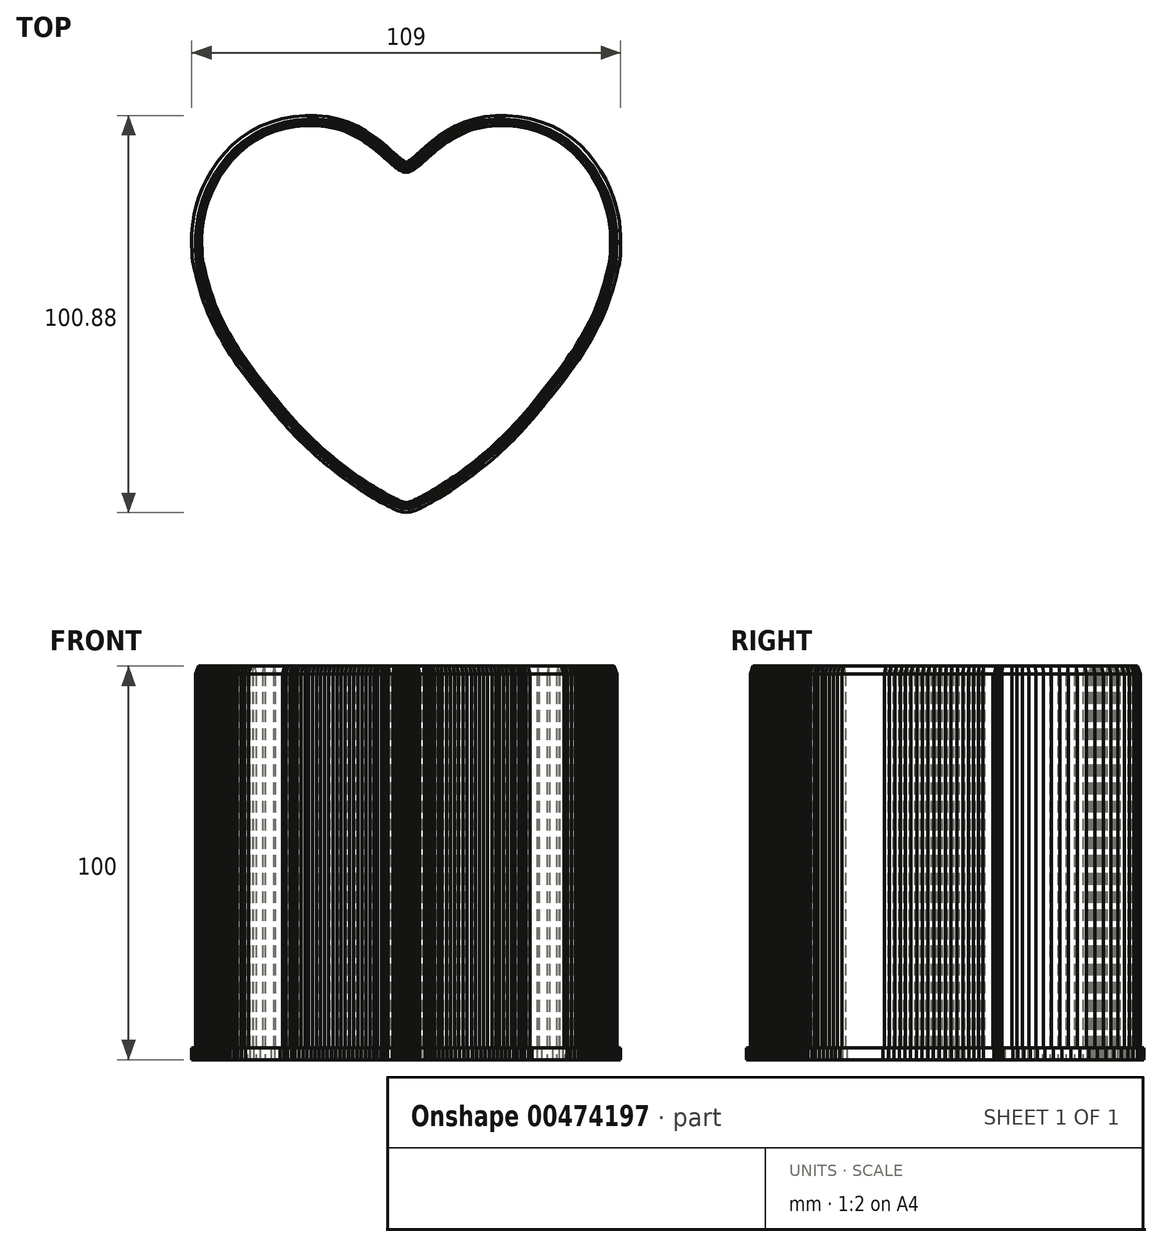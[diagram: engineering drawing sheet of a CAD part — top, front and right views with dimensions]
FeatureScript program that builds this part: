
annotation { "Feature Type Name" : "Feature", "Feature Type Description" : "" }
export const myFeature = defineFeature(function(context is Context, id is Id, definition is map)
    precondition{}
    {
        {
            var Q0;
            Q0=qCreatedBy(makeId("Top.planeOp"),FACE);
            var sketch = newSketch(context, id + "F0", { "sketchPlane" : qUnion([Q0])});
            skLineSegment(sketch, "E0", {"start": v(-2.52, 39.71) * mm, "end": v(-3.6, 40.68) * mm});
            skLineSegment(sketch, "E1", {"start": v(-3.6, 40.68) * mm, "end": v(-4.9, 41.83) * mm});
            skLineSegment(sketch, "E2", {"start": v(-4.9, 41.83) * mm, "end": v(-6.41, 43.08) * mm});
            skLineSegment(sketch, "E3", {"start": v(-6.41, 43.08) * mm, "end": v(-8.12, 44.37) * mm});
            skLineSegment(sketch, "E4", {"start": v(-8.12, 44.37) * mm, "end": v(-10.02, 45.64) * mm});
            skLineSegment(sketch, "E5", {"start": v(-10.02, 45.64) * mm, "end": v(-12.12, 46.83) * mm});
            skLineSegment(sketch, "E6", {"start": v(-12.12, 46.83) * mm, "end": v(-14.4, 47.86) * mm});
            skLineSegment(sketch, "E7", {"start": v(-14.4, 47.86) * mm, "end": v(-16.88, 48.68) * mm});
            skLineSegment(sketch, "E8", {"start": v(-16.88, 48.68) * mm, "end": v(-19.52, 49.24) * mm});
            skLineSegment(sketch, "E9", {"start": v(-19.52, 49.24) * mm, "end": v(-22.3, 49.52) * mm});
            skLineSegment(sketch, "E10", {"start": v(-22.3, 49.52) * mm, "end": v(-25.16, 49.52) * mm});
            skLineSegment(sketch, "E11", {"start": v(-25.16, 49.52) * mm, "end": v(-28.05, 49.25) * mm});
            skLineSegment(sketch, "E12", {"start": v(-28.05, 49.25) * mm, "end": v(-30.93, 48.72) * mm});
            skLineSegment(sketch, "E13", {"start": v(-30.93, 48.72) * mm, "end": v(-33.74, 47.91) * mm});
            skLineSegment(sketch, "E14", {"start": v(-33.74, 47.91) * mm, "end": v(-36.43, 46.84) * mm});
            skLineSegment(sketch, "E15", {"start": v(-36.43, 46.84) * mm, "end": v(-38.97, 45.5) * mm});
            skLineSegment(sketch, "E16", {"start": v(-38.97, 45.5) * mm, "end": v(-41.3, 43.92) * mm});
            skLineSegment(sketch, "E17", {"start": v(-41.3, 43.92) * mm, "end": v(-43.42, 42.11) * mm});
            skLineSegment(sketch, "E18", {"start": v(-43.42, 42.11) * mm, "end": v(-45.33, 40.13) * mm});
            skLineSegment(sketch, "E19", {"start": v(-45.33, 40.13) * mm, "end": v(-47.03, 38.01) * mm});
            skLineSegment(sketch, "E20", {"start": v(-47.03, 38.01) * mm, "end": v(-48.51, 35.8) * mm});
            skLineSegment(sketch, "E21", {"start": v(-48.51, 35.8) * mm, "end": v(-49.8, 33.56) * mm});
            skLineSegment(sketch, "E22", {"start": v(-49.8, 33.56) * mm, "end": v(-50.86, 31.3) * mm});
            skLineSegment(sketch, "E23", {"start": v(-50.86, 31.3) * mm, "end": v(-51.72, 29.1) * mm});
            skLineSegment(sketch, "E24", {"start": v(-51.72, 29.1) * mm, "end": v(-52.38, 26.96) * mm});
            skLineSegment(sketch, "E25", {"start": v(-52.38, 26.96) * mm, "end": v(-52.86, 24.92) * mm});
            skLineSegment(sketch, "E26", {"start": v(-52.86, 24.92) * mm, "end": v(-53.18, 23) * mm});
            skLineSegment(sketch, "E27", {"start": v(-53.18, 23) * mm, "end": v(-53.38, 21.24) * mm});
            skLineSegment(sketch, "E28", {"start": v(-53.38, 21.24) * mm, "end": v(-53.48, 19.62) * mm});
            skLineSegment(sketch, "E29", {"start": v(-53.48, 19.62) * mm, "end": v(-53.5, 18.18) * mm});
            skLineSegment(sketch, "E30", {"start": v(-53.5, 18.18) * mm, "end": v(-53.49, 16.93) * mm});
            skLineSegment(sketch, "E31", {"start": v(-53.49, 16.93) * mm, "end": v(-53.45, 15.9) * mm});
            skLineSegment(sketch, "E32", {"start": v(-53.45, 15.9) * mm, "end": v(-53.42, 15.07) * mm});
            skLineSegment(sketch, "E33", {"start": v(-53.42, 15.07) * mm, "end": v(-53.38, 14.44) * mm});
            skLineSegment(sketch, "E34", {"start": v(-53.38, 14.44) * mm, "end": v(-53.35, 13.92) * mm});
            skLineSegment(sketch, "E35", {"start": v(-53.35, 13.92) * mm, "end": v(-53.3, 13.49) * mm});
            skLineSegment(sketch, "E36", {"start": v(-53.3, 13.49) * mm, "end": v(-53.24, 13.07) * mm});
            skLineSegment(sketch, "E37", {"start": v(-53.24, 13.07) * mm, "end": v(-53.16, 12.62) * mm});
            skLineSegment(sketch, "E38", {"start": v(-53.16, 12.62) * mm, "end": v(-53.04, 12.1) * mm});
            skLineSegment(sketch, "E39", {"start": v(-53.04, 12.1) * mm, "end": v(-52.88, 11.43) * mm});
            skLineSegment(sketch, "E40", {"start": v(-52.88, 11.43) * mm, "end": v(-52.69, 10.6) * mm});
            skLineSegment(sketch, "E41", {"start": v(-52.69, 10.6) * mm, "end": v(-52.44, 9.6) * mm});
            skLineSegment(sketch, "E42", {"start": v(-52.44, 9.6) * mm, "end": v(-52.15, 8.45) * mm});
            skLineSegment(sketch, "E43", {"start": v(-52.15, 8.45) * mm, "end": v(-51.82, 7.2) * mm});
            skLineSegment(sketch, "E44", {"start": v(-51.82, 7.2) * mm, "end": v(-51.43, 5.85) * mm});
            skLineSegment(sketch, "E45", {"start": v(-51.43, 5.85) * mm, "end": v(-51, 4.44) * mm});
            skLineSegment(sketch, "E46", {"start": v(-51, 4.44) * mm, "end": v(-50.5, 2.98) * mm});
            skLineSegment(sketch, "E47", {"start": v(-50.5, 2.98) * mm, "end": v(-49.96, 1.5) * mm});
            skLineSegment(sketch, "E48", {"start": v(-49.96, 1.5) * mm, "end": v(-49.36, 0.03) * mm});
            skLineSegment(sketch, "E49", {"start": v(-49.36, 0.03) * mm, "end": v(-48.7, -1.44) * mm});
            skLineSegment(sketch, "E50", {"start": v(-48.7, -1.44) * mm, "end": v(-48, -2.9) * mm});
            skLineSegment(sketch, "E51", {"start": v(-48, -2.9) * mm, "end": v(-47.26, -4.36) * mm});
            skLineSegment(sketch, "E52", {"start": v(-47.26, -4.36) * mm, "end": v(-46.47, -5.8) * mm});
            skLineSegment(sketch, "E53", {"start": v(-46.47, -5.8) * mm, "end": v(-45.64, -7.23) * mm});
            skLineSegment(sketch, "E54", {"start": v(-45.64, -7.23) * mm, "end": v(-44.78, -8.65) * mm});
            skLineSegment(sketch, "E55", {"start": v(-44.78, -8.65) * mm, "end": v(-43.88, -10.05) * mm});
            skLineSegment(sketch, "E56", {"start": v(-43.88, -10.05) * mm, "end": v(-42.95, -11.44) * mm});
            skLineSegment(sketch, "E57", {"start": v(-42.95, -11.44) * mm, "end": v(-42, -12.8) * mm});
            skLineSegment(sketch, "E58", {"start": v(-42, -12.8) * mm, "end": v(-41.04, -14.16) * mm});
            skLineSegment(sketch, "E59", {"start": v(-41.04, -14.16) * mm, "end": v(-40.05, -15.49) * mm});
            skLineSegment(sketch, "E60", {"start": v(-40.05, -15.49) * mm, "end": v(-39.07, -16.8) * mm});
            skLineSegment(sketch, "E61", {"start": v(-39.07, -16.8) * mm, "end": v(-38.08, -18.08) * mm});
            skLineSegment(sketch, "E62", {"start": v(-38.08, -18.08) * mm, "end": v(-37.1, -19.33) * mm});
            skLineSegment(sketch, "E63", {"start": v(-37.1, -19.33) * mm, "end": v(-36.12, -20.56) * mm});
            skLineSegment(sketch, "E64", {"start": v(-36.12, -20.56) * mm, "end": v(-35.16, -21.76) * mm});
            skLineSegment(sketch, "E65", {"start": v(-35.16, -21.76) * mm, "end": v(-34.22, -22.93) * mm});
            skLineSegment(sketch, "E66", {"start": v(-34.22, -22.93) * mm, "end": v(-33.28, -24.07) * mm});
            skLineSegment(sketch, "E67", {"start": v(-33.28, -24.07) * mm, "end": v(-32.35, -25.18) * mm});
            skLineSegment(sketch, "E68", {"start": v(-32.35, -25.18) * mm, "end": v(-31.42, -26.28) * mm});
            skLineSegment(sketch, "E69", {"start": v(-31.42, -26.28) * mm, "end": v(-30.5, -27.34) * mm});
            skLineSegment(sketch, "E70", {"start": v(-30.5, -27.34) * mm, "end": v(-29.56, -28.38) * mm});
            skLineSegment(sketch, "E71", {"start": v(-29.56, -28.38) * mm, "end": v(-28.62, -29.4) * mm});
            skLineSegment(sketch, "E72", {"start": v(-28.62, -29.4) * mm, "end": v(-27.67, -30.4) * mm});
            skLineSegment(sketch, "E73", {"start": v(-27.67, -30.4) * mm, "end": v(-26.71, -31.38) * mm});
            skLineSegment(sketch, "E74", {"start": v(-26.71, -31.38) * mm, "end": v(-25.74, -32.34) * mm});
            skLineSegment(sketch, "E75", {"start": v(-25.74, -32.34) * mm, "end": v(-24.76, -33.28) * mm});
            skLineSegment(sketch, "E76", {"start": v(-24.76, -33.28) * mm, "end": v(-23.77, -34.2) * mm});
            skLineSegment(sketch, "E77", {"start": v(-23.77, -34.2) * mm, "end": v(-22.76, -35.1) * mm});
            skLineSegment(sketch, "E78", {"start": v(-22.76, -35.1) * mm, "end": v(-21.75, -36) * mm});
            skLineSegment(sketch, "E79", {"start": v(-21.75, -36) * mm, "end": v(-20.72, -36.87) * mm});
            skLineSegment(sketch, "E80", {"start": v(-20.72, -36.87) * mm, "end": v(-19.69, -37.74) * mm});
            skLineSegment(sketch, "E81", {"start": v(-19.69, -37.74) * mm, "end": v(-18.64, -38.58) * mm});
            skLineSegment(sketch, "E82", {"start": v(-18.64, -38.58) * mm, "end": v(-17.6, -39.42) * mm});
            skLineSegment(sketch, "E83", {"start": v(-17.6, -39.42) * mm, "end": v(-16.53, -40.23) * mm});
            skLineSegment(sketch, "E84", {"start": v(-16.53, -40.23) * mm, "end": v(-15.47, -41.02) * mm});
            skLineSegment(sketch, "E85", {"start": v(-15.47, -41.02) * mm, "end": v(-14.41, -41.8) * mm});
            skLineSegment(sketch, "E86", {"start": v(-14.41, -41.8) * mm, "end": v(-13.35, -42.55) * mm});
            skLineSegment(sketch, "E87", {"start": v(-13.35, -42.55) * mm, "end": v(-12.29, -43.27) * mm});
            skLineSegment(sketch, "E88", {"start": v(-12.29, -43.27) * mm, "end": v(-11.23, -43.97) * mm});
            skLineSegment(sketch, "E89", {"start": v(-11.23, -43.97) * mm, "end": v(-10.19, -44.65) * mm});
            skLineSegment(sketch, "E90", {"start": v(-10.19, -44.65) * mm, "end": v(-9.17, -45.28) * mm});
            skLineSegment(sketch, "E91", {"start": v(-9.17, -45.28) * mm, "end": v(-8.17, -45.88) * mm});
            skLineSegment(sketch, "E92", {"start": v(-8.17, -45.88) * mm, "end": v(-7.22, -46.44) * mm});
            skLineSegment(sketch, "E93", {"start": v(-7.22, -46.44) * mm, "end": v(-6.3, -46.95) * mm});
            skLineSegment(sketch, "E94", {"start": v(-6.3, -46.95) * mm, "end": v(-5.46, -47.42) * mm});
            skLineSegment(sketch, "E95", {"start": v(-5.46, -47.42) * mm, "end": v(-4.67, -47.83) * mm});
            skLineSegment(sketch, "E96", {"start": v(-4.67, -47.83) * mm, "end": v(-3.96, -48.18) * mm});
            skLineSegment(sketch, "E97", {"start": v(-3.96, -48.18) * mm, "end": v(-3.35, -48.48) * mm});
            skLineSegment(sketch, "E98", {"start": v(-3.35, -48.48) * mm, "end": v(-2.8, -48.74) * mm});
            skLineSegment(sketch, "E99", {"start": v(-2.8, -48.74) * mm, "end": v(-2.31, -48.95) * mm});
            skLineSegment(sketch, "E100", {"start": v(-2.31, -48.95) * mm, "end": v(-1.86, -49.12) * mm});
            skLineSegment(sketch, "E101", {"start": v(-1.86, -49.12) * mm, "end": v(-1.44, -49.26) * mm});
            skLineSegment(sketch, "E102", {"start": v(-1.44, -49.26) * mm, "end": v(-1.04, -49.36) * mm});
            skLineSegment(sketch, "E103", {"start": v(-1.04, -49.36) * mm, "end": v(-0.63, -49.42) * mm});
            skLineSegment(sketch, "E104", {"start": v(-0.63, -49.42) * mm, "end": v(0, -49.52) * mm});
            skLineSegment(sketch, "E105", {"start": v(0, -49.52) * mm, "end": v(0.63, -49.42) * mm});
            skLineSegment(sketch, "E106", {"start": v(0.63, -49.42) * mm, "end": v(1.04, -49.36) * mm});
            skLineSegment(sketch, "E107", {"start": v(1.04, -49.36) * mm, "end": v(1.44, -49.26) * mm});
            skLineSegment(sketch, "E108", {"start": v(1.44, -49.26) * mm, "end": v(1.86, -49.12) * mm});
            skLineSegment(sketch, "E109", {"start": v(1.86, -49.12) * mm, "end": v(2.31, -48.95) * mm});
            skLineSegment(sketch, "E110", {"start": v(2.31, -48.95) * mm, "end": v(2.8, -48.74) * mm});
            skLineSegment(sketch, "E111", {"start": v(2.8, -48.74) * mm, "end": v(3.35, -48.48) * mm});
            skLineSegment(sketch, "E112", {"start": v(3.35, -48.48) * mm, "end": v(3.96, -48.18) * mm});
            skLineSegment(sketch, "E113", {"start": v(3.96, -48.18) * mm, "end": v(4.67, -47.83) * mm});
            skLineSegment(sketch, "E114", {"start": v(4.67, -47.83) * mm, "end": v(5.46, -47.42) * mm});
            skLineSegment(sketch, "E115", {"start": v(5.46, -47.42) * mm, "end": v(6.3, -46.95) * mm});
            skLineSegment(sketch, "E116", {"start": v(6.3, -46.95) * mm, "end": v(7.22, -46.44) * mm});
            skLineSegment(sketch, "E117", {"start": v(7.22, -46.44) * mm, "end": v(8.17, -45.88) * mm});
            skLineSegment(sketch, "E118", {"start": v(8.17, -45.88) * mm, "end": v(9.17, -45.28) * mm});
            skLineSegment(sketch, "E119", {"start": v(9.17, -45.28) * mm, "end": v(10.19, -44.65) * mm});
            skLineSegment(sketch, "E120", {"start": v(10.19, -44.65) * mm, "end": v(11.23, -43.97) * mm});
            skLineSegment(sketch, "E121", {"start": v(11.23, -43.97) * mm, "end": v(12.29, -43.27) * mm});
            skLineSegment(sketch, "E122", {"start": v(12.29, -43.27) * mm, "end": v(13.35, -42.55) * mm});
            skLineSegment(sketch, "E123", {"start": v(13.35, -42.55) * mm, "end": v(14.41, -41.8) * mm});
            skLineSegment(sketch, "E124", {"start": v(14.41, -41.8) * mm, "end": v(15.47, -41.02) * mm});
            skLineSegment(sketch, "E125", {"start": v(15.47, -41.02) * mm, "end": v(16.53, -40.23) * mm});
            skLineSegment(sketch, "E126", {"start": v(16.53, -40.23) * mm, "end": v(17.6, -39.42) * mm});
            skLineSegment(sketch, "E127", {"start": v(17.6, -39.42) * mm, "end": v(18.64, -38.58) * mm});
            skLineSegment(sketch, "E128", {"start": v(18.64, -38.58) * mm, "end": v(19.69, -37.74) * mm});
            skLineSegment(sketch, "E129", {"start": v(19.69, -37.74) * mm, "end": v(20.72, -36.87) * mm});
            skLineSegment(sketch, "E130", {"start": v(20.72, -36.87) * mm, "end": v(21.75, -36) * mm});
            skLineSegment(sketch, "E131", {"start": v(21.75, -36) * mm, "end": v(22.76, -35.1) * mm});
            skLineSegment(sketch, "E132", {"start": v(22.76, -35.1) * mm, "end": v(23.77, -34.2) * mm});
            skLineSegment(sketch, "E133", {"start": v(23.77, -34.2) * mm, "end": v(24.76, -33.28) * mm});
            skLineSegment(sketch, "E134", {"start": v(24.76, -33.28) * mm, "end": v(25.74, -32.34) * mm});
            skLineSegment(sketch, "E135", {"start": v(25.74, -32.34) * mm, "end": v(26.71, -31.38) * mm});
            skLineSegment(sketch, "E136", {"start": v(26.71, -31.38) * mm, "end": v(27.67, -30.4) * mm});
            skLineSegment(sketch, "E137", {"start": v(27.67, -30.4) * mm, "end": v(28.62, -29.4) * mm});
            skLineSegment(sketch, "E138", {"start": v(28.62, -29.4) * mm, "end": v(29.56, -28.38) * mm});
            skLineSegment(sketch, "E139", {"start": v(29.56, -28.38) * mm, "end": v(30.5, -27.34) * mm});
            skLineSegment(sketch, "E140", {"start": v(30.5, -27.34) * mm, "end": v(31.42, -26.28) * mm});
            skLineSegment(sketch, "E141", {"start": v(31.42, -26.28) * mm, "end": v(32.35, -25.18) * mm});
            skLineSegment(sketch, "E142", {"start": v(32.35, -25.18) * mm, "end": v(33.28, -24.07) * mm});
            skLineSegment(sketch, "E143", {"start": v(33.28, -24.07) * mm, "end": v(34.22, -22.93) * mm});
            skLineSegment(sketch, "E144", {"start": v(34.22, -22.93) * mm, "end": v(35.16, -21.76) * mm});
            skLineSegment(sketch, "E145", {"start": v(35.16, -21.76) * mm, "end": v(36.12, -20.56) * mm});
            skLineSegment(sketch, "E146", {"start": v(36.12, -20.56) * mm, "end": v(37.1, -19.33) * mm});
            skLineSegment(sketch, "E147", {"start": v(37.1, -19.33) * mm, "end": v(38.08, -18.08) * mm});
            skLineSegment(sketch, "E148", {"start": v(38.08, -18.08) * mm, "end": v(39.07, -16.8) * mm});
            skLineSegment(sketch, "E149", {"start": v(39.07, -16.8) * mm, "end": v(40.05, -15.49) * mm});
            skLineSegment(sketch, "E150", {"start": v(40.05, -15.49) * mm, "end": v(41.04, -14.16) * mm});
            skLineSegment(sketch, "E151", {"start": v(41.04, -14.16) * mm, "end": v(42, -12.8) * mm});
            skLineSegment(sketch, "E152", {"start": v(42, -12.8) * mm, "end": v(42.95, -11.44) * mm});
            skLineSegment(sketch, "E153", {"start": v(42.95, -11.44) * mm, "end": v(43.88, -10.05) * mm});
            skLineSegment(sketch, "E154", {"start": v(43.88, -10.05) * mm, "end": v(44.78, -8.65) * mm});
            skLineSegment(sketch, "E155", {"start": v(44.78, -8.65) * mm, "end": v(45.64, -7.23) * mm});
            skLineSegment(sketch, "E156", {"start": v(45.64, -7.23) * mm, "end": v(46.47, -5.8) * mm});
            skLineSegment(sketch, "E157", {"start": v(46.47, -5.8) * mm, "end": v(47.26, -4.36) * mm});
            skLineSegment(sketch, "E158", {"start": v(47.26, -4.36) * mm, "end": v(48, -2.9) * mm});
            skLineSegment(sketch, "E159", {"start": v(48, -2.9) * mm, "end": v(48.7, -1.44) * mm});
            skLineSegment(sketch, "E160", {"start": v(48.7, -1.44) * mm, "end": v(49.36, 0.03) * mm});
            skLineSegment(sketch, "E161", {"start": v(49.36, 0.03) * mm, "end": v(49.96, 1.5) * mm});
            skLineSegment(sketch, "E162", {"start": v(49.96, 1.5) * mm, "end": v(50.5, 2.98) * mm});
            skLineSegment(sketch, "E163", {"start": v(50.5, 2.98) * mm, "end": v(51, 4.44) * mm});
            skLineSegment(sketch, "E164", {"start": v(51, 4.44) * mm, "end": v(51.43, 5.85) * mm});
            skLineSegment(sketch, "E165", {"start": v(51.43, 5.85) * mm, "end": v(51.82, 7.2) * mm});
            skLineSegment(sketch, "E166", {"start": v(51.82, 7.2) * mm, "end": v(52.15, 8.45) * mm});
            skLineSegment(sketch, "E167", {"start": v(52.15, 8.45) * mm, "end": v(52.44, 9.6) * mm});
            skLineSegment(sketch, "E168", {"start": v(52.44, 9.6) * mm, "end": v(52.69, 10.6) * mm});
            skLineSegment(sketch, "E169", {"start": v(52.69, 10.6) * mm, "end": v(52.88, 11.43) * mm});
            skLineSegment(sketch, "E170", {"start": v(52.88, 11.43) * mm, "end": v(53.04, 12.1) * mm});
            skLineSegment(sketch, "E171", {"start": v(53.04, 12.1) * mm, "end": v(53.16, 12.62) * mm});
            skLineSegment(sketch, "E172", {"start": v(53.16, 12.62) * mm, "end": v(53.24, 13.07) * mm});
            skLineSegment(sketch, "E173", {"start": v(53.24, 13.07) * mm, "end": v(53.3, 13.49) * mm});
            skLineSegment(sketch, "E174", {"start": v(53.3, 13.49) * mm, "end": v(53.35, 13.92) * mm});
            skLineSegment(sketch, "E175", {"start": v(53.35, 13.92) * mm, "end": v(53.38, 14.44) * mm});
            skLineSegment(sketch, "E176", {"start": v(53.38, 14.44) * mm, "end": v(53.42, 15.07) * mm});
            skLineSegment(sketch, "E177", {"start": v(53.42, 15.07) * mm, "end": v(53.45, 15.9) * mm});
            skLineSegment(sketch, "E178", {"start": v(53.45, 15.9) * mm, "end": v(53.49, 16.93) * mm});
            skLineSegment(sketch, "E179", {"start": v(53.49, 16.93) * mm, "end": v(53.5, 18.18) * mm});
            skLineSegment(sketch, "E180", {"start": v(53.5, 18.18) * mm, "end": v(53.48, 19.62) * mm});
            skLineSegment(sketch, "E181", {"start": v(53.48, 19.62) * mm, "end": v(53.38, 21.24) * mm});
            skLineSegment(sketch, "E182", {"start": v(53.38, 21.24) * mm, "end": v(53.18, 23) * mm});
            skLineSegment(sketch, "E183", {"start": v(53.18, 23) * mm, "end": v(52.86, 24.92) * mm});
            skLineSegment(sketch, "E184", {"start": v(52.86, 24.92) * mm, "end": v(52.38, 26.96) * mm});
            skLineSegment(sketch, "E185", {"start": v(52.38, 26.96) * mm, "end": v(51.72, 29.1) * mm});
            skLineSegment(sketch, "E186", {"start": v(51.72, 29.1) * mm, "end": v(50.86, 31.3) * mm});
            skLineSegment(sketch, "E187", {"start": v(50.86, 31.3) * mm, "end": v(49.8, 33.56) * mm});
            skLineSegment(sketch, "E188", {"start": v(49.8, 33.56) * mm, "end": v(48.51, 35.8) * mm});
            skLineSegment(sketch, "E189", {"start": v(48.51, 35.8) * mm, "end": v(47.03, 38.01) * mm});
            skLineSegment(sketch, "E190", {"start": v(47.03, 38.01) * mm, "end": v(45.33, 40.13) * mm});
            skLineSegment(sketch, "E191", {"start": v(45.33, 40.13) * mm, "end": v(43.42, 42.11) * mm});
            skLineSegment(sketch, "E192", {"start": v(43.42, 42.11) * mm, "end": v(41.3, 43.92) * mm});
            skLineSegment(sketch, "E193", {"start": v(41.3, 43.92) * mm, "end": v(38.97, 45.5) * mm});
            skLineSegment(sketch, "E194", {"start": v(38.97, 45.5) * mm, "end": v(36.43, 46.84) * mm});
            skLineSegment(sketch, "E195", {"start": v(36.43, 46.84) * mm, "end": v(33.74, 47.91) * mm});
            skLineSegment(sketch, "E196", {"start": v(33.74, 47.91) * mm, "end": v(30.93, 48.72) * mm});
            skLineSegment(sketch, "E197", {"start": v(30.93, 48.72) * mm, "end": v(28.05, 49.25) * mm});
            skLineSegment(sketch, "E198", {"start": v(28.05, 49.25) * mm, "end": v(25.16, 49.52) * mm});
            skLineSegment(sketch, "E199", {"start": v(25.16, 49.52) * mm, "end": v(22.3, 49.52) * mm});
            skLineSegment(sketch, "E200", {"start": v(22.3, 49.52) * mm, "end": v(19.52, 49.24) * mm});
            skLineSegment(sketch, "E201", {"start": v(19.52, 49.24) * mm, "end": v(16.88, 48.68) * mm});
            skLineSegment(sketch, "E202", {"start": v(16.88, 48.68) * mm, "end": v(14.4, 47.86) * mm});
            skLineSegment(sketch, "E203", {"start": v(14.4, 47.86) * mm, "end": v(12.12, 46.83) * mm});
            skLineSegment(sketch, "E204", {"start": v(12.12, 46.83) * mm, "end": v(10.02, 45.64) * mm});
            skLineSegment(sketch, "E205", {"start": v(10.02, 45.64) * mm, "end": v(8.12, 44.37) * mm});
            skLineSegment(sketch, "E206", {"start": v(8.12, 44.37) * mm, "end": v(6.41, 43.08) * mm});
            skLineSegment(sketch, "E207", {"start": v(6.41, 43.08) * mm, "end": v(4.9, 41.83) * mm});
            skLineSegment(sketch, "E208", {"start": v(4.9, 41.83) * mm, "end": v(3.6, 40.68) * mm});
            skLineSegment(sketch, "E209", {"start": v(3.6, 40.68) * mm, "end": v(2.52, 39.71) * mm});
            skLineSegment(sketch, "E210", {"start": v(2.52, 39.71) * mm, "end": v(2.06, 39.32) * mm});
            skLineSegment(sketch, "E211", {"start": v(2.06, 39.32) * mm, "end": v(1.65, 38.97) * mm});
            skLineSegment(sketch, "E212", {"start": v(1.65, 38.97) * mm, "end": v(1.29, 38.68) * mm});
            skLineSegment(sketch, "E213", {"start": v(1.29, 38.68) * mm, "end": v(0.96, 38.43) * mm});
            skLineSegment(sketch, "E214", {"start": v(0.96, 38.43) * mm, "end": v(0.68, 38.23) * mm});
            skLineSegment(sketch, "E215", {"start": v(0.68, 38.23) * mm, "end": v(0.42, 38.07) * mm});
            skLineSegment(sketch, "E216", {"start": v(0.42, 38.07) * mm, "end": v(0.2, 37.95) * mm});
            skLineSegment(sketch, "E217", {"start": v(0.2, 37.95) * mm, "end": v(0, 37.87) * mm});
            skLineSegment(sketch, "E218", {"start": v(0, 37.87) * mm, "end": v(-0.2, 37.95) * mm});
            skLineSegment(sketch, "E219", {"start": v(-0.2, 37.95) * mm, "end": v(-0.42, 38.07) * mm});
            skLineSegment(sketch, "E220", {"start": v(-0.42, 38.07) * mm, "end": v(-0.68, 38.23) * mm});
            skLineSegment(sketch, "E221", {"start": v(-0.68, 38.23) * mm, "end": v(-0.96, 38.43) * mm});
            skLineSegment(sketch, "E222", {"start": v(-0.96, 38.43) * mm, "end": v(-1.29, 38.68) * mm});
            skLineSegment(sketch, "E223", {"start": v(-1.29, 38.68) * mm, "end": v(-1.65, 38.97) * mm});
            skLineSegment(sketch, "E224", {"start": v(-1.65, 38.97) * mm, "end": v(-2.06, 39.32) * mm});
            skLineSegment(sketch, "E225", {"start": v(-2.06, 39.32) * mm, "end": v(-2.52, 39.71) * mm});
            skSolve(sketch);
        }
        {
            var Q0;
            Q0 = qSketchRegion(id + "F0", true);
            extrude(context, id + "F1", {"entities" : qUnion([Q0]), "depth" : 100 * mm, "offsetDistance" : 25 * mm});
        }
        {
            var Q0;
            Q0=makeQuery(id+"F1.opExtrude","CAP_FACE",FACE,{"disambiguationData":[OSD([sQuery(id+"F0.wireOp",EDGE,"E0"),sQuery(id+"F0.wireOp",EDGE,"E1"),sQuery(id+"F0.wireOp",EDGE,"E2"),sQuery(id+"F0.wireOp",EDGE,"E3"),sQuery(id+"F0.wireOp",EDGE,"E4"),sQuery(id+"F0.wireOp",EDGE,"E5"),sQuery(id+"F0.wireOp",EDGE,"E6"),sQuery(id+"F0.wireOp",EDGE,"E7"),sQuery(id+"F0.wireOp",EDGE,"E8"),sQuery(id+"F0.wireOp",EDGE,"E9"),sQuery(id+"F0.wireOp",EDGE,"E10"),sQuery(id+"F0.wireOp",EDGE,"E11"),sQuery(id+"F0.wireOp",EDGE,"E12"),sQuery(id+"F0.wireOp",EDGE,"E13"),sQuery(id+"F0.wireOp",EDGE,"E14"),sQuery(id+"F0.wireOp",EDGE,"E15"),sQuery(id+"F0.wireOp",EDGE,"E16"),sQuery(id+"F0.wireOp",EDGE,"E17"),sQuery(id+"F0.wireOp",EDGE,"E18"),sQuery(id+"F0.wireOp",EDGE,"E19"),sQuery(id+"F0.wireOp",EDGE,"E20"),sQuery(id+"F0.wireOp",EDGE,"E21"),sQuery(id+"F0.wireOp",EDGE,"E22"),sQuery(id+"F0.wireOp",EDGE,"E23"),sQuery(id+"F0.wireOp",EDGE,"E24"),sQuery(id+"F0.wireOp",EDGE,"E25"),sQuery(id+"F0.wireOp",EDGE,"E26"),sQuery(id+"F0.wireOp",EDGE,"E27"),sQuery(id+"F0.wireOp",EDGE,"E28"),sQuery(id+"F0.wireOp",EDGE,"E29"),sQuery(id+"F0.wireOp",EDGE,"E30"),sQuery(id+"F0.wireOp",EDGE,"E31"),sQuery(id+"F0.wireOp",EDGE,"E32"),sQuery(id+"F0.wireOp",EDGE,"E33"),sQuery(id+"F0.wireOp",EDGE,"E34"),sQuery(id+"F0.wireOp",EDGE,"E35"),sQuery(id+"F0.wireOp",EDGE,"E36"),sQuery(id+"F0.wireOp",EDGE,"E37"),sQuery(id+"F0.wireOp",EDGE,"E38"),sQuery(id+"F0.wireOp",EDGE,"E39"),sQuery(id+"F0.wireOp",EDGE,"E40"),sQuery(id+"F0.wireOp",EDGE,"E41"),sQuery(id+"F0.wireOp",EDGE,"E42"),sQuery(id+"F0.wireOp",EDGE,"E43"),sQuery(id+"F0.wireOp",EDGE,"E44"),sQuery(id+"F0.wireOp",EDGE,"E45"),sQuery(id+"F0.wireOp",EDGE,"E46"),sQuery(id+"F0.wireOp",EDGE,"E47"),sQuery(id+"F0.wireOp",EDGE,"E48"),sQuery(id+"F0.wireOp",EDGE,"E49"),sQuery(id+"F0.wireOp",EDGE,"E50"),sQuery(id+"F0.wireOp",EDGE,"E51"),sQuery(id+"F0.wireOp",EDGE,"E52"),sQuery(id+"F0.wireOp",EDGE,"E53"),sQuery(id+"F0.wireOp",EDGE,"E54"),sQuery(id+"F0.wireOp",EDGE,"E55"),sQuery(id+"F0.wireOp",EDGE,"E56"),sQuery(id+"F0.wireOp",EDGE,"E57"),sQuery(id+"F0.wireOp",EDGE,"E58"),sQuery(id+"F0.wireOp",EDGE,"E59"),sQuery(id+"F0.wireOp",EDGE,"E60"),sQuery(id+"F0.wireOp",EDGE,"E61"),sQuery(id+"F0.wireOp",EDGE,"E62"),sQuery(id+"F0.wireOp",EDGE,"E63"),sQuery(id+"F0.wireOp",EDGE,"E64"),sQuery(id+"F0.wireOp",EDGE,"E65"),sQuery(id+"F0.wireOp",EDGE,"E66"),sQuery(id+"F0.wireOp",EDGE,"E67"),sQuery(id+"F0.wireOp",EDGE,"E68"),sQuery(id+"F0.wireOp",EDGE,"E69"),sQuery(id+"F0.wireOp",EDGE,"E70"),sQuery(id+"F0.wireOp",EDGE,"E71"),sQuery(id+"F0.wireOp",EDGE,"E72"),sQuery(id+"F0.wireOp",EDGE,"E73"),sQuery(id+"F0.wireOp",EDGE,"E74"),sQuery(id+"F0.wireOp",EDGE,"E75"),sQuery(id+"F0.wireOp",EDGE,"E76"),sQuery(id+"F0.wireOp",EDGE,"E77"),sQuery(id+"F0.wireOp",EDGE,"E78"),sQuery(id+"F0.wireOp",EDGE,"E79"),sQuery(id+"F0.wireOp",EDGE,"E80"),sQuery(id+"F0.wireOp",EDGE,"E81"),sQuery(id+"F0.wireOp",EDGE,"E82"),sQuery(id+"F0.wireOp",EDGE,"E83"),sQuery(id+"F0.wireOp",EDGE,"E84"),sQuery(id+"F0.wireOp",EDGE,"E85"),sQuery(id+"F0.wireOp",EDGE,"E86"),sQuery(id+"F0.wireOp",EDGE,"E87"),sQuery(id+"F0.wireOp",EDGE,"E88"),sQuery(id+"F0.wireOp",EDGE,"E89"),sQuery(id+"F0.wireOp",EDGE,"E90"),sQuery(id+"F0.wireOp",EDGE,"E91"),sQuery(id+"F0.wireOp",EDGE,"E92"),sQuery(id+"F0.wireOp",EDGE,"E93"),sQuery(id+"F0.wireOp",EDGE,"E94"),sQuery(id+"F0.wireOp",EDGE,"E95"),sQuery(id+"F0.wireOp",EDGE,"E96"),sQuery(id+"F0.wireOp",EDGE,"E97"),sQuery(id+"F0.wireOp",EDGE,"E98"),sQuery(id+"F0.wireOp",EDGE,"E99"),sQuery(id+"F0.wireOp",EDGE,"E100"),sQuery(id+"F0.wireOp",EDGE,"E101"),sQuery(id+"F0.wireOp",EDGE,"E102"),sQuery(id+"F0.wireOp",EDGE,"E103"),sQuery(id+"F0.wireOp",EDGE,"E104"),sQuery(id+"F0.wireOp",EDGE,"E105"),sQuery(id+"F0.wireOp",EDGE,"E106"),sQuery(id+"F0.wireOp",EDGE,"E107"),sQuery(id+"F0.wireOp",EDGE,"E108"),sQuery(id+"F0.wireOp",EDGE,"E109"),sQuery(id+"F0.wireOp",EDGE,"E110"),sQuery(id+"F0.wireOp",EDGE,"E111"),sQuery(id+"F0.wireOp",EDGE,"E112"),sQuery(id+"F0.wireOp",EDGE,"E113"),sQuery(id+"F0.wireOp",EDGE,"E114"),sQuery(id+"F0.wireOp",EDGE,"E115"),sQuery(id+"F0.wireOp",EDGE,"E116"),sQuery(id+"F0.wireOp",EDGE,"E117"),sQuery(id+"F0.wireOp",EDGE,"E118"),sQuery(id+"F0.wireOp",EDGE,"E119"),sQuery(id+"F0.wireOp",EDGE,"E120"),sQuery(id+"F0.wireOp",EDGE,"E121"),sQuery(id+"F0.wireOp",EDGE,"E122"),sQuery(id+"F0.wireOp",EDGE,"E123"),sQuery(id+"F0.wireOp",EDGE,"E124"),sQuery(id+"F0.wireOp",EDGE,"E125"),sQuery(id+"F0.wireOp",EDGE,"E126"),sQuery(id+"F0.wireOp",EDGE,"E127"),sQuery(id+"F0.wireOp",EDGE,"E128"),sQuery(id+"F0.wireOp",EDGE,"E129"),sQuery(id+"F0.wireOp",EDGE,"E130"),sQuery(id+"F0.wireOp",EDGE,"E131"),sQuery(id+"F0.wireOp",EDGE,"E132"),sQuery(id+"F0.wireOp",EDGE,"E133"),sQuery(id+"F0.wireOp",EDGE,"E134"),sQuery(id+"F0.wireOp",EDGE,"E135"),sQuery(id+"F0.wireOp",EDGE,"E136"),sQuery(id+"F0.wireOp",EDGE,"E137"),sQuery(id+"F0.wireOp",EDGE,"E138"),sQuery(id+"F0.wireOp",EDGE,"E139"),sQuery(id+"F0.wireOp",EDGE,"E140"),sQuery(id+"F0.wireOp",EDGE,"E141"),sQuery(id+"F0.wireOp",EDGE,"E142"),sQuery(id+"F0.wireOp",EDGE,"E143"),sQuery(id+"F0.wireOp",EDGE,"E144"),sQuery(id+"F0.wireOp",EDGE,"E145"),sQuery(id+"F0.wireOp",EDGE,"E146"),sQuery(id+"F0.wireOp",EDGE,"E147"),sQuery(id+"F0.wireOp",EDGE,"E148"),sQuery(id+"F0.wireOp",EDGE,"E149"),sQuery(id+"F0.wireOp",EDGE,"E150"),sQuery(id+"F0.wireOp",EDGE,"E151"),sQuery(id+"F0.wireOp",EDGE,"E152"),sQuery(id+"F0.wireOp",EDGE,"E153"),sQuery(id+"F0.wireOp",EDGE,"E154"),sQuery(id+"F0.wireOp",EDGE,"E155"),sQuery(id+"F0.wireOp",EDGE,"E156"),sQuery(id+"F0.wireOp",EDGE,"E157"),sQuery(id+"F0.wireOp",EDGE,"E158"),sQuery(id+"F0.wireOp",EDGE,"E159"),sQuery(id+"F0.wireOp",EDGE,"E160"),sQuery(id+"F0.wireOp",EDGE,"E161"),sQuery(id+"F0.wireOp",EDGE,"E162"),sQuery(id+"F0.wireOp",EDGE,"E163"),sQuery(id+"F0.wireOp",EDGE,"E164"),sQuery(id+"F0.wireOp",EDGE,"E165"),sQuery(id+"F0.wireOp",EDGE,"E166"),sQuery(id+"F0.wireOp",EDGE,"E167"),sQuery(id+"F0.wireOp",EDGE,"E168"),sQuery(id+"F0.wireOp",EDGE,"E169"),sQuery(id+"F0.wireOp",EDGE,"E170"),sQuery(id+"F0.wireOp",EDGE,"E171"),sQuery(id+"F0.wireOp",EDGE,"E172"),sQuery(id+"F0.wireOp",EDGE,"E173"),sQuery(id+"F0.wireOp",EDGE,"E174"),sQuery(id+"F0.wireOp",EDGE,"E175"),sQuery(id+"F0.wireOp",EDGE,"E176"),sQuery(id+"F0.wireOp",EDGE,"E177"),sQuery(id+"F0.wireOp",EDGE,"E178"),sQuery(id+"F0.wireOp",EDGE,"E179"),sQuery(id+"F0.wireOp",EDGE,"E180"),sQuery(id+"F0.wireOp",EDGE,"E181"),sQuery(id+"F0.wireOp",EDGE,"E182"),sQuery(id+"F0.wireOp",EDGE,"E183"),sQuery(id+"F0.wireOp",EDGE,"E184"),sQuery(id+"F0.wireOp",EDGE,"E185"),sQuery(id+"F0.wireOp",EDGE,"E186"),sQuery(id+"F0.wireOp",EDGE,"E187"),sQuery(id+"F0.wireOp",EDGE,"E188"),sQuery(id+"F0.wireOp",EDGE,"E189"),sQuery(id+"F0.wireOp",EDGE,"E190"),sQuery(id+"F0.wireOp",EDGE,"E191"),sQuery(id+"F0.wireOp",EDGE,"E192"),sQuery(id+"F0.wireOp",EDGE,"E193"),sQuery(id+"F0.wireOp",EDGE,"E194"),sQuery(id+"F0.wireOp",EDGE,"E195"),sQuery(id+"F0.wireOp",EDGE,"E196"),sQuery(id+"F0.wireOp",EDGE,"E197"),sQuery(id+"F0.wireOp",EDGE,"E198"),sQuery(id+"F0.wireOp",EDGE,"E199"),sQuery(id+"F0.wireOp",EDGE,"E200"),sQuery(id+"F0.wireOp",EDGE,"E201"),sQuery(id+"F0.wireOp",EDGE,"E202"),sQuery(id+"F0.wireOp",EDGE,"E203"),sQuery(id+"F0.wireOp",EDGE,"E204"),sQuery(id+"F0.wireOp",EDGE,"E205"),sQuery(id+"F0.wireOp",EDGE,"E206"),sQuery(id+"F0.wireOp",EDGE,"E207"),sQuery(id+"F0.wireOp",EDGE,"E208"),sQuery(id+"F0.wireOp",EDGE,"E209"),sQuery(id+"F0.wireOp",EDGE,"E210"),sQuery(id+"F0.wireOp",EDGE,"E211"),sQuery(id+"F0.wireOp",EDGE,"E212"),sQuery(id+"F0.wireOp",EDGE,"E213"),sQuery(id+"F0.wireOp",EDGE,"E214"),sQuery(id+"F0.wireOp",EDGE,"E215"),sQuery(id+"F0.wireOp",EDGE,"E216"),sQuery(id+"F0.wireOp",EDGE,"E217"),sQuery(id+"F0.wireOp",EDGE,"E218"),sQuery(id+"F0.wireOp",EDGE,"E219"),sQuery(id+"F0.wireOp",EDGE,"E220"),sQuery(id+"F0.wireOp",EDGE,"E221"),sQuery(id+"F0.wireOp",EDGE,"E222"),sQuery(id+"F0.wireOp",EDGE,"E223"),sQuery(id+"F0.wireOp",EDGE,"E224"),sQuery(id+"F0.wireOp",EDGE,"E225")])],"isStart":false});
            shell(context, id + "F2", {"entities" : qUnion([Q0]), "thickness" : 1.5 * mm});
        }
        {
            var Q0;
            Q0=qCreatedBy(makeId("Top.planeOp"),FACE);
            var sketch = newSketch(context, id + "F3", { "sketchPlane" : qUnion([Q0])});
            skLineSegment(sketch, "E226", {"start": v(-2.57, 40.45) * mm, "end": v(-3.68, 41.44) * mm});
            skLineSegment(sketch, "E227", {"start": v(-3.68, 41.44) * mm, "end": v(-5, 42.6) * mm});
            skLineSegment(sketch, "E228", {"start": v(-5, 42.6) * mm, "end": v(-6.53, 43.88) * mm});
            skLineSegment(sketch, "E229", {"start": v(-6.53, 43.88) * mm, "end": v(-8.27, 45.2) * mm});
            skLineSegment(sketch, "E230", {"start": v(-8.27, 45.2) * mm, "end": v(-10.21, 46.49) * mm});
            skLineSegment(sketch, "E231", {"start": v(-10.21, 46.49) * mm, "end": v(-12.35, 47.7) * mm});
            skLineSegment(sketch, "E232", {"start": v(-12.35, 47.7) * mm, "end": v(-14.68, 48.75) * mm});
            skLineSegment(sketch, "E233", {"start": v(-14.68, 48.75) * mm, "end": v(-17.2, 49.59) * mm});
            skLineSegment(sketch, "E234", {"start": v(-17.2, 49.59) * mm, "end": v(-19.89, 50.15) * mm});
            skLineSegment(sketch, "E235", {"start": v(-19.89, 50.15) * mm, "end": v(-22.71, 50.44) * mm});
            skLineSegment(sketch, "E236", {"start": v(-22.71, 50.44) * mm, "end": v(-25.63, 50.44) * mm});
            skLineSegment(sketch, "E237", {"start": v(-25.63, 50.44) * mm, "end": v(-28.57, 50.17) * mm});
            skLineSegment(sketch, "E238", {"start": v(-28.57, 50.17) * mm, "end": v(-31.5, 49.62) * mm});
            skLineSegment(sketch, "E239", {"start": v(-31.5, 49.62) * mm, "end": v(-34.37, 48.8) * mm});
            skLineSegment(sketch, "E240", {"start": v(-34.37, 48.8) * mm, "end": v(-37.11, 47.71) * mm});
            skLineSegment(sketch, "E241", {"start": v(-37.11, 47.71) * mm, "end": v(-39.7, 46.35) * mm});
            skLineSegment(sketch, "E242", {"start": v(-39.7, 46.35) * mm, "end": v(-42.07, 44.74) * mm});
            skLineSegment(sketch, "E243", {"start": v(-42.07, 44.74) * mm, "end": v(-44.23, 42.9) * mm});
            skLineSegment(sketch, "E244", {"start": v(-44.23, 42.9) * mm, "end": v(-46.17, 40.88) * mm});
            skLineSegment(sketch, "E245", {"start": v(-46.17, 40.88) * mm, "end": v(-47.9, 38.72) * mm});
            skLineSegment(sketch, "E246", {"start": v(-47.9, 38.72) * mm, "end": v(-49.42, 36.48) * mm});
            skLineSegment(sketch, "E247", {"start": v(-49.42, 36.48) * mm, "end": v(-50.72, 34.18) * mm});
            skLineSegment(sketch, "E248", {"start": v(-50.72, 34.18) * mm, "end": v(-51.8, 31.89) * mm});
            skLineSegment(sketch, "E249", {"start": v(-51.8, 31.89) * mm, "end": v(-52.69, 29.63) * mm});
            skLineSegment(sketch, "E250", {"start": v(-52.69, 29.63) * mm, "end": v(-53.36, 27.46) * mm});
            skLineSegment(sketch, "E251", {"start": v(-53.36, 27.46) * mm, "end": v(-53.84, 25.39) * mm});
            skLineSegment(sketch, "E252", {"start": v(-53.84, 25.39) * mm, "end": v(-54.17, 23.44) * mm});
            skLineSegment(sketch, "E253", {"start": v(-54.17, 23.44) * mm, "end": v(-54.37, 21.63) * mm});
            skLineSegment(sketch, "E254", {"start": v(-54.37, 21.63) * mm, "end": v(-54.47, 19.98) * mm});
            skLineSegment(sketch, "E255", {"start": v(-54.47, 19.98) * mm, "end": v(-54.5, 18.51) * mm});
            skLineSegment(sketch, "E256", {"start": v(-54.5, 18.51) * mm, "end": v(-54.48, 17.24) * mm});
            skLineSegment(sketch, "E257", {"start": v(-54.48, 17.24) * mm, "end": v(-54.44, 16.19) * mm});
            skLineSegment(sketch, "E258", {"start": v(-54.44, 16.19) * mm, "end": v(-54.4, 15.35) * mm});
            skLineSegment(sketch, "E259", {"start": v(-54.4, 15.35) * mm, "end": v(-54.38, 14.7) * mm});
            skLineSegment(sketch, "E260", {"start": v(-54.38, 14.7) * mm, "end": v(-54.34, 14.18) * mm});
            skLineSegment(sketch, "E261", {"start": v(-54.34, 14.18) * mm, "end": v(-54.3, 13.74) * mm});
            skLineSegment(sketch, "E262", {"start": v(-54.3, 13.74) * mm, "end": v(-54.23, 13.31) * mm});
            skLineSegment(sketch, "E263", {"start": v(-54.23, 13.31) * mm, "end": v(-54.14, 12.86) * mm});
            skLineSegment(sketch, "E264", {"start": v(-54.14, 12.86) * mm, "end": v(-54.02, 12.32) * mm});
            skLineSegment(sketch, "E265", {"start": v(-54.02, 12.32) * mm, "end": v(-53.87, 11.65) * mm});
            skLineSegment(sketch, "E266", {"start": v(-53.87, 11.65) * mm, "end": v(-53.67, 10.8) * mm});
            skLineSegment(sketch, "E267", {"start": v(-53.67, 10.8) * mm, "end": v(-53.42, 9.77) * mm});
            skLineSegment(sketch, "E268", {"start": v(-53.42, 9.77) * mm, "end": v(-53.12, 8.61) * mm});
            skLineSegment(sketch, "E269", {"start": v(-53.12, 8.61) * mm, "end": v(-52.78, 7.33) * mm});
            skLineSegment(sketch, "E270", {"start": v(-52.78, 7.33) * mm, "end": v(-52.39, 5.96) * mm});
            skLineSegment(sketch, "E271", {"start": v(-52.39, 5.96) * mm, "end": v(-51.94, 4.52) * mm});
            skLineSegment(sketch, "E272", {"start": v(-51.94, 4.52) * mm, "end": v(-51.44, 3.04) * mm});
            skLineSegment(sketch, "E273", {"start": v(-51.44, 3.04) * mm, "end": v(-50.89, 1.53) * mm});
            skLineSegment(sketch, "E274", {"start": v(-50.89, 1.53) * mm, "end": v(-50.28, 0.03) * mm});
            skLineSegment(sketch, "E275", {"start": v(-50.28, 0.03) * mm, "end": v(-49.61, -1.47) * mm});
            skLineSegment(sketch, "E276", {"start": v(-49.61, -1.47) * mm, "end": v(-48.9, -2.96) * mm});
            skLineSegment(sketch, "E277", {"start": v(-48.9, -2.96) * mm, "end": v(-48.14, -4.44) * mm});
            skLineSegment(sketch, "E278", {"start": v(-48.14, -4.44) * mm, "end": v(-47.33, -5.9) * mm});
            skLineSegment(sketch, "E279", {"start": v(-47.33, -5.9) * mm, "end": v(-46.5, -7.37) * mm});
            skLineSegment(sketch, "E280", {"start": v(-46.5, -7.37) * mm, "end": v(-45.6, -8.81) * mm});
            skLineSegment(sketch, "E281", {"start": v(-45.6, -8.81) * mm, "end": v(-44.7, -10.24) * mm});
            skLineSegment(sketch, "E282", {"start": v(-44.7, -10.24) * mm, "end": v(-43.75, -11.65) * mm});
            skLineSegment(sketch, "E283", {"start": v(-43.75, -11.65) * mm, "end": v(-42.78, -13.05) * mm});
            skLineSegment(sketch, "E284", {"start": v(-42.78, -13.05) * mm, "end": v(-41.8, -14.42) * mm});
            skLineSegment(sketch, "E285", {"start": v(-41.8, -14.42) * mm, "end": v(-40.8, -15.78) * mm});
            skLineSegment(sketch, "E286", {"start": v(-40.8, -15.78) * mm, "end": v(-39.8, -17.1) * mm});
            skLineSegment(sketch, "E287", {"start": v(-39.8, -17.1) * mm, "end": v(-38.79, -18.41) * mm});
            skLineSegment(sketch, "E288", {"start": v(-38.79, -18.41) * mm, "end": v(-37.79, -19.7) * mm});
            skLineSegment(sketch, "E289", {"start": v(-37.79, -19.7) * mm, "end": v(-36.8, -20.94) * mm});
            skLineSegment(sketch, "E290", {"start": v(-36.8, -20.94) * mm, "end": v(-35.82, -22.16) * mm});
            skLineSegment(sketch, "E291", {"start": v(-35.82, -22.16) * mm, "end": v(-34.85, -23.35) * mm});
            skLineSegment(sketch, "E292", {"start": v(-34.85, -23.35) * mm, "end": v(-33.9, -24.52) * mm});
            skLineSegment(sketch, "E293", {"start": v(-33.9, -24.52) * mm, "end": v(-32.95, -25.65) * mm});
            skLineSegment(sketch, "E294", {"start": v(-32.95, -25.65) * mm, "end": v(-32, -26.76) * mm});
            skLineSegment(sketch, "E295", {"start": v(-32, -26.76) * mm, "end": v(-31.06, -27.85) * mm});
            skLineSegment(sketch, "E296", {"start": v(-31.06, -27.85) * mm, "end": v(-30.11, -28.91) * mm});
            skLineSegment(sketch, "E297", {"start": v(-30.11, -28.91) * mm, "end": v(-29.16, -29.95) * mm});
            skLineSegment(sketch, "E298", {"start": v(-29.16, -29.95) * mm, "end": v(-28.19, -30.97) * mm});
            skLineSegment(sketch, "E299", {"start": v(-28.19, -30.97) * mm, "end": v(-27.2, -31.96) * mm});
            skLineSegment(sketch, "E300", {"start": v(-27.2, -31.96) * mm, "end": v(-26.22, -32.94) * mm});
            skLineSegment(sketch, "E301", {"start": v(-26.22, -32.94) * mm, "end": v(-25.22, -33.9) * mm});
            skLineSegment(sketch, "E302", {"start": v(-25.22, -33.9) * mm, "end": v(-24.2, -34.84) * mm});
            skLineSegment(sketch, "E303", {"start": v(-24.2, -34.84) * mm, "end": v(-23.19, -35.76) * mm});
            skLineSegment(sketch, "E304", {"start": v(-23.19, -35.76) * mm, "end": v(-22.15, -36.67) * mm});
            skLineSegment(sketch, "E305", {"start": v(-22.15, -36.67) * mm, "end": v(-21.1, -37.56) * mm});
            skLineSegment(sketch, "E306", {"start": v(-21.1, -37.56) * mm, "end": v(-20.05, -38.44) * mm});
            skLineSegment(sketch, "E307", {"start": v(-20.05, -38.44) * mm, "end": v(-18.99, -39.3) * mm});
            skLineSegment(sketch, "E308", {"start": v(-18.99, -39.3) * mm, "end": v(-17.92, -40.15) * mm});
            skLineSegment(sketch, "E309", {"start": v(-17.92, -40.15) * mm, "end": v(-16.84, -40.98) * mm});
            skLineSegment(sketch, "E310", {"start": v(-16.84, -40.98) * mm, "end": v(-15.76, -41.79) * mm});
            skLineSegment(sketch, "E311", {"start": v(-15.76, -41.79) * mm, "end": v(-14.68, -42.57) * mm});
            skLineSegment(sketch, "E312", {"start": v(-14.68, -42.57) * mm, "end": v(-13.6, -43.34) * mm});
            skLineSegment(sketch, "E313", {"start": v(-13.6, -43.34) * mm, "end": v(-12.52, -44.08) * mm});
            skLineSegment(sketch, "E314", {"start": v(-12.52, -44.08) * mm, "end": v(-11.44, -44.8) * mm});
            skLineSegment(sketch, "E315", {"start": v(-11.44, -44.8) * mm, "end": v(-10.38, -45.48) * mm});
            skLineSegment(sketch, "E316", {"start": v(-10.38, -45.48) * mm, "end": v(-9.34, -46.13) * mm});
            skLineSegment(sketch, "E317", {"start": v(-9.34, -46.13) * mm, "end": v(-8.32, -46.74) * mm});
            skLineSegment(sketch, "E318", {"start": v(-8.32, -46.74) * mm, "end": v(-7.35, -47.3) * mm});
            skLineSegment(sketch, "E319", {"start": v(-7.35, -47.3) * mm, "end": v(-6.43, -47.83) * mm});
            skLineSegment(sketch, "E320", {"start": v(-6.43, -47.83) * mm, "end": v(-5.56, -48.3) * mm});
            skLineSegment(sketch, "E321", {"start": v(-5.56, -48.3) * mm, "end": v(-4.76, -48.72) * mm});
            skLineSegment(sketch, "E322", {"start": v(-4.76, -48.72) * mm, "end": v(-4.04, -49.08) * mm});
            skLineSegment(sketch, "E323", {"start": v(-4.04, -49.08) * mm, "end": v(-3.4, -49.39) * mm});
            skLineSegment(sketch, "E324", {"start": v(-3.4, -49.39) * mm, "end": v(-2.85, -49.65) * mm});
            skLineSegment(sketch, "E325", {"start": v(-2.85, -49.65) * mm, "end": v(-2.35, -49.86) * mm});
            skLineSegment(sketch, "E326", {"start": v(-2.35, -49.86) * mm, "end": v(-1.9, -50.04) * mm});
            skLineSegment(sketch, "E327", {"start": v(-1.9, -50.04) * mm, "end": v(-1.47, -50.17) * mm});
            skLineSegment(sketch, "E328", {"start": v(-1.47, -50.17) * mm, "end": v(-1.06, -50.27) * mm});
            skLineSegment(sketch, "E329", {"start": v(-1.06, -50.27) * mm, "end": v(-0.64, -50.34) * mm});
            skLineSegment(sketch, "E330", {"start": v(-0.64, -50.34) * mm, "end": v(0, -50.44) * mm});
            skLineSegment(sketch, "E331", {"start": v(0, -50.44) * mm, "end": v(0.64, -50.34) * mm});
            skLineSegment(sketch, "E332", {"start": v(0.64, -50.34) * mm, "end": v(1.06, -50.27) * mm});
            skLineSegment(sketch, "E333", {"start": v(1.06, -50.27) * mm, "end": v(1.47, -50.17) * mm});
            skLineSegment(sketch, "E334", {"start": v(1.47, -50.17) * mm, "end": v(1.9, -50.04) * mm});
            skLineSegment(sketch, "E335", {"start": v(1.9, -50.04) * mm, "end": v(2.35, -49.86) * mm});
            skLineSegment(sketch, "E336", {"start": v(2.35, -49.86) * mm, "end": v(2.85, -49.65) * mm});
            skLineSegment(sketch, "E337", {"start": v(2.85, -49.65) * mm, "end": v(3.4, -49.39) * mm});
            skLineSegment(sketch, "E338", {"start": v(3.4, -49.39) * mm, "end": v(4.04, -49.08) * mm});
            skLineSegment(sketch, "E339", {"start": v(4.04, -49.08) * mm, "end": v(4.76, -48.72) * mm});
            skLineSegment(sketch, "E340", {"start": v(4.76, -48.72) * mm, "end": v(5.56, -48.3) * mm});
            skLineSegment(sketch, "E341", {"start": v(5.56, -48.3) * mm, "end": v(6.43, -47.83) * mm});
            skLineSegment(sketch, "E342", {"start": v(6.43, -47.83) * mm, "end": v(7.35, -47.3) * mm});
            skLineSegment(sketch, "E343", {"start": v(7.35, -47.3) * mm, "end": v(8.32, -46.74) * mm});
            skLineSegment(sketch, "E344", {"start": v(8.32, -46.74) * mm, "end": v(9.34, -46.13) * mm});
            skLineSegment(sketch, "E345", {"start": v(9.34, -46.13) * mm, "end": v(10.38, -45.48) * mm});
            skLineSegment(sketch, "E346", {"start": v(10.38, -45.48) * mm, "end": v(11.44, -44.8) * mm});
            skLineSegment(sketch, "E347", {"start": v(11.44, -44.8) * mm, "end": v(12.52, -44.08) * mm});
            skLineSegment(sketch, "E348", {"start": v(12.52, -44.08) * mm, "end": v(13.6, -43.34) * mm});
            skLineSegment(sketch, "E349", {"start": v(13.6, -43.34) * mm, "end": v(14.68, -42.57) * mm});
            skLineSegment(sketch, "E350", {"start": v(14.68, -42.57) * mm, "end": v(15.76, -41.79) * mm});
            skLineSegment(sketch, "E351", {"start": v(15.76, -41.79) * mm, "end": v(16.84, -40.98) * mm});
            skLineSegment(sketch, "E352", {"start": v(16.84, -40.98) * mm, "end": v(17.92, -40.15) * mm});
            skLineSegment(sketch, "E353", {"start": v(17.92, -40.15) * mm, "end": v(18.99, -39.3) * mm});
            skLineSegment(sketch, "E354", {"start": v(18.99, -39.3) * mm, "end": v(20.05, -38.44) * mm});
            skLineSegment(sketch, "E355", {"start": v(20.05, -38.44) * mm, "end": v(21.1, -37.56) * mm});
            skLineSegment(sketch, "E356", {"start": v(21.1, -37.56) * mm, "end": v(22.15, -36.67) * mm});
            skLineSegment(sketch, "E357", {"start": v(22.15, -36.67) * mm, "end": v(23.19, -35.76) * mm});
            skLineSegment(sketch, "E358", {"start": v(23.19, -35.76) * mm, "end": v(24.2, -34.84) * mm});
            skLineSegment(sketch, "E359", {"start": v(24.2, -34.84) * mm, "end": v(25.22, -33.9) * mm});
            skLineSegment(sketch, "E360", {"start": v(25.22, -33.9) * mm, "end": v(26.22, -32.94) * mm});
            skLineSegment(sketch, "E361", {"start": v(26.22, -32.94) * mm, "end": v(27.2, -31.96) * mm});
            skLineSegment(sketch, "E362", {"start": v(27.2, -31.96) * mm, "end": v(28.19, -30.97) * mm});
            skLineSegment(sketch, "E363", {"start": v(28.19, -30.97) * mm, "end": v(29.15, -29.95) * mm});
            skLineSegment(sketch, "E364", {"start": v(29.15, -29.95) * mm, "end": v(30.11, -28.91) * mm});
            skLineSegment(sketch, "E365", {"start": v(30.11, -28.91) * mm, "end": v(31.06, -27.85) * mm});
            skLineSegment(sketch, "E366", {"start": v(31.06, -27.85) * mm, "end": v(32, -26.76) * mm});
            skLineSegment(sketch, "E367", {"start": v(32, -26.76) * mm, "end": v(32.95, -25.65) * mm});
            skLineSegment(sketch, "E368", {"start": v(32.95, -25.65) * mm, "end": v(33.9, -24.52) * mm});
            skLineSegment(sketch, "E369", {"start": v(33.9, -24.52) * mm, "end": v(34.85, -23.35) * mm});
            skLineSegment(sketch, "E370", {"start": v(34.85, -23.35) * mm, "end": v(35.82, -22.16) * mm});
            skLineSegment(sketch, "E371", {"start": v(35.82, -22.16) * mm, "end": v(36.8, -20.94) * mm});
            skLineSegment(sketch, "E372", {"start": v(36.8, -20.94) * mm, "end": v(37.79, -19.7) * mm});
            skLineSegment(sketch, "E373", {"start": v(37.79, -19.7) * mm, "end": v(38.79, -18.41) * mm});
            skLineSegment(sketch, "E374", {"start": v(38.79, -18.41) * mm, "end": v(39.8, -17.1) * mm});
            skLineSegment(sketch, "E375", {"start": v(39.8, -17.1) * mm, "end": v(40.8, -15.78) * mm});
            skLineSegment(sketch, "E376", {"start": v(40.8, -15.78) * mm, "end": v(41.8, -14.42) * mm});
            skLineSegment(sketch, "E377", {"start": v(41.8, -14.42) * mm, "end": v(42.78, -13.05) * mm});
            skLineSegment(sketch, "E378", {"start": v(42.78, -13.05) * mm, "end": v(43.75, -11.65) * mm});
            skLineSegment(sketch, "E379", {"start": v(43.75, -11.65) * mm, "end": v(44.7, -10.24) * mm});
            skLineSegment(sketch, "E380", {"start": v(44.7, -10.24) * mm, "end": v(45.6, -8.81) * mm});
            skLineSegment(sketch, "E381", {"start": v(45.6, -8.81) * mm, "end": v(46.5, -7.37) * mm});
            skLineSegment(sketch, "E382", {"start": v(46.5, -7.37) * mm, "end": v(47.33, -5.9) * mm});
            skLineSegment(sketch, "E383", {"start": v(47.33, -5.9) * mm, "end": v(48.14, -4.44) * mm});
            skLineSegment(sketch, "E384", {"start": v(48.14, -4.44) * mm, "end": v(48.9, -2.96) * mm});
            skLineSegment(sketch, "E385", {"start": v(48.9, -2.96) * mm, "end": v(49.61, -1.47) * mm});
            skLineSegment(sketch, "E386", {"start": v(49.61, -1.47) * mm, "end": v(50.28, 0.03) * mm});
            skLineSegment(sketch, "E387", {"start": v(50.28, 0.03) * mm, "end": v(50.89, 1.53) * mm});
            skLineSegment(sketch, "E388", {"start": v(50.89, 1.53) * mm, "end": v(51.44, 3.04) * mm});
            skLineSegment(sketch, "E389", {"start": v(51.44, 3.04) * mm, "end": v(51.94, 4.52) * mm});
            skLineSegment(sketch, "E390", {"start": v(51.94, 4.52) * mm, "end": v(52.39, 5.96) * mm});
            skLineSegment(sketch, "E391", {"start": v(52.39, 5.96) * mm, "end": v(52.78, 7.33) * mm});
            skLineSegment(sketch, "E392", {"start": v(52.78, 7.33) * mm, "end": v(53.12, 8.61) * mm});
            skLineSegment(sketch, "E393", {"start": v(53.12, 8.61) * mm, "end": v(53.42, 9.77) * mm});
            skLineSegment(sketch, "E394", {"start": v(53.42, 9.77) * mm, "end": v(53.67, 10.8) * mm});
            skLineSegment(sketch, "E395", {"start": v(53.67, 10.8) * mm, "end": v(53.87, 11.65) * mm});
            skLineSegment(sketch, "E396", {"start": v(53.87, 11.65) * mm, "end": v(54.02, 12.32) * mm});
            skLineSegment(sketch, "E397", {"start": v(54.02, 12.32) * mm, "end": v(54.14, 12.86) * mm});
            skLineSegment(sketch, "E398", {"start": v(54.14, 12.86) * mm, "end": v(54.23, 13.31) * mm});
            skLineSegment(sketch, "E399", {"start": v(54.23, 13.31) * mm, "end": v(54.3, 13.74) * mm});
            skLineSegment(sketch, "E400", {"start": v(54.3, 13.74) * mm, "end": v(54.34, 14.18) * mm});
            skLineSegment(sketch, "E401", {"start": v(54.34, 14.18) * mm, "end": v(54.38, 14.7) * mm});
            skLineSegment(sketch, "E402", {"start": v(54.38, 14.7) * mm, "end": v(54.4, 15.35) * mm});
            skLineSegment(sketch, "E403", {"start": v(54.4, 15.35) * mm, "end": v(54.44, 16.19) * mm});
            skLineSegment(sketch, "E404", {"start": v(54.44, 16.19) * mm, "end": v(54.48, 17.24) * mm});
            skLineSegment(sketch, "E405", {"start": v(54.48, 17.24) * mm, "end": v(54.5, 18.51) * mm});
            skLineSegment(sketch, "E406", {"start": v(54.5, 18.51) * mm, "end": v(54.47, 19.98) * mm});
            skLineSegment(sketch, "E407", {"start": v(54.47, 19.98) * mm, "end": v(54.37, 21.63) * mm});
            skLineSegment(sketch, "E408", {"start": v(54.37, 21.63) * mm, "end": v(54.17, 23.44) * mm});
            skLineSegment(sketch, "E409", {"start": v(54.17, 23.44) * mm, "end": v(53.84, 25.39) * mm});
            skLineSegment(sketch, "E410", {"start": v(53.84, 25.39) * mm, "end": v(53.36, 27.46) * mm});
            skLineSegment(sketch, "E411", {"start": v(53.36, 27.46) * mm, "end": v(52.69, 29.63) * mm});
            skLineSegment(sketch, "E412", {"start": v(52.69, 29.63) * mm, "end": v(51.8, 31.89) * mm});
            skLineSegment(sketch, "E413", {"start": v(51.8, 31.89) * mm, "end": v(50.72, 34.18) * mm});
            skLineSegment(sketch, "E414", {"start": v(50.72, 34.18) * mm, "end": v(49.42, 36.48) * mm});
            skLineSegment(sketch, "E415", {"start": v(49.42, 36.48) * mm, "end": v(47.9, 38.72) * mm});
            skLineSegment(sketch, "E416", {"start": v(47.9, 38.72) * mm, "end": v(46.17, 40.88) * mm});
            skLineSegment(sketch, "E417", {"start": v(46.17, 40.88) * mm, "end": v(44.23, 42.9) * mm});
            skLineSegment(sketch, "E418", {"start": v(44.23, 42.9) * mm, "end": v(42.07, 44.74) * mm});
            skLineSegment(sketch, "E419", {"start": v(42.07, 44.74) * mm, "end": v(39.7, 46.35) * mm});
            skLineSegment(sketch, "E420", {"start": v(39.7, 46.35) * mm, "end": v(37.11, 47.71) * mm});
            skLineSegment(sketch, "E421", {"start": v(37.11, 47.71) * mm, "end": v(34.37, 48.8) * mm});
            skLineSegment(sketch, "E422", {"start": v(34.37, 48.8) * mm, "end": v(31.5, 49.62) * mm});
            skLineSegment(sketch, "E423", {"start": v(31.5, 49.62) * mm, "end": v(28.57, 50.17) * mm});
            skLineSegment(sketch, "E424", {"start": v(28.57, 50.17) * mm, "end": v(25.63, 50.44) * mm});
            skLineSegment(sketch, "E425", {"start": v(25.63, 50.44) * mm, "end": v(22.71, 50.44) * mm});
            skLineSegment(sketch, "E426", {"start": v(22.71, 50.44) * mm, "end": v(19.89, 50.15) * mm});
            skLineSegment(sketch, "E427", {"start": v(19.89, 50.15) * mm, "end": v(17.2, 49.59) * mm});
            skLineSegment(sketch, "E428", {"start": v(17.2, 49.59) * mm, "end": v(14.68, 48.75) * mm});
            skLineSegment(sketch, "E429", {"start": v(14.68, 48.75) * mm, "end": v(12.35, 47.7) * mm});
            skLineSegment(sketch, "E430", {"start": v(12.35, 47.7) * mm, "end": v(10.21, 46.49) * mm});
            skLineSegment(sketch, "E431", {"start": v(10.21, 46.49) * mm, "end": v(8.27, 45.2) * mm});
            skLineSegment(sketch, "E432", {"start": v(8.27, 45.2) * mm, "end": v(6.53, 43.88) * mm});
            skLineSegment(sketch, "E433", {"start": v(6.53, 43.88) * mm, "end": v(5, 42.6) * mm});
            skLineSegment(sketch, "E434", {"start": v(5, 42.6) * mm, "end": v(3.68, 41.44) * mm});
            skLineSegment(sketch, "E435", {"start": v(3.68, 41.44) * mm, "end": v(2.57, 40.45) * mm});
            skLineSegment(sketch, "E436", {"start": v(2.57, 40.45) * mm, "end": v(2.1, 40.05) * mm});
            skLineSegment(sketch, "E437", {"start": v(2.1, 40.05) * mm, "end": v(1.68, 39.7) * mm});
            skLineSegment(sketch, "E438", {"start": v(1.68, 39.7) * mm, "end": v(1.31, 39.4) * mm});
            skLineSegment(sketch, "E439", {"start": v(1.31, 39.4) * mm, "end": v(0.98, 39.15) * mm});
            skLineSegment(sketch, "E440", {"start": v(0.98, 39.15) * mm, "end": v(0.69, 38.95) * mm});
            skLineSegment(sketch, "E441", {"start": v(0.69, 38.95) * mm, "end": v(0.43, 38.78) * mm});
            skLineSegment(sketch, "E442", {"start": v(0.43, 38.78) * mm, "end": v(0.2, 38.66) * mm});
            skLineSegment(sketch, "E443", {"start": v(0.2, 38.66) * mm, "end": v(0, 38.57) * mm});
            skLineSegment(sketch, "E444", {"start": v(0, 38.57) * mm, "end": v(-0.2, 38.66) * mm});
            skLineSegment(sketch, "E445", {"start": v(-0.2, 38.66) * mm, "end": v(-0.43, 38.78) * mm});
            skLineSegment(sketch, "E446", {"start": v(-0.43, 38.78) * mm, "end": v(-0.69, 38.95) * mm});
            skLineSegment(sketch, "E447", {"start": v(-0.69, 38.95) * mm, "end": v(-0.98, 39.15) * mm});
            skLineSegment(sketch, "E448", {"start": v(-0.98, 39.15) * mm, "end": v(-1.31, 39.4) * mm});
            skLineSegment(sketch, "E449", {"start": v(-1.31, 39.4) * mm, "end": v(-1.68, 39.7) * mm});
            skLineSegment(sketch, "E450", {"start": v(-1.68, 39.7) * mm, "end": v(-2.1, 40.05) * mm});
            skLineSegment(sketch, "E451", {"start": v(-2.1, 40.05) * mm, "end": v(-2.57, 40.45) * mm});
            skLineSegment(sketch, "E452", {"start": v(0, -47.87) * mm, "end": v(0.31, -47.82) * mm});
            skLineSegment(sketch, "E453", {"start": v(0.31, -47.82) * mm, "end": v(0.7, -47.75) * mm});
            skLineSegment(sketch, "E454", {"start": v(0.7, -47.75) * mm, "end": v(1.12, -47.62) * mm});
            skLineSegment(sketch, "E455", {"start": v(1.12, -47.62) * mm, "end": v(1.56, -47.45) * mm});
            skLineSegment(sketch, "E456", {"start": v(1.56, -47.45) * mm, "end": v(2, -47.25) * mm});
            skLineSegment(sketch, "E457", {"start": v(2, -47.25) * mm, "end": v(2.44, -47.04) * mm});
            skLineSegment(sketch, "E458", {"start": v(2.44, -47.04) * mm, "end": v(2.86, -46.83) * mm});
            skLineSegment(sketch, "E459", {"start": v(2.86, -46.83) * mm, "end": v(3.26, -46.63) * mm});
            skLineSegment(sketch, "E460", {"start": v(3.26, -46.63) * mm, "end": v(3.61, -46.45) * mm});
            skLineSegment(sketch, "E461", {"start": v(3.61, -46.45) * mm, "end": v(4.57, -45.95) * mm});
            skLineSegment(sketch, "E462", {"start": v(4.57, -45.95) * mm, "end": v(5.53, -45.43) * mm});
            skLineSegment(sketch, "E463", {"start": v(5.53, -45.43) * mm, "end": v(6.48, -44.89) * mm});
            skLineSegment(sketch, "E464", {"start": v(6.48, -44.89) * mm, "end": v(7.42, -44.33) * mm});
            skLineSegment(sketch, "E465", {"start": v(7.42, -44.33) * mm, "end": v(8.36, -43.75) * mm});
            skLineSegment(sketch, "E466", {"start": v(8.36, -43.75) * mm, "end": v(9.28, -43.17) * mm});
            skLineSegment(sketch, "E467", {"start": v(9.28, -43.17) * mm, "end": v(10.2, -42.57) * mm});
            skLineSegment(sketch, "E468", {"start": v(10.2, -42.57) * mm, "end": v(11.1, -41.97) * mm});
            skLineSegment(sketch, "E469", {"start": v(11.1, -41.97) * mm, "end": v(12.18, -41.23) * mm});
            skLineSegment(sketch, "E470", {"start": v(12.18, -41.23) * mm, "end": v(13.25, -40.47) * mm});
            skLineSegment(sketch, "E471", {"start": v(13.25, -40.47) * mm, "end": v(14.32, -39.7) * mm});
            skLineSegment(sketch, "E472", {"start": v(14.32, -39.7) * mm, "end": v(15.37, -38.9) * mm});
            skLineSegment(sketch, "E473", {"start": v(15.37, -38.9) * mm, "end": v(16.4, -38.1) * mm});
            skLineSegment(sketch, "E474", {"start": v(16.4, -38.1) * mm, "end": v(17.44, -37.29) * mm});
            skLineSegment(sketch, "E475", {"start": v(17.44, -37.29) * mm, "end": v(18.46, -36.46) * mm});
            skLineSegment(sketch, "E476", {"start": v(18.46, -36.46) * mm, "end": v(19.47, -35.62) * mm});
            skLineSegment(sketch, "E477", {"start": v(19.47, -35.62) * mm, "end": v(20.5, -34.74) * mm});
            skLineSegment(sketch, "E478", {"start": v(20.5, -34.74) * mm, "end": v(21.5, -33.85) * mm});
            skLineSegment(sketch, "E479", {"start": v(21.5, -33.85) * mm, "end": v(22.5, -32.95) * mm});
            skLineSegment(sketch, "E480", {"start": v(22.5, -32.95) * mm, "end": v(23.5, -32.03) * mm});
            skLineSegment(sketch, "E481", {"start": v(23.5, -32.03) * mm, "end": v(24.47, -31.1) * mm});
            skLineSegment(sketch, "E482", {"start": v(24.47, -31.1) * mm, "end": v(25.43, -30.15) * mm});
            skLineSegment(sketch, "E483", {"start": v(25.43, -30.15) * mm, "end": v(26.37, -29.2) * mm});
            skLineSegment(sketch, "E484", {"start": v(26.37, -29.2) * mm, "end": v(27.3, -28.21) * mm});
            skLineSegment(sketch, "E485", {"start": v(27.3, -28.21) * mm, "end": v(28.28, -27.15) * mm});
            skLineSegment(sketch, "E486", {"start": v(28.28, -27.15) * mm, "end": v(29.25, -26.06) * mm});
            skLineSegment(sketch, "E487", {"start": v(29.25, -26.06) * mm, "end": v(30.2, -24.97) * mm});
            skLineSegment(sketch, "E488", {"start": v(30.2, -24.97) * mm, "end": v(31.14, -23.86) * mm});
            skLineSegment(sketch, "E489", {"start": v(31.14, -23.86) * mm, "end": v(32.07, -22.74) * mm});
            skLineSegment(sketch, "E490", {"start": v(32.07, -22.74) * mm, "end": v(33, -21.62) * mm});
            skLineSegment(sketch, "E491", {"start": v(33, -21.62) * mm, "end": v(33.9, -20.5) * mm});
            skLineSegment(sketch, "E492", {"start": v(33.9, -20.5) * mm, "end": v(34.8, -19.36) * mm});
            skLineSegment(sketch, "E493", {"start": v(34.8, -19.36) * mm, "end": v(35.82, -18.08) * mm});
            skLineSegment(sketch, "E494", {"start": v(35.82, -18.08) * mm, "end": v(36.83, -16.8) * mm});
            skLineSegment(sketch, "E495", {"start": v(36.83, -16.8) * mm, "end": v(37.83, -15.5) * mm});
            skLineSegment(sketch, "E496", {"start": v(37.83, -15.5) * mm, "end": v(38.81, -14.2) * mm});
            skLineSegment(sketch, "E497", {"start": v(38.81, -14.2) * mm, "end": v(39.78, -12.88) * mm});
            skLineSegment(sketch, "E498", {"start": v(39.78, -12.88) * mm, "end": v(40.73, -11.55) * mm});
            skLineSegment(sketch, "E499", {"start": v(40.73, -11.55) * mm, "end": v(41.66, -10.2) * mm});
            skLineSegment(sketch, "E500", {"start": v(41.66, -10.2) * mm, "end": v(42.57, -8.85) * mm});
            skLineSegment(sketch, "E501", {"start": v(42.57, -8.85) * mm, "end": v(43.43, -7.5) * mm});
            skLineSegment(sketch, "E502", {"start": v(43.43, -7.5) * mm, "end": v(44.26, -6.14) * mm});
            skLineSegment(sketch, "E503", {"start": v(44.26, -6.14) * mm, "end": v(45.07, -4.76) * mm});
            skLineSegment(sketch, "E504", {"start": v(45.07, -4.76) * mm, "end": v(45.84, -3.35) * mm});
            skLineSegment(sketch, "E505", {"start": v(45.84, -3.35) * mm, "end": v(46.57, -1.93) * mm});
            skLineSegment(sketch, "E506", {"start": v(46.57, -1.93) * mm, "end": v(47.27, -0.49) * mm});
            skLineSegment(sketch, "E507", {"start": v(47.27, -0.49) * mm, "end": v(47.92, 0.97) * mm});
            skLineSegment(sketch, "E508", {"start": v(47.92, 0.97) * mm, "end": v(48.52, 2.45) * mm});
            skLineSegment(sketch, "E509", {"start": v(48.52, 2.45) * mm, "end": v(48.96, 3.65) * mm});
            skLineSegment(sketch, "E510", {"start": v(48.96, 3.65) * mm, "end": v(49.38, 4.85) * mm});
            skLineSegment(sketch, "E511", {"start": v(49.38, 4.85) * mm, "end": v(49.76, 6.07) * mm});
            skLineSegment(sketch, "E512", {"start": v(49.76, 6.07) * mm, "end": v(50.13, 7.29) * mm});
            skLineSegment(sketch, "E513", {"start": v(50.13, 7.29) * mm, "end": v(50.47, 8.51) * mm});
            skLineSegment(sketch, "E514", {"start": v(50.47, 8.51) * mm, "end": v(50.8, 9.74) * mm});
            skLineSegment(sketch, "E515", {"start": v(50.8, 9.74) * mm, "end": v(51.1, 10.98) * mm});
            skLineSegment(sketch, "E516", {"start": v(51.1, 10.98) * mm, "end": v(51.4, 12.22) * mm});
            skLineSegment(sketch, "E517", {"start": v(51.4, 12.22) * mm, "end": v(51.5, 12.65) * mm});
            skLineSegment(sketch, "E518", {"start": v(51.5, 12.65) * mm, "end": v(51.6, 13.08) * mm});
            skLineSegment(sketch, "E519", {"start": v(51.6, 13.08) * mm, "end": v(51.69, 13.52) * mm});
            skLineSegment(sketch, "E520", {"start": v(51.69, 13.52) * mm, "end": v(51.76, 13.95) * mm});
            skLineSegment(sketch, "E521", {"start": v(51.76, 13.95) * mm, "end": v(51.82, 14.52) * mm});
            skLineSegment(sketch, "E522", {"start": v(51.82, 14.52) * mm, "end": v(51.86, 15.11) * mm});
            skLineSegment(sketch, "E523", {"start": v(51.86, 15.11) * mm, "end": v(51.88, 15.7) * mm});
            skLineSegment(sketch, "E524", {"start": v(51.88, 15.7) * mm, "end": v(51.9, 16.29) * mm});
            skLineSegment(sketch, "E525", {"start": v(51.9, 16.29) * mm, "end": v(51.95, 17.92) * mm});
            skLineSegment(sketch, "E526", {"start": v(51.95, 17.92) * mm, "end": v(51.93, 19.51) * mm});
            skLineSegment(sketch, "E527", {"start": v(51.93, 19.51) * mm, "end": v(51.86, 21.07) * mm});
            skLineSegment(sketch, "E528", {"start": v(51.86, 21.07) * mm, "end": v(51.71, 22.61) * mm});
            skLineSegment(sketch, "E529", {"start": v(51.71, 22.61) * mm, "end": v(51.5, 24.15) * mm});
            skLineSegment(sketch, "E530", {"start": v(51.5, 24.15) * mm, "end": v(51.18, 25.68) * mm});
            skLineSegment(sketch, "E531", {"start": v(51.18, 25.68) * mm, "end": v(50.79, 27.23) * mm});
            skLineSegment(sketch, "E532", {"start": v(50.79, 27.23) * mm, "end": v(50.29, 28.8) * mm});
            skLineSegment(sketch, "E533", {"start": v(50.29, 28.8) * mm, "end": v(49.4, 31.07) * mm});
            skLineSegment(sketch, "E534", {"start": v(49.4, 31.07) * mm, "end": v(48.32, 33.3) * mm});
            skLineSegment(sketch, "E535", {"start": v(48.32, 33.3) * mm, "end": v(47.06, 35.46) * mm});
            skLineSegment(sketch, "E536", {"start": v(47.06, 35.46) * mm, "end": v(45.63, 37.51) * mm});
            skLineSegment(sketch, "E537", {"start": v(45.63, 37.51) * mm, "end": v(44.04, 39.44) * mm});
            skLineSegment(sketch, "E538", {"start": v(44.04, 39.44) * mm, "end": v(42.3, 41.22) * mm});
            skLineSegment(sketch, "E539", {"start": v(42.3, 41.22) * mm, "end": v(40.41, 42.8) * mm});
            skLineSegment(sketch, "E540", {"start": v(40.41, 42.8) * mm, "end": v(38.39, 44.18) * mm});
            skLineSegment(sketch, "E541", {"start": v(38.39, 44.18) * mm, "end": v(36.1, 45.38) * mm});
            skLineSegment(sketch, "E542", {"start": v(36.1, 45.38) * mm, "end": v(33.65, 46.36) * mm});
            skLineSegment(sketch, "E543", {"start": v(33.65, 46.36) * mm, "end": v(31.06, 47.12) * mm});
            skLineSegment(sketch, "E544", {"start": v(31.06, 47.12) * mm, "end": v(28.4, 47.63) * mm});
            skLineSegment(sketch, "E545", {"start": v(28.4, 47.63) * mm, "end": v(25.7, 47.9) * mm});
            skLineSegment(sketch, "E546", {"start": v(25.7, 47.9) * mm, "end": v(23, 47.91) * mm});
            skLineSegment(sketch, "E547", {"start": v(23, 47.91) * mm, "end": v(20.38, 47.66) * mm});
            skLineSegment(sketch, "E548", {"start": v(20.38, 47.66) * mm, "end": v(17.86, 47.14) * mm});
            skLineSegment(sketch, "E549", {"start": v(17.86, 47.14) * mm, "end": v(16.77, 46.8) * mm});
            skLineSegment(sketch, "E550", {"start": v(16.77, 46.8) * mm, "end": v(15.7, 46.42) * mm});
            skLineSegment(sketch, "E551", {"start": v(15.7, 46.42) * mm, "end": v(14.65, 45.98) * mm});
            skLineSegment(sketch, "E552", {"start": v(14.65, 45.98) * mm, "end": v(13.63, 45.5) * mm});
            skLineSegment(sketch, "E553", {"start": v(13.63, 45.5) * mm, "end": v(12.62, 44.96) * mm});
            skLineSegment(sketch, "E554", {"start": v(12.62, 44.96) * mm, "end": v(11.64, 44.39) * mm});
            skLineSegment(sketch, "E555", {"start": v(11.64, 44.39) * mm, "end": v(10.69, 43.78) * mm});
            skLineSegment(sketch, "E556", {"start": v(10.69, 43.78) * mm, "end": v(9.75, 43.13) * mm});
            skLineSegment(sketch, "E557", {"start": v(9.75, 43.13) * mm, "end": v(9.02, 42.6) * mm});
            skLineSegment(sketch, "E558", {"start": v(9.02, 42.6) * mm, "end": v(8.3, 42.04) * mm});
            skLineSegment(sketch, "E559", {"start": v(8.3, 42.04) * mm, "end": v(7.62, 41.48) * mm});
            skLineSegment(sketch, "E560", {"start": v(7.62, 41.48) * mm, "end": v(6.94, 40.9) * mm});
            skLineSegment(sketch, "E561", {"start": v(6.94, 40.9) * mm, "end": v(6.26, 40.32) * mm});
            skLineSegment(sketch, "E562", {"start": v(6.26, 40.32) * mm, "end": v(5.6, 39.74) * mm});
            skLineSegment(sketch, "E563", {"start": v(5.6, 39.74) * mm, "end": v(4.92, 39.14) * mm});
            skLineSegment(sketch, "E564", {"start": v(4.92, 39.14) * mm, "end": v(4.24, 38.54) * mm});
            skLineSegment(sketch, "E565", {"start": v(4.24, 38.54) * mm, "end": v(3.88, 38.22) * mm});
            skLineSegment(sketch, "E566", {"start": v(3.88, 38.22) * mm, "end": v(3.5, 37.9) * mm});
            skLineSegment(sketch, "E567", {"start": v(3.5, 37.9) * mm, "end": v(3.08, 37.55) * mm});
            skLineSegment(sketch, "E568", {"start": v(3.08, 37.55) * mm, "end": v(2.66, 37.22) * mm});
            skLineSegment(sketch, "E569", {"start": v(2.66, 37.22) * mm, "end": v(2.22, 36.91) * mm});
            skLineSegment(sketch, "E570", {"start": v(2.22, 36.91) * mm, "end": v(1.78, 36.63) * mm});
            skLineSegment(sketch, "E571", {"start": v(1.78, 36.63) * mm, "end": v(1.33, 36.38) * mm});
            skLineSegment(sketch, "E572", {"start": v(1.33, 36.38) * mm, "end": v(0.88, 36.2) * mm});
            skLineSegment(sketch, "E573", {"start": v(0.88, 36.2) * mm, "end": v(0.66, 36.12) * mm});
            skLineSegment(sketch, "E574", {"start": v(0.66, 36.12) * mm, "end": v(0.44, 36.07) * mm});
            skLineSegment(sketch, "E575", {"start": v(0.44, 36.07) * mm, "end": v(0.22, 36.04) * mm});
            skLineSegment(sketch, "E576", {"start": v(0.22, 36.04) * mm, "end": v(0, 36.03) * mm});
            skLineSegment(sketch, "E577", {"start": v(0, 36.03) * mm, "end": v(-0.22, 36.04) * mm});
            skLineSegment(sketch, "E578", {"start": v(-0.22, 36.04) * mm, "end": v(-0.44, 36.07) * mm});
            skLineSegment(sketch, "E579", {"start": v(-0.44, 36.07) * mm, "end": v(-0.66, 36.12) * mm});
            skLineSegment(sketch, "E580", {"start": v(-0.66, 36.12) * mm, "end": v(-0.88, 36.2) * mm});
            skLineSegment(sketch, "E581", {"start": v(-0.88, 36.2) * mm, "end": v(-1.33, 36.38) * mm});
            skLineSegment(sketch, "E582", {"start": v(-1.33, 36.38) * mm, "end": v(-1.78, 36.63) * mm});
            skLineSegment(sketch, "E583", {"start": v(-1.78, 36.63) * mm, "end": v(-2.22, 36.91) * mm});
            skLineSegment(sketch, "E584", {"start": v(-2.22, 36.91) * mm, "end": v(-2.66, 37.22) * mm});
            skLineSegment(sketch, "E585", {"start": v(-2.66, 37.22) * mm, "end": v(-3.08, 37.55) * mm});
            skLineSegment(sketch, "E586", {"start": v(-3.08, 37.55) * mm, "end": v(-3.5, 37.9) * mm});
            skLineSegment(sketch, "E587", {"start": v(-3.5, 37.9) * mm, "end": v(-3.88, 38.22) * mm});
            skLineSegment(sketch, "E588", {"start": v(-3.88, 38.22) * mm, "end": v(-4.24, 38.54) * mm});
            skLineSegment(sketch, "E589", {"start": v(-4.24, 38.54) * mm, "end": v(-4.92, 39.14) * mm});
            skLineSegment(sketch, "E590", {"start": v(-4.92, 39.14) * mm, "end": v(-5.6, 39.74) * mm});
            skLineSegment(sketch, "E591", {"start": v(-5.6, 39.74) * mm, "end": v(-6.26, 40.32) * mm});
            skLineSegment(sketch, "E592", {"start": v(-6.26, 40.32) * mm, "end": v(-6.94, 40.9) * mm});
            skLineSegment(sketch, "E593", {"start": v(-6.94, 40.9) * mm, "end": v(-7.62, 41.48) * mm});
            skLineSegment(sketch, "E594", {"start": v(-7.62, 41.48) * mm, "end": v(-8.3, 42.04) * mm});
            skLineSegment(sketch, "E595", {"start": v(-8.3, 42.04) * mm, "end": v(-9.02, 42.6) * mm});
            skLineSegment(sketch, "E596", {"start": v(-9.02, 42.6) * mm, "end": v(-9.75, 43.13) * mm});
            skLineSegment(sketch, "E597", {"start": v(-9.75, 43.13) * mm, "end": v(-10.69, 43.78) * mm});
            skLineSegment(sketch, "E598", {"start": v(-10.69, 43.78) * mm, "end": v(-11.64, 44.39) * mm});
            skLineSegment(sketch, "E599", {"start": v(-11.64, 44.39) * mm, "end": v(-12.62, 44.96) * mm});
            skLineSegment(sketch, "E600", {"start": v(-12.62, 44.96) * mm, "end": v(-13.63, 45.5) * mm});
            skLineSegment(sketch, "E601", {"start": v(-13.63, 45.5) * mm, "end": v(-14.65, 45.98) * mm});
            skLineSegment(sketch, "E602", {"start": v(-14.65, 45.98) * mm, "end": v(-15.7, 46.42) * mm});
            skLineSegment(sketch, "E603", {"start": v(-15.7, 46.42) * mm, "end": v(-16.77, 46.8) * mm});
            skLineSegment(sketch, "E604", {"start": v(-16.77, 46.8) * mm, "end": v(-17.86, 47.14) * mm});
            skLineSegment(sketch, "E605", {"start": v(-17.86, 47.14) * mm, "end": v(-20.38, 47.66) * mm});
            skLineSegment(sketch, "E606", {"start": v(-20.38, 47.66) * mm, "end": v(-23, 47.91) * mm});
            skLineSegment(sketch, "E607", {"start": v(-23, 47.91) * mm, "end": v(-25.7, 47.9) * mm});
            skLineSegment(sketch, "E608", {"start": v(-25.7, 47.9) * mm, "end": v(-28.4, 47.63) * mm});
            skLineSegment(sketch, "E609", {"start": v(-28.4, 47.63) * mm, "end": v(-31.06, 47.12) * mm});
            skLineSegment(sketch, "E610", {"start": v(-31.06, 47.12) * mm, "end": v(-33.65, 46.36) * mm});
            skLineSegment(sketch, "E611", {"start": v(-33.65, 46.36) * mm, "end": v(-36.1, 45.38) * mm});
            skLineSegment(sketch, "E612", {"start": v(-36.1, 45.38) * mm, "end": v(-38.39, 44.18) * mm});
            skLineSegment(sketch, "E613", {"start": v(-38.39, 44.18) * mm, "end": v(-40.41, 42.8) * mm});
            skLineSegment(sketch, "E614", {"start": v(-40.41, 42.8) * mm, "end": v(-42.3, 41.22) * mm});
            skLineSegment(sketch, "E615", {"start": v(-42.3, 41.22) * mm, "end": v(-44.04, 39.44) * mm});
            skLineSegment(sketch, "E616", {"start": v(-44.04, 39.44) * mm, "end": v(-45.63, 37.51) * mm});
            skLineSegment(sketch, "E617", {"start": v(-45.63, 37.51) * mm, "end": v(-47.06, 35.46) * mm});
            skLineSegment(sketch, "E618", {"start": v(-47.06, 35.46) * mm, "end": v(-48.32, 33.3) * mm});
            skLineSegment(sketch, "E619", {"start": v(-48.32, 33.3) * mm, "end": v(-49.4, 31.07) * mm});
            skLineSegment(sketch, "E620", {"start": v(-49.4, 31.07) * mm, "end": v(-50.29, 28.8) * mm});
            skLineSegment(sketch, "E621", {"start": v(-50.29, 28.8) * mm, "end": v(-50.79, 27.23) * mm});
            skLineSegment(sketch, "E622", {"start": v(-50.79, 27.23) * mm, "end": v(-51.18, 25.68) * mm});
            skLineSegment(sketch, "E623", {"start": v(-51.18, 25.68) * mm, "end": v(-51.5, 24.15) * mm});
            skLineSegment(sketch, "E624", {"start": v(-51.5, 24.15) * mm, "end": v(-51.71, 22.61) * mm});
            skLineSegment(sketch, "E625", {"start": v(-51.71, 22.61) * mm, "end": v(-51.86, 21.07) * mm});
            skLineSegment(sketch, "E626", {"start": v(-51.86, 21.07) * mm, "end": v(-51.93, 19.51) * mm});
            skLineSegment(sketch, "E627", {"start": v(-51.93, 19.51) * mm, "end": v(-51.95, 17.92) * mm});
            skLineSegment(sketch, "E628", {"start": v(-51.95, 17.92) * mm, "end": v(-51.9, 16.29) * mm});
            skLineSegment(sketch, "E629", {"start": v(-51.9, 16.29) * mm, "end": v(-51.88, 15.7) * mm});
            skLineSegment(sketch, "E630", {"start": v(-51.88, 15.7) * mm, "end": v(-51.86, 15.11) * mm});
            skLineSegment(sketch, "E631", {"start": v(-51.86, 15.11) * mm, "end": v(-51.82, 14.52) * mm});
            skLineSegment(sketch, "E632", {"start": v(-51.82, 14.52) * mm, "end": v(-51.76, 13.95) * mm});
            skLineSegment(sketch, "E633", {"start": v(-51.76, 13.95) * mm, "end": v(-51.69, 13.52) * mm});
            skLineSegment(sketch, "E634", {"start": v(-51.69, 13.52) * mm, "end": v(-51.6, 13.08) * mm});
            skLineSegment(sketch, "E635", {"start": v(-51.6, 13.08) * mm, "end": v(-51.5, 12.65) * mm});
            skLineSegment(sketch, "E636", {"start": v(-51.5, 12.65) * mm, "end": v(-51.4, 12.22) * mm});
            skLineSegment(sketch, "E637", {"start": v(-51.4, 12.22) * mm, "end": v(-51.1, 10.98) * mm});
            skLineSegment(sketch, "E638", {"start": v(-51.1, 10.98) * mm, "end": v(-50.8, 9.74) * mm});
            skLineSegment(sketch, "E639", {"start": v(-50.8, 9.74) * mm, "end": v(-50.47, 8.51) * mm});
            skLineSegment(sketch, "E640", {"start": v(-50.47, 8.51) * mm, "end": v(-50.13, 7.29) * mm});
            skLineSegment(sketch, "E641", {"start": v(-50.13, 7.29) * mm, "end": v(-49.76, 6.07) * mm});
            skLineSegment(sketch, "E642", {"start": v(-49.76, 6.07) * mm, "end": v(-49.38, 4.85) * mm});
            skLineSegment(sketch, "E643", {"start": v(-49.38, 4.85) * mm, "end": v(-48.96, 3.65) * mm});
            skLineSegment(sketch, "E644", {"start": v(-48.96, 3.65) * mm, "end": v(-48.52, 2.45) * mm});
            skLineSegment(sketch, "E645", {"start": v(-48.52, 2.45) * mm, "end": v(-47.92, 0.97) * mm});
            skLineSegment(sketch, "E646", {"start": v(-47.92, 0.97) * mm, "end": v(-47.27, -0.49) * mm});
            skLineSegment(sketch, "E647", {"start": v(-47.27, -0.49) * mm, "end": v(-46.57, -1.93) * mm});
            skLineSegment(sketch, "E648", {"start": v(-46.57, -1.93) * mm, "end": v(-45.84, -3.35) * mm});
            skLineSegment(sketch, "E649", {"start": v(-45.84, -3.35) * mm, "end": v(-45.07, -4.76) * mm});
            skLineSegment(sketch, "E650", {"start": v(-45.07, -4.76) * mm, "end": v(-44.26, -6.14) * mm});
            skLineSegment(sketch, "E651", {"start": v(-44.26, -6.14) * mm, "end": v(-43.43, -7.5) * mm});
            skLineSegment(sketch, "E652", {"start": v(-43.43, -7.5) * mm, "end": v(-42.57, -8.85) * mm});
            skLineSegment(sketch, "E653", {"start": v(-42.57, -8.85) * mm, "end": v(-41.66, -10.2) * mm});
            skLineSegment(sketch, "E654", {"start": v(-41.66, -10.2) * mm, "end": v(-40.73, -11.55) * mm});
            skLineSegment(sketch, "E655", {"start": v(-40.73, -11.55) * mm, "end": v(-39.78, -12.88) * mm});
            skLineSegment(sketch, "E656", {"start": v(-39.78, -12.88) * mm, "end": v(-38.81, -14.2) * mm});
            skLineSegment(sketch, "E657", {"start": v(-38.81, -14.2) * mm, "end": v(-37.83, -15.5) * mm});
            skLineSegment(sketch, "E658", {"start": v(-37.83, -15.5) * mm, "end": v(-36.83, -16.8) * mm});
            skLineSegment(sketch, "E659", {"start": v(-36.83, -16.8) * mm, "end": v(-35.82, -18.08) * mm});
            skLineSegment(sketch, "E660", {"start": v(-35.82, -18.08) * mm, "end": v(-34.8, -19.36) * mm});
            skLineSegment(sketch, "E661", {"start": v(-34.8, -19.36) * mm, "end": v(-33.9, -20.5) * mm});
            skLineSegment(sketch, "E662", {"start": v(-33.9, -20.5) * mm, "end": v(-33, -21.62) * mm});
            skLineSegment(sketch, "E663", {"start": v(-33, -21.62) * mm, "end": v(-32.07, -22.74) * mm});
            skLineSegment(sketch, "E664", {"start": v(-32.07, -22.74) * mm, "end": v(-31.14, -23.86) * mm});
            skLineSegment(sketch, "E665", {"start": v(-31.14, -23.86) * mm, "end": v(-30.2, -24.97) * mm});
            skLineSegment(sketch, "E666", {"start": v(-30.2, -24.97) * mm, "end": v(-29.25, -26.06) * mm});
            skLineSegment(sketch, "E667", {"start": v(-29.25, -26.06) * mm, "end": v(-28.28, -27.15) * mm});
            skLineSegment(sketch, "E668", {"start": v(-28.28, -27.15) * mm, "end": v(-27.3, -28.21) * mm});
            skLineSegment(sketch, "E669", {"start": v(-27.3, -28.21) * mm, "end": v(-26.37, -29.2) * mm});
            skLineSegment(sketch, "E670", {"start": v(-26.37, -29.2) * mm, "end": v(-25.43, -30.15) * mm});
            skLineSegment(sketch, "E671", {"start": v(-25.43, -30.15) * mm, "end": v(-24.47, -31.1) * mm});
            skLineSegment(sketch, "E672", {"start": v(-24.47, -31.1) * mm, "end": v(-23.5, -32.03) * mm});
            skLineSegment(sketch, "E673", {"start": v(-23.5, -32.03) * mm, "end": v(-22.5, -32.95) * mm});
            skLineSegment(sketch, "E674", {"start": v(-22.5, -32.95) * mm, "end": v(-21.5, -33.85) * mm});
            skLineSegment(sketch, "E675", {"start": v(-21.5, -33.85) * mm, "end": v(-20.5, -34.74) * mm});
            skLineSegment(sketch, "E676", {"start": v(-20.5, -34.74) * mm, "end": v(-19.47, -35.62) * mm});
            skLineSegment(sketch, "E677", {"start": v(-19.47, -35.62) * mm, "end": v(-18.46, -36.46) * mm});
            skLineSegment(sketch, "E678", {"start": v(-18.46, -36.46) * mm, "end": v(-17.44, -37.29) * mm});
            skLineSegment(sketch, "E679", {"start": v(-17.44, -37.29) * mm, "end": v(-16.4, -38.1) * mm});
            skLineSegment(sketch, "E680", {"start": v(-16.4, -38.1) * mm, "end": v(-15.37, -38.9) * mm});
            skLineSegment(sketch, "E681", {"start": v(-15.37, -38.9) * mm, "end": v(-14.32, -39.7) * mm});
            skLineSegment(sketch, "E682", {"start": v(-14.32, -39.7) * mm, "end": v(-13.25, -40.47) * mm});
            skLineSegment(sketch, "E683", {"start": v(-13.25, -40.47) * mm, "end": v(-12.18, -41.23) * mm});
            skLineSegment(sketch, "E684", {"start": v(-12.18, -41.23) * mm, "end": v(-11.1, -41.97) * mm});
            skLineSegment(sketch, "E685", {"start": v(-11.1, -41.97) * mm, "end": v(-10.2, -42.57) * mm});
            skLineSegment(sketch, "E686", {"start": v(-10.2, -42.57) * mm, "end": v(-9.28, -43.17) * mm});
            skLineSegment(sketch, "E687", {"start": v(-9.28, -43.17) * mm, "end": v(-8.36, -43.75) * mm});
            skLineSegment(sketch, "E688", {"start": v(-8.36, -43.75) * mm, "end": v(-7.42, -44.33) * mm});
            skLineSegment(sketch, "E689", {"start": v(-7.42, -44.33) * mm, "end": v(-6.48, -44.89) * mm});
            skLineSegment(sketch, "E690", {"start": v(-6.48, -44.89) * mm, "end": v(-5.53, -45.43) * mm});
            skLineSegment(sketch, "E691", {"start": v(-5.53, -45.43) * mm, "end": v(-4.57, -45.95) * mm});
            skLineSegment(sketch, "E692", {"start": v(-4.57, -45.95) * mm, "end": v(-3.61, -46.45) * mm});
            skLineSegment(sketch, "E693", {"start": v(-3.61, -46.45) * mm, "end": v(-3.26, -46.63) * mm});
            skLineSegment(sketch, "E694", {"start": v(-3.26, -46.63) * mm, "end": v(-2.86, -46.83) * mm});
            skLineSegment(sketch, "E695", {"start": v(-2.86, -46.83) * mm, "end": v(-2.44, -47.04) * mm});
            skLineSegment(sketch, "E696", {"start": v(-2.44, -47.04) * mm, "end": v(-2, -47.25) * mm});
            skLineSegment(sketch, "E697", {"start": v(-2, -47.25) * mm, "end": v(-1.56, -47.45) * mm});
            skLineSegment(sketch, "E698", {"start": v(-1.56, -47.45) * mm, "end": v(-1.12, -47.62) * mm});
            skLineSegment(sketch, "E699", {"start": v(-1.12, -47.62) * mm, "end": v(-0.7, -47.75) * mm});
            skLineSegment(sketch, "E700", {"start": v(-0.7, -47.75) * mm, "end": v(-0.31, -47.82) * mm});
            skLineSegment(sketch, "E701", {"start": v(-0.31, -47.82) * mm, "end": v(0, -47.87) * mm});
            skLineSegment(sketch, "E702.MirrorCS", {"start": v(-0.22, 36.04) * mm, "end": v(0, 36.03) * mm});
            skLineSegment(sketch, "E703.MirrorCS", {"start": v(0, 36.03) * mm, "end": v(0.22, 36.04) * mm});
            skLineSegment(sketch, "E704.MirrorCS", {"start": v(-0.43, 38.78) * mm, "end": v(-0.2, 38.66) * mm});
            skLineSegment(sketch, "E705.MirrorCS", {"start": v(-1.31, 39.4) * mm, "end": v(-0.98, 39.15) * mm});
            skLineSegment(sketch, "E706.MirrorCS", {"start": v(0.22, 36.04) * mm, "end": v(0.44, 36.07) * mm});
            skLineSegment(sketch, "E707.MirrorCS", {"start": v(0.98, 39.15) * mm, "end": v(1.31, 39.4) * mm});
            skLineSegment(sketch, "E708.MirrorCS", {"start": v(-0.44, 36.07) * mm, "end": v(-0.22, 36.04) * mm});
            skLineSegment(sketch, "E709.MirrorCS", {"start": v(-0.88, 36.2) * mm, "end": v(-0.66, 36.12) * mm});
            skLineSegment(sketch, "E710.MirrorCS", {"start": v(0.2, 38.66) * mm, "end": v(0.43, 38.78) * mm});
            skLineSegment(sketch, "E711.MirrorCS", {"start": v(-0.2, 38.66) * mm, "end": v(0, 38.57) * mm});
            skLineSegment(sketch, "E712.MirrorCS", {"start": v(-2.22, 36.91) * mm, "end": v(-1.78, 36.63) * mm});
            skLineSegment(sketch, "E713.MirrorCS", {"start": v(3.08, 37.55) * mm, "end": v(3.5, 37.9) * mm});
            skLineSegment(sketch, "E714.MirrorCS", {"start": v(2.22, 36.91) * mm, "end": v(2.66, 37.22) * mm});
            skLineSegment(sketch, "E715.MirrorCS", {"start": v(-3.08, 37.55) * mm, "end": v(-2.66, 37.22) * mm});
            skLineSegment(sketch, "E716.MirrorCS", {"start": v(-0.98, 39.15) * mm, "end": v(-0.69, 38.95) * mm});
            skLineSegment(sketch, "E717.MirrorCS", {"start": v(1.33, 36.38) * mm, "end": v(1.78, 36.63) * mm});
            skLineSegment(sketch, "E718.MirrorCS", {"start": v(0.66, 36.12) * mm, "end": v(0.88, 36.2) * mm});
            skLineSegment(sketch, "E719.MirrorCS", {"start": v(-2.57, 40.45) * mm, "end": v(-2.1, 40.05) * mm});
            skLineSegment(sketch, "E720.MirrorCS", {"start": v(1.31, 39.4) * mm, "end": v(1.68, 39.7) * mm});
            skLineSegment(sketch, "E721.MirrorCS", {"start": v(-0.66, 36.12) * mm, "end": v(-0.44, 36.07) * mm});
            skLineSegment(sketch, "E722.MirrorCS", {"start": v(0.43, 38.78) * mm, "end": v(0.69, 38.95) * mm});
            skLineSegment(sketch, "E723.MirrorCS", {"start": v(-1.33, 36.38) * mm, "end": v(-0.88, 36.2) * mm});
            skLineSegment(sketch, "E724.MirrorCS", {"start": v(0, 38.57) * mm, "end": v(0.2, 38.66) * mm});
            skLineSegment(sketch, "E725.MirrorCS", {"start": v(-1.78, 36.63) * mm, "end": v(-1.33, 36.38) * mm});
            skLineSegment(sketch, "E726.MirrorCS", {"start": v(3.5, 37.9) * mm, "end": v(3.88, 38.22) * mm});
            skLineSegment(sketch, "E727.MirrorCS", {"start": v(-2.66, 37.22) * mm, "end": v(-2.22, 36.91) * mm});
            skLineSegment(sketch, "E728.MirrorCS", {"start": v(2.66, 37.22) * mm, "end": v(3.08, 37.55) * mm});
            skLineSegment(sketch, "E729.MirrorCS", {"start": v(-0.69, 38.95) * mm, "end": v(-0.43, 38.78) * mm});
            skLineSegment(sketch, "E730.MirrorCS", {"start": v(1.78, 36.63) * mm, "end": v(2.22, 36.91) * mm});
            skLineSegment(sketch, "E731.MirrorCS", {"start": v(-1.68, 39.7) * mm, "end": v(-1.31, 39.4) * mm});
            skLineSegment(sketch, "E732.MirrorCS", {"start": v(-2.1, 40.05) * mm, "end": v(-1.68, 39.7) * mm});
            skLineSegment(sketch, "E733.MirrorCS", {"start": v(0.88, 36.2) * mm, "end": v(1.33, 36.38) * mm});
            skLineSegment(sketch, "E734.MirrorCS", {"start": v(2.1, 40.05) * mm, "end": v(2.57, 40.45) * mm});
            skLineSegment(sketch, "E735.MirrorCS", {"start": v(-3.68, 41.44) * mm, "end": v(-2.57, 40.45) * mm});
            skLineSegment(sketch, "E736.MirrorCS", {"start": v(1.68, 39.7) * mm, "end": v(2.1, 40.05) * mm});
            skLineSegment(sketch, "E737.MirrorCS", {"start": v(0.69, 38.95) * mm, "end": v(0.98, 39.15) * mm});
            skLineSegment(sketch, "E738.MirrorCS", {"start": v(-2, -47.25) * mm, "end": v(-2.44, -47.04) * mm});
            skLineSegment(sketch, "E739.MirrorCS", {"start": v(0, -47.87) * mm, "end": v(-0.31, -47.82) * mm});
            skLineSegment(sketch, "E740.MirrorCS", {"start": v(-1.06, -50.27) * mm, "end": v(-1.47, -50.17) * mm});
            skLineSegment(sketch, "E741.MirrorCS", {"start": v(1.12, -47.62) * mm, "end": v(0.7, -47.75) * mm});
            skLineSegment(sketch, "E742.MirrorCS", {"start": v(0, -50.44) * mm, "end": v(-0.64, -50.34) * mm});
            skLineSegment(sketch, "E743.MirrorCS", {"start": v(-2.44, -47.04) * mm, "end": v(-2.86, -46.83) * mm});
            skLineSegment(sketch, "E744.MirrorCS", {"start": v(1.06, -50.27) * mm, "end": v(0.64, -50.34) * mm});
            skLineSegment(sketch, "E745.MirrorCS", {"start": v(-0.7, -47.75) * mm, "end": v(-1.12, -47.62) * mm});
            skLineSegment(sketch, "E746.MirrorCS", {"start": v(3.61, -46.45) * mm, "end": v(3.26, -46.63) * mm});
            skLineSegment(sketch, "E747.MirrorCS", {"start": v(-0.31, -47.82) * mm, "end": v(-0.7, -47.75) * mm});
            skLineSegment(sketch, "E748.MirrorCS", {"start": v(-1.47, -50.17) * mm, "end": v(-1.9, -50.04) * mm});
            skLineSegment(sketch, "E749.MirrorCS", {"start": v(0.31, -47.82) * mm, "end": v(0, -47.87) * mm});
            skLineSegment(sketch, "E750.MirrorCS", {"start": v(0.7, -47.75) * mm, "end": v(0.31, -47.82) * mm});
            skLineSegment(sketch, "E751.MirrorCS", {"start": v(-0.64, -50.34) * mm, "end": v(-1.06, -50.27) * mm});
            skLineSegment(sketch, "E752.MirrorCS", {"start": v(-2.86, -46.83) * mm, "end": v(-3.26, -46.63) * mm});
            skLineSegment(sketch, "E753.MirrorCS", {"start": v(1.56, -47.45) * mm, "end": v(1.12, -47.62) * mm});
            skLineSegment(sketch, "E754.MirrorCS", {"start": v(51.69, 13.52) * mm, "end": v(51.6, 13.08) * mm});
            skLineSegment(sketch, "E755.MirrorCS", {"start": v(0.64, -50.34) * mm, "end": v(0, -50.44) * mm});
            skLineSegment(sketch, "E756.MirrorCS", {"start": v(2, -47.25) * mm, "end": v(1.56, -47.45) * mm});
            skLineSegment(sketch, "E757.MirrorCS", {"start": v(-1.56, -47.45) * mm, "end": v(-2, -47.25) * mm});
            skLineSegment(sketch, "E758.MirrorCS", {"start": v(1.47, -50.17) * mm, "end": v(1.06, -50.27) * mm});
            skLineSegment(sketch, "E759.MirrorCS", {"start": v(2.44, -47.04) * mm, "end": v(2, -47.25) * mm});
            skLineSegment(sketch, "E760.MirrorCS", {"start": v(-1.12, -47.62) * mm, "end": v(-1.56, -47.45) * mm});
            skLineSegment(sketch, "E761.MirrorCS", {"start": v(1.9, -50.04) * mm, "end": v(1.47, -50.17) * mm});
            skLineSegment(sketch, "E762.MirrorCS", {"start": v(54.23, 13.31) * mm, "end": v(54.14, 12.86) * mm});
            skLineSegment(sketch, "E763.MirrorCS", {"start": v(2.86, -46.83) * mm, "end": v(2.44, -47.04) * mm});
            skLineSegment(sketch, "E764.MirrorCS", {"start": v(2.35, -49.86) * mm, "end": v(1.9, -50.04) * mm});
            skLineSegment(sketch, "E765.MirrorCS", {"start": v(3.26, -46.63) * mm, "end": v(2.86, -46.83) * mm});
            skLineSegment(sketch, "E766.MirrorCS", {"start": v(2.85, -49.65) * mm, "end": v(2.35, -49.86) * mm});
            skLineSegment(sketch, "E767.MirrorCS", {"start": v(3.4, -49.39) * mm, "end": v(2.85, -49.65) * mm});
            skLineSegment(sketch, "E768.MirrorCS", {"start": v(4.04, -49.08) * mm, "end": v(3.4, -49.39) * mm});
            skLineSegment(sketch, "E769.MirrorCS", {"start": v(51.6, 13.08) * mm, "end": v(51.5, 12.65) * mm});
            skLineSegment(sketch, "E770.MirrorCS", {"start": v(54.14, 12.86) * mm, "end": v(54.02, 12.32) * mm});
            skLineSegment(sketch, "E771.MirrorCS", {"start": v(51.86, 15.11) * mm, "end": v(51.82, 14.52) * mm});
            skLineSegment(sketch, "E772.MirrorCS", {"start": v(54.34, 14.18) * mm, "end": v(54.3, 13.74) * mm});
            skLineSegment(sketch, "E773.MirrorCS", {"start": v(2.57, 40.45) * mm, "end": v(3.68, 41.44) * mm});
            skLineSegment(sketch, "E774.MirrorCS", {"start": v(4.92, 39.14) * mm, "end": v(5.6, 39.74) * mm});
            skLineSegment(sketch, "E775.MirrorCS", {"start": v(51.4, 12.22) * mm, "end": v(51.1, 10.98) * mm});
            skLineSegment(sketch, "E776.MirrorCS", {"start": v(4.24, 38.54) * mm, "end": v(4.92, 39.14) * mm});
            skLineSegment(sketch, "E777.MirrorCS", {"start": v(51.5, 12.65) * mm, "end": v(51.4, 12.22) * mm});
            skLineSegment(sketch, "E778.MirrorCS", {"start": v(3.88, 38.22) * mm, "end": v(4.24, 38.54) * mm});
            skLineSegment(sketch, "E779.MirrorCS", {"start": v(51.76, 13.95) * mm, "end": v(51.69, 13.52) * mm});
            skLineSegment(sketch, "E780.MirrorCS", {"start": v(54.02, 12.32) * mm, "end": v(53.87, 11.65) * mm});
            skLineSegment(sketch, "E781.MirrorCS", {"start": v(51.82, 14.52) * mm, "end": v(51.76, 13.95) * mm});
            skLineSegment(sketch, "E782.MirrorCS", {"start": v(54.3, 13.74) * mm, "end": v(54.23, 13.31) * mm});
            skLineSegment(sketch, "E783.MirrorCS", {"start": v(51.88, 15.7) * mm, "end": v(51.86, 15.11) * mm});
            skLineSegment(sketch, "E784.MirrorCS", {"start": v(51.9, 16.29) * mm, "end": v(51.88, 15.7) * mm});
            skLineSegment(sketch, "E785.MirrorCS", {"start": v(-4.24, 38.54) * mm, "end": v(-3.88, 38.22) * mm});
            skLineSegment(sketch, "E786.MirrorCS", {"start": v(54.38, 14.7) * mm, "end": v(54.34, 14.18) * mm});
            skLineSegment(sketch, "E787.MirrorCS", {"start": v(4.57, -45.95) * mm, "end": v(3.61, -46.45) * mm});
            skLineSegment(sketch, "E788.MirrorCS", {"start": v(54.4, 15.35) * mm, "end": v(54.38, 14.7) * mm});
            skLineSegment(sketch, "E789.MirrorCS", {"start": v(0.44, 36.07) * mm, "end": v(0.66, 36.12) * mm});
            skLineSegment(sketch, "E790.MirrorCS", {"start": v(4.76, -48.72) * mm, "end": v(4.04, -49.08) * mm});
            skLineSegment(sketch, "E791.MirrorCS", {"start": v(5.56, -48.3) * mm, "end": v(4.76, -48.72) * mm});
            skLineSegment(sketch, "E792.MirrorCS", {"start": v(-3.88, 38.22) * mm, "end": v(-3.5, 37.9) * mm});
            skLineSegment(sketch, "E793.MirrorCS", {"start": v(-2.35, -49.86) * mm, "end": v(-2.85, -49.65) * mm});
            skLineSegment(sketch, "E794.MirrorCS", {"start": v(3.68, 41.44) * mm, "end": v(5, 42.6) * mm});
            skLineSegment(sketch, "E795.MirrorCS", {"start": v(-3.26, -46.63) * mm, "end": v(-3.61, -46.45) * mm});
            skLineSegment(sketch, "E796.MirrorCS", {"start": v(-3.5, 37.9) * mm, "end": v(-3.08, 37.55) * mm});
            skLineSegment(sketch, "E797.MirrorCS", {"start": v(-4.04, -49.08) * mm, "end": v(-4.76, -48.72) * mm});
            skLineSegment(sketch, "E798.MirrorCS", {"start": v(-3.4, -49.39) * mm, "end": v(-4.04, -49.08) * mm});
            skLineSegment(sketch, "E799.MirrorCS", {"start": v(-2.85, -49.65) * mm, "end": v(-3.4, -49.39) * mm});
            skLineSegment(sketch, "E800.MirrorCS", {"start": v(-54.3, 13.74) * mm, "end": v(-54.34, 14.18) * mm});
            skLineSegment(sketch, "E801.MirrorCS", {"start": v(-1.9, -50.04) * mm, "end": v(-2.35, -49.86) * mm});
            skLineSegment(sketch, "E802.MirrorCS", {"start": v(5.6, 39.74) * mm, "end": v(6.26, 40.32) * mm});
            skLineSegment(sketch, "E803.MirrorCS", {"start": v(6.53, 43.88) * mm, "end": v(8.27, 45.2) * mm});
            skLineSegment(sketch, "E804.MirrorCS", {"start": v(5, 42.6) * mm, "end": v(6.53, 43.88) * mm});
            skLineSegment(sketch, "E805.MirrorCS", {"start": v(-3.61, -46.45) * mm, "end": v(-4.57, -45.95) * mm});
            skLineSegment(sketch, "E806.MirrorCS", {"start": v(53.87, 11.65) * mm, "end": v(53.67, 10.8) * mm});
            skLineSegment(sketch, "E807.MirrorCS", {"start": v(-51.69, 13.52) * mm, "end": v(-51.76, 13.95) * mm});
            skLineSegment(sketch, "E808.MirrorCS", {"start": v(9.75, 43.13) * mm, "end": v(10.69, 43.78) * mm});
            skLineSegment(sketch, "E809.MirrorCS", {"start": v(-51.4, 12.22) * mm, "end": v(-51.5, 12.65) * mm});
            skLineSegment(sketch, "E810.MirrorCS", {"start": v(9.02, 42.6) * mm, "end": v(9.75, 43.13) * mm});
            skLineSegment(sketch, "E811.MirrorCS", {"start": v(8.3, 42.04) * mm, "end": v(9.02, 42.6) * mm});
            skLineSegment(sketch, "E812.MirrorCS", {"start": v(7.62, 41.48) * mm, "end": v(8.3, 42.04) * mm});
            skLineSegment(sketch, "E813.MirrorCS", {"start": v(-6.26, 40.32) * mm, "end": v(-5.6, 39.74) * mm});
            skLineSegment(sketch, "E814.MirrorCS", {"start": v(6.94, 40.9) * mm, "end": v(7.62, 41.48) * mm});
            skLineSegment(sketch, "E815.MirrorCS", {"start": v(-54.34, 14.18) * mm, "end": v(-54.38, 14.7) * mm});
            skLineSegment(sketch, "E816.MirrorCS", {"start": v(6.26, 40.32) * mm, "end": v(6.94, 40.9) * mm});
            skLineSegment(sketch, "E817.MirrorCS", {"start": v(7.35, -47.3) * mm, "end": v(6.43, -47.83) * mm});
            skLineSegment(sketch, "E818.MirrorCS", {"start": v(50.8, 9.74) * mm, "end": v(50.47, 8.51) * mm});
            skLineSegment(sketch, "E819.MirrorCS", {"start": v(14.68, 48.75) * mm, "end": v(17.2, 49.59) * mm});
            skLineSegment(sketch, "E820.MirrorCS", {"start": v(12.35, 47.7) * mm, "end": v(14.68, 48.75) * mm});
            skLineSegment(sketch, "E821.MirrorCS", {"start": v(10.21, 46.49) * mm, "end": v(12.35, 47.7) * mm});
            skLineSegment(sketch, "E822.MirrorCS", {"start": v(10.2, -42.57) * mm, "end": v(9.28, -43.17) * mm});
            skLineSegment(sketch, "E823.MirrorCS", {"start": v(51.1, 10.98) * mm, "end": v(50.8, 9.74) * mm});
            skLineSegment(sketch, "E824.MirrorCS", {"start": v(-4.57, -45.95) * mm, "end": v(-5.53, -45.43) * mm});
            skLineSegment(sketch, "E825.MirrorCS", {"start": v(-54.14, 12.86) * mm, "end": v(-54.23, 13.31) * mm});
            skLineSegment(sketch, "E826.MirrorCS", {"start": v(8.32, -46.74) * mm, "end": v(7.35, -47.3) * mm});
            skLineSegment(sketch, "E827.MirrorCS", {"start": v(-51.9, 16.29) * mm, "end": v(-51.95, 17.92) * mm});
            skLineSegment(sketch, "E828.MirrorCS", {"start": v(-54.02, 12.32) * mm, "end": v(-54.14, 12.86) * mm});
            skLineSegment(sketch, "E829.MirrorCS", {"start": v(9.34, -46.13) * mm, "end": v(8.32, -46.74) * mm});
            skLineSegment(sketch, "E830.MirrorCS", {"start": v(16.77, 46.8) * mm, "end": v(17.86, 47.14) * mm});
            skLineSegment(sketch, "E831.MirrorCS", {"start": v(-51.88, 15.7) * mm, "end": v(-51.9, 16.29) * mm});
            skLineSegment(sketch, "E832.MirrorCS", {"start": v(-53.87, 11.65) * mm, "end": v(-54.02, 12.32) * mm});
            skLineSegment(sketch, "E833.MirrorCS", {"start": v(10.38, -45.48) * mm, "end": v(9.34, -46.13) * mm});
            skLineSegment(sketch, "E834.MirrorCS", {"start": v(53.42, 9.77) * mm, "end": v(53.12, 8.61) * mm});
            skLineSegment(sketch, "E835.MirrorCS", {"start": v(15.7, 46.42) * mm, "end": v(16.77, 46.8) * mm});
            skLineSegment(sketch, "E836.MirrorCS", {"start": v(-51.86, 15.11) * mm, "end": v(-51.88, 15.7) * mm});
            skLineSegment(sketch, "E837.MirrorCS", {"start": v(-53.67, 10.8) * mm, "end": v(-53.87, 11.65) * mm});
            skLineSegment(sketch, "E838.MirrorCS", {"start": v(11.44, -44.8) * mm, "end": v(10.38, -45.48) * mm});
            skLineSegment(sketch, "E839.MirrorCS", {"start": v(53.67, 10.8) * mm, "end": v(53.42, 9.77) * mm});
            skLineSegment(sketch, "E840.MirrorCS", {"start": v(14.65, 45.98) * mm, "end": v(15.7, 46.42) * mm});
            skLineSegment(sketch, "E841.MirrorCS", {"start": v(-51.82, 14.52) * mm, "end": v(-51.86, 15.11) * mm});
            skLineSegment(sketch, "E842.MirrorCS", {"start": v(-53.42, 9.77) * mm, "end": v(-53.67, 10.8) * mm});
            skLineSegment(sketch, "E843.MirrorCS", {"start": v(13.63, 45.5) * mm, "end": v(14.65, 45.98) * mm});
            skLineSegment(sketch, "E844.MirrorCS", {"start": v(-51.76, 13.95) * mm, "end": v(-51.82, 14.52) * mm});
            skLineSegment(sketch, "E845.MirrorCS", {"start": v(-53.12, 8.61) * mm, "end": v(-53.42, 9.77) * mm});
            skLineSegment(sketch, "E846.MirrorCS", {"start": v(12.62, 44.96) * mm, "end": v(13.63, 45.5) * mm});
            skLineSegment(sketch, "E847.MirrorCS", {"start": v(-51.6, 13.08) * mm, "end": v(-51.69, 13.52) * mm});
            skLineSegment(sketch, "E848.MirrorCS", {"start": v(11.64, 44.39) * mm, "end": v(12.62, 44.96) * mm});
            skLineSegment(sketch, "E849.MirrorCS", {"start": v(10.69, 43.78) * mm, "end": v(11.64, 44.39) * mm});
            skLineSegment(sketch, "E850.MirrorCS", {"start": v(-51.5, 12.65) * mm, "end": v(-51.6, 13.08) * mm});
            skLineSegment(sketch, "E851.MirrorCS", {"start": v(-54.48, 17.24) * mm, "end": v(-54.5, 18.51) * mm});
            skLineSegment(sketch, "E852.MirrorCS", {"start": v(-5.56, -48.3) * mm, "end": v(-6.43, -47.83) * mm});
            skLineSegment(sketch, "E853.MirrorCS", {"start": v(-4.76, -48.72) * mm, "end": v(-5.56, -48.3) * mm});
            skLineSegment(sketch, "E854.MirrorCS", {"start": v(51.95, 17.92) * mm, "end": v(51.9, 16.29) * mm});
            skLineSegment(sketch, "E855.MirrorCS", {"start": v(-51.1, 10.98) * mm, "end": v(-51.4, 12.22) * mm});
            skLineSegment(sketch, "E856.MirrorCS", {"start": v(-4.92, 39.14) * mm, "end": v(-4.24, 38.54) * mm});
            skLineSegment(sketch, "E857.MirrorCS", {"start": v(-54.44, 16.19) * mm, "end": v(-54.48, 17.24) * mm});
            skLineSegment(sketch, "E858.MirrorCS", {"start": v(5.53, -45.43) * mm, "end": v(4.57, -45.95) * mm});
            skLineSegment(sketch, "E859.MirrorCS", {"start": v(-50.8, 9.74) * mm, "end": v(-51.1, 10.98) * mm});
            skLineSegment(sketch, "E860.MirrorCS", {"start": v(-5.6, 39.74) * mm, "end": v(-4.92, 39.14) * mm});
            skLineSegment(sketch, "E861.MirrorCS", {"start": v(-54.4, 15.35) * mm, "end": v(-54.44, 16.19) * mm});
            skLineSegment(sketch, "E862.MirrorCS", {"start": v(6.48, -44.89) * mm, "end": v(5.53, -45.43) * mm});
            skLineSegment(sketch, "E863.MirrorCS", {"start": v(-54.38, 14.7) * mm, "end": v(-54.4, 15.35) * mm});
            skLineSegment(sketch, "E864.MirrorCS", {"start": v(54.44, 16.19) * mm, "end": v(54.4, 15.35) * mm});
            skLineSegment(sketch, "E865.MirrorCS", {"start": v(54.48, 17.24) * mm, "end": v(54.44, 16.19) * mm});
            skLineSegment(sketch, "E866.MirrorCS", {"start": v(7.42, -44.33) * mm, "end": v(6.48, -44.89) * mm});
            skLineSegment(sketch, "E867.MirrorCS", {"start": v(6.43, -47.83) * mm, "end": v(5.56, -48.3) * mm});
            skLineSegment(sketch, "E868.MirrorCS", {"start": v(54.5, 18.51) * mm, "end": v(54.48, 17.24) * mm});
            skLineSegment(sketch, "E869.MirrorCS", {"start": v(8.36, -43.75) * mm, "end": v(7.42, -44.33) * mm});
            skLineSegment(sketch, "E870.MirrorCS", {"start": v(-5.53, -45.43) * mm, "end": v(-6.48, -44.89) * mm});
            skLineSegment(sketch, "E871.MirrorCS", {"start": v(-54.23, 13.31) * mm, "end": v(-54.3, 13.74) * mm});
            skLineSegment(sketch, "E872.MirrorCS", {"start": v(9.28, -43.17) * mm, "end": v(8.36, -43.75) * mm});
            skLineSegment(sketch, "E873.MirrorCS", {"start": v(-14.65, 45.98) * mm, "end": v(-13.63, 45.5) * mm});
            skLineSegment(sketch, "E874.MirrorCS", {"start": v(-6.43, -47.83) * mm, "end": v(-7.35, -47.3) * mm});
            skLineSegment(sketch, "E875.MirrorCS", {"start": v(-8.36, -43.75) * mm, "end": v(-9.28, -43.17) * mm});
            skLineSegment(sketch, "E876.MirrorCS", {"start": v(-8.3, 42.04) * mm, "end": v(-7.62, 41.48) * mm});
            skLineSegment(sketch, "E877.MirrorCS", {"start": v(8.27, 45.2) * mm, "end": v(10.21, 46.49) * mm});
            skLineSegment(sketch, "E878.MirrorCS", {"start": v(26.37, -29.2) * mm, "end": v(25.43, -30.15) * mm});
            skLineSegment(sketch, "E879.MirrorCS", {"start": v(-9.02, 42.6) * mm, "end": v(-8.3, 42.04) * mm});
            skLineSegment(sketch, "E880.MirrorCS", {"start": v(-48.96, 3.65) * mm, "end": v(-49.38, 4.85) * mm});
            skLineSegment(sketch, "E881.MirrorCS", {"start": v(-51.95, 17.92) * mm, "end": v(-51.93, 19.51) * mm});
            skLineSegment(sketch, "E882.MirrorCS", {"start": v(-12.35, 47.7) * mm, "end": v(-10.21, 46.49) * mm});
            skLineSegment(sketch, "E883.MirrorCS", {"start": v(-31.06, -27.85) * mm, "end": v(-32, -26.76) * mm});
            skLineSegment(sketch, "E884.MirrorCS", {"start": v(-46.5, -7.37) * mm, "end": v(-47.33, -5.9) * mm});
            skLineSegment(sketch, "E885.MirrorCS", {"start": v(25.22, -33.9) * mm, "end": v(24.2, -34.84) * mm});
            skLineSegment(sketch, "E886.MirrorCS", {"start": v(52.78, 7.33) * mm, "end": v(52.39, 5.96) * mm});
            skLineSegment(sketch, "E887.MirrorCS", {"start": v(40.8, -15.78) * mm, "end": v(39.8, -17.1) * mm});
            skLineSegment(sketch, "E888.MirrorCS", {"start": v(27.3, -28.21) * mm, "end": v(26.37, -29.2) * mm});
            skLineSegment(sketch, "E889.MirrorCS", {"start": v(11.1, -41.97) * mm, "end": v(10.2, -42.57) * mm});
            skLineSegment(sketch, "E890.MirrorCS", {"start": v(50.29, 28.8) * mm, "end": v(50.79, 27.23) * mm});
            skLineSegment(sketch, "E891.MirrorCS", {"start": v(-9.75, 43.13) * mm, "end": v(-9.02, 42.6) * mm});
            skLineSegment(sketch, "E892.MirrorCS", {"start": v(-34.8, -19.36) * mm, "end": v(-35.82, -18.08) * mm});
            skLineSegment(sketch, "E893.MirrorCS", {"start": v(-48.52, 2.45) * mm, "end": v(-48.96, 3.65) * mm});
            skLineSegment(sketch, "E894.MirrorCS", {"start": v(-14.68, 48.75) * mm, "end": v(-12.35, 47.7) * mm});
            skLineSegment(sketch, "E895.MirrorCS", {"start": v(26.22, -32.94) * mm, "end": v(25.22, -33.9) * mm});
            skLineSegment(sketch, "E896.MirrorCS", {"start": v(53.12, 8.61) * mm, "end": v(52.78, 7.33) * mm});
            skLineSegment(sketch, "E897.MirrorCS", {"start": v(28.28, -27.15) * mm, "end": v(27.3, -28.21) * mm});
            skLineSegment(sketch, "E898.MirrorCS", {"start": v(12.18, -41.23) * mm, "end": v(11.1, -41.97) * mm});
            skLineSegment(sketch, "E899.MirrorCS", {"start": v(49.4, 31.07) * mm, "end": v(50.29, 28.8) * mm});
            skLineSegment(sketch, "E900.MirrorCS", {"start": v(-10.69, 43.78) * mm, "end": v(-9.75, 43.13) * mm});
            skLineSegment(sketch, "E901.MirrorCS", {"start": v(-33.9, -20.5) * mm, "end": v(-34.8, -19.36) * mm});
            skLineSegment(sketch, "E902.MirrorCS", {"start": v(-47.92, 0.97) * mm, "end": v(-48.52, 2.45) * mm});
            skLineSegment(sketch, "E903.MirrorCS", {"start": v(-17.2, 49.59) * mm, "end": v(-14.68, 48.75) * mm});
            skLineSegment(sketch, "E904.MirrorCS", {"start": v(-18.46, -36.46) * mm, "end": v(-19.47, -35.62) * mm});
            skLineSegment(sketch, "E905.MirrorCS", {"start": v(-29.15, -29.95) * mm, "end": v(-30.11, -28.91) * mm});
            skLineSegment(sketch, "E906.MirrorCS", {"start": v(29.25, -26.06) * mm, "end": v(28.28, -27.15) * mm});
            skLineSegment(sketch, "E907.MirrorCS", {"start": v(13.25, -40.47) * mm, "end": v(12.18, -41.23) * mm});
            skLineSegment(sketch, "E908.MirrorCS", {"start": v(48.32, 33.3) * mm, "end": v(49.4, 31.07) * mm});
            skLineSegment(sketch, "E909.MirrorCS", {"start": v(-11.64, 44.39) * mm, "end": v(-10.69, 43.78) * mm});
            skLineSegment(sketch, "E910.MirrorCS", {"start": v(-33, -21.62) * mm, "end": v(-33.9, -20.5) * mm});
            skLineSegment(sketch, "E911.MirrorCS", {"start": v(-47.27, -0.49) * mm, "end": v(-47.92, 0.97) * mm});
            skLineSegment(sketch, "E912.MirrorCS", {"start": v(-17.44, -37.29) * mm, "end": v(-18.46, -36.46) * mm});
            skLineSegment(sketch, "E913.MirrorCS", {"start": v(-28.19, -30.97) * mm, "end": v(-29.15, -29.95) * mm});
            skLineSegment(sketch, "E914.MirrorCS", {"start": v(28.19, -30.97) * mm, "end": v(27.2, -31.96) * mm});
            skLineSegment(sketch, "E915.MirrorCS", {"start": v(-11.44, -44.8) * mm, "end": v(-12.52, -44.08) * mm});
            skLineSegment(sketch, "E916.MirrorCS", {"start": v(30.2, -24.97) * mm, "end": v(29.25, -26.06) * mm});
            skLineSegment(sketch, "E917.MirrorCS", {"start": v(14.32, -39.7) * mm, "end": v(13.25, -40.47) * mm});
            skLineSegment(sketch, "E918.MirrorCS", {"start": v(47.06, 35.46) * mm, "end": v(48.32, 33.3) * mm});
            skLineSegment(sketch, "E919.MirrorCS", {"start": v(-12.62, 44.96) * mm, "end": v(-11.64, 44.39) * mm});
            skLineSegment(sketch, "E920.MirrorCS", {"start": v(-32.07, -22.74) * mm, "end": v(-33, -21.62) * mm});
            skLineSegment(sketch, "E921.MirrorCS", {"start": v(-46.57, -1.93) * mm, "end": v(-47.27, -0.49) * mm});
            skLineSegment(sketch, "E922.MirrorCS", {"start": v(-16.4, -38.1) * mm, "end": v(-17.44, -37.29) * mm});
            skLineSegment(sketch, "E923.MirrorCS", {"start": v(-27.2, -31.96) * mm, "end": v(-28.19, -30.97) * mm});
            skLineSegment(sketch, "E924.MirrorCS", {"start": v(-42.78, -13.05) * mm, "end": v(-43.75, -11.65) * mm});
            skLineSegment(sketch, "E925.MirrorCS", {"start": v(29.16, -29.95) * mm, "end": v(28.19, -30.97) * mm});
            skLineSegment(sketch, "E926.MirrorCS", {"start": v(12.52, -44.08) * mm, "end": v(11.44, -44.8) * mm});
            skLineSegment(sketch, "E927.MirrorCS", {"start": v(-10.38, -45.48) * mm, "end": v(-11.44, -44.8) * mm});
            skLineSegment(sketch, "E928.MirrorCS", {"start": v(52.69, 29.63) * mm, "end": v(53.36, 27.46) * mm});
            skLineSegment(sketch, "E929.MirrorCS", {"start": v(31.14, -23.86) * mm, "end": v(30.2, -24.97) * mm});
            skLineSegment(sketch, "E930.MirrorCS", {"start": v(15.37, -38.9) * mm, "end": v(14.32, -39.7) * mm});
            skLineSegment(sketch, "E931.MirrorCS", {"start": v(45.63, 37.51) * mm, "end": v(47.06, 35.46) * mm});
            skLineSegment(sketch, "E932.MirrorCS", {"start": v(-13.63, 45.5) * mm, "end": v(-12.62, 44.96) * mm});
            skLineSegment(sketch, "E933.MirrorCS", {"start": v(-31.14, -23.86) * mm, "end": v(-32.07, -22.74) * mm});
            skLineSegment(sketch, "E934.MirrorCS", {"start": v(-45.84, -3.35) * mm, "end": v(-46.57, -1.93) * mm});
            skLineSegment(sketch, "E935.MirrorCS", {"start": v(-15.37, -38.9) * mm, "end": v(-16.4, -38.1) * mm});
            skLineSegment(sketch, "E936.MirrorCS", {"start": v(-26.22, -32.94) * mm, "end": v(-27.2, -31.96) * mm});
            skLineSegment(sketch, "E937.MirrorCS", {"start": v(-41.8, -14.42) * mm, "end": v(-42.78, -13.05) * mm});
            skLineSegment(sketch, "E938.MirrorCS", {"start": v(-54.17, 23.44) * mm, "end": v(-53.84, 25.39) * mm});
            skLineSegment(sketch, "E939.MirrorCS", {"start": v(30.11, -28.91) * mm, "end": v(29.16, -29.95) * mm});
            skLineSegment(sketch, "E940.MirrorCS", {"start": v(13.6, -43.34) * mm, "end": v(12.52, -44.08) * mm});
            skLineSegment(sketch, "E941.MirrorCS", {"start": v(-9.34, -46.13) * mm, "end": v(-10.38, -45.48) * mm});
            skLineSegment(sketch, "E942.MirrorCS", {"start": v(51.8, 31.89) * mm, "end": v(52.69, 29.63) * mm});
            skLineSegment(sketch, "E943.MirrorCS", {"start": v(44.04, 39.44) * mm, "end": v(45.63, 37.51) * mm});
            skLineSegment(sketch, "E944.MirrorCS", {"start": v(-14.32, -39.7) * mm, "end": v(-15.37, -38.9) * mm});
            skLineSegment(sketch, "E945.MirrorCS", {"start": v(-30.2, -24.97) * mm, "end": v(-31.14, -23.86) * mm});
            skLineSegment(sketch, "E946.MirrorCS", {"start": v(-45.07, -4.76) * mm, "end": v(-45.84, -3.35) * mm});
            skLineSegment(sketch, "E947.MirrorCS", {"start": v(-52.78, 7.33) * mm, "end": v(-53.12, 8.61) * mm});
            skLineSegment(sketch, "E948.MirrorCS", {"start": v(-54.37, 21.63) * mm, "end": v(-54.17, 23.44) * mm});
            skLineSegment(sketch, "E949.MirrorCS", {"start": v(-8.32, -46.74) * mm, "end": v(-9.34, -46.13) * mm});
            skLineSegment(sketch, "E950.MirrorCS", {"start": v(-25.22, -33.9) * mm, "end": v(-26.22, -32.94) * mm});
            skLineSegment(sketch, "E951.MirrorCS", {"start": v(-40.8, -15.78) * mm, "end": v(-41.8, -14.42) * mm});
            skLineSegment(sketch, "E952.MirrorCS", {"start": v(31.06, -27.85) * mm, "end": v(30.11, -28.91) * mm});
            skLineSegment(sketch, "E953.MirrorCS", {"start": v(14.68, -42.57) * mm, "end": v(13.6, -43.34) * mm});
            skLineSegment(sketch, "E954.MirrorCS", {"start": v(50.72, 34.18) * mm, "end": v(51.8, 31.89) * mm});
            skLineSegment(sketch, "E955.MirrorCS", {"start": v(16.4, -38.1) * mm, "end": v(15.37, -38.9) * mm});
            skLineSegment(sketch, "E956.MirrorCS", {"start": v(32.07, -22.74) * mm, "end": v(31.14, -23.86) * mm});
            skLineSegment(sketch, "E957.MirrorCS", {"start": v(-15.7, 46.42) * mm, "end": v(-14.65, 45.98) * mm});
            skLineSegment(sketch, "E958.MirrorCS", {"start": v(-29.25, -26.06) * mm, "end": v(-30.2, -24.97) * mm});
            skLineSegment(sketch, "E959.MirrorCS", {"start": v(-44.26, -6.14) * mm, "end": v(-45.07, -4.76) * mm});
            skLineSegment(sketch, "E960.MirrorCS", {"start": v(-52.39, 5.96) * mm, "end": v(-52.78, 7.33) * mm});
            skLineSegment(sketch, "E961.MirrorCS", {"start": v(-54.47, 19.98) * mm, "end": v(-54.37, 21.63) * mm});
            skLineSegment(sketch, "E962.MirrorCS", {"start": v(-7.35, -47.3) * mm, "end": v(-8.32, -46.74) * mm});
            skLineSegment(sketch, "E963.MirrorCS", {"start": v(-24.2, -34.84) * mm, "end": v(-25.22, -33.9) * mm});
            skLineSegment(sketch, "E964.MirrorCS", {"start": v(32, -26.76) * mm, "end": v(31.06, -27.85) * mm});
            skLineSegment(sketch, "E965.MirrorCS", {"start": v(15.76, -41.79) * mm, "end": v(14.68, -42.57) * mm});
            skLineSegment(sketch, "E966.MirrorCS", {"start": v(17.44, -37.29) * mm, "end": v(16.4, -38.1) * mm});
            skLineSegment(sketch, "E967.MirrorCS", {"start": v(-28.28, -27.15) * mm, "end": v(-29.25, -26.06) * mm});
            skLineSegment(sketch, "E968.MirrorCS", {"start": v(-51.94, 4.52) * mm, "end": v(-52.39, 5.96) * mm});
            skLineSegment(sketch, "E969.MirrorCS", {"start": v(-54.5, 18.51) * mm, "end": v(-54.47, 19.98) * mm});
            skLineSegment(sketch, "E970.MirrorCS", {"start": v(32.95, -25.65) * mm, "end": v(32, -26.76) * mm});
            skLineSegment(sketch, "E971.MirrorCS", {"start": v(16.84, -40.98) * mm, "end": v(15.76, -41.79) * mm});
            skLineSegment(sketch, "E972.MirrorCS", {"start": v(47.9, 38.72) * mm, "end": v(49.42, 36.48) * mm});
            skLineSegment(sketch, "E973.MirrorCS", {"start": v(18.46, -36.46) * mm, "end": v(17.44, -37.29) * mm});
            skLineSegment(sketch, "E974.MirrorCS", {"start": v(-16.77, 46.8) * mm, "end": v(-15.7, 46.42) * mm});
            skLineSegment(sketch, "E975.MirrorCS", {"start": v(-51.44, 3.04) * mm, "end": v(-51.94, 4.52) * mm});
            skLineSegment(sketch, "E976.MirrorCS", {"start": v(17.92, -40.15) * mm, "end": v(16.84, -40.98) * mm});
            skLineSegment(sketch, "E977.MirrorCS", {"start": v(46.17, 40.88) * mm, "end": v(47.9, 38.72) * mm});
            skLineSegment(sketch, "E978.MirrorCS", {"start": v(19.47, -35.62) * mm, "end": v(18.46, -36.46) * mm});
            skLineSegment(sketch, "E979.MirrorCS", {"start": v(48.52, 2.45) * mm, "end": v(47.92, 0.97) * mm});
            skLineSegment(sketch, "E980.MirrorCS", {"start": v(-17.86, 47.14) * mm, "end": v(-16.77, 46.8) * mm});
            skLineSegment(sketch, "E981.MirrorCS", {"start": v(-11.1, -41.97) * mm, "end": v(-12.18, -41.23) * mm});
            skLineSegment(sketch, "E982.MirrorCS", {"start": v(-27.3, -28.21) * mm, "end": v(-28.28, -27.15) * mm});
            skLineSegment(sketch, "E983.MirrorCS", {"start": v(49.61, -1.47) * mm, "end": v(48.9, -2.96) * mm});
            skLineSegment(sketch, "E984.MirrorCS", {"start": v(18.99, -39.3) * mm, "end": v(17.92, -40.15) * mm});
            skLineSegment(sketch, "E985.MirrorCS", {"start": v(20.5, -34.74) * mm, "end": v(19.47, -35.62) * mm});
            skLineSegment(sketch, "E986.MirrorCS", {"start": v(48.96, 3.65) * mm, "end": v(48.52, 2.45) * mm});
            skLineSegment(sketch, "E987.MirrorCS", {"start": v(-20.38, 47.66) * mm, "end": v(-17.86, 47.14) * mm});
            skLineSegment(sketch, "E988.MirrorCS", {"start": v(-10.2, -42.57) * mm, "end": v(-11.1, -41.97) * mm});
            skLineSegment(sketch, "E989.MirrorCS", {"start": v(-26.37, -29.2) * mm, "end": v(-27.3, -28.21) * mm});
            skLineSegment(sketch, "E990.MirrorCS", {"start": v(-41.66, -10.2) * mm, "end": v(-42.57, -8.85) * mm});
            skLineSegment(sketch, "E991.MirrorCS", {"start": v(-50.89, 1.53) * mm, "end": v(-51.44, 3.04) * mm});
            skLineSegment(sketch, "E992.MirrorCS", {"start": v(50.28, 0.03) * mm, "end": v(49.61, -1.47) * mm});
            skLineSegment(sketch, "E993.MirrorCS", {"start": v(20.05, -38.44) * mm, "end": v(18.99, -39.3) * mm});
            skLineSegment(sketch, "E994.MirrorCS", {"start": v(21.5, -33.85) * mm, "end": v(20.5, -34.74) * mm});
            skLineSegment(sketch, "E995.MirrorCS", {"start": v(49.38, 4.85) * mm, "end": v(48.96, 3.65) * mm});
            skLineSegment(sketch, "E996.MirrorCS", {"start": v(36.83, -16.8) * mm, "end": v(35.82, -18.08) * mm});
            skLineSegment(sketch, "E997.MirrorCS", {"start": v(51.93, 19.51) * mm, "end": v(51.95, 17.92) * mm});
            skLineSegment(sketch, "E998.MirrorCS", {"start": v(-9.28, -43.17) * mm, "end": v(-10.2, -42.57) * mm});
            skLineSegment(sketch, "E999.MirrorCS", {"start": v(-25.43, -30.15) * mm, "end": v(-26.37, -29.2) * mm});
            skLineSegment(sketch, "E1000.MirrorCS", {"start": v(-40.73, -11.55) * mm, "end": v(-41.66, -10.2) * mm});
            skLineSegment(sketch, "E1001.MirrorCS", {"start": v(-50.28, 0.03) * mm, "end": v(-50.89, 1.53) * mm});
            skLineSegment(sketch, "E1002.MirrorCS", {"start": v(-35.82, -22.16) * mm, "end": v(-36.8, -20.94) * mm});
            skLineSegment(sketch, "E1003.MirrorCS", {"start": v(22.5, -32.95) * mm, "end": v(21.5, -33.85) * mm});
            skLineSegment(sketch, "E1004.MirrorCS", {"start": v(49.76, 6.07) * mm, "end": v(49.38, 4.85) * mm});
            skLineSegment(sketch, "E1005.MirrorCS", {"start": v(37.83, -15.5) * mm, "end": v(36.83, -16.8) * mm});
            skLineSegment(sketch, "E1006.MirrorCS", {"start": v(-50.47, 8.51) * mm, "end": v(-50.8, 9.74) * mm});
            skLineSegment(sketch, "E1007.MirrorCS", {"start": v(-51.5, 24.15) * mm, "end": v(-51.18, 25.68) * mm});
            skLineSegment(sketch, "E1008.MirrorCS", {"start": v(-24.47, -31.1) * mm, "end": v(-25.43, -30.15) * mm});
            skLineSegment(sketch, "E1009.MirrorCS", {"start": v(-39.78, -12.88) * mm, "end": v(-40.73, -11.55) * mm});
            skLineSegment(sketch, "E1010.MirrorCS", {"start": v(-49.61, -1.47) * mm, "end": v(-50.28, 0.03) * mm});
            skLineSegment(sketch, "E1011.MirrorCS", {"start": v(-5, 42.6) * mm, "end": v(-3.68, 41.44) * mm});
            skLineSegment(sketch, "E1012.MirrorCS", {"start": v(-18.99, -39.3) * mm, "end": v(-20.05, -38.44) * mm});
            skLineSegment(sketch, "E1013.MirrorCS", {"start": v(-34.85, -23.35) * mm, "end": v(-35.82, -22.16) * mm});
            skLineSegment(sketch, "E1014.MirrorCS", {"start": v(50.89, 1.53) * mm, "end": v(50.28, 0.03) * mm});
            skLineSegment(sketch, "E1015.MirrorCS", {"start": v(21.1, -37.56) * mm, "end": v(20.05, -38.44) * mm});
            skLineSegment(sketch, "E1016.MirrorCS", {"start": v(-50.13, 7.29) * mm, "end": v(-50.47, 8.51) * mm});
            skLineSegment(sketch, "E1017.MirrorCS", {"start": v(-51.71, 22.61) * mm, "end": v(-51.5, 24.15) * mm});
            skLineSegment(sketch, "E1018.MirrorCS", {"start": v(-6.94, 40.9) * mm, "end": v(-6.26, 40.32) * mm});
            skLineSegment(sketch, "E1019.MirrorCS", {"start": v(-7.42, -44.33) * mm, "end": v(-8.36, -43.75) * mm});
            skLineSegment(sketch, "E1020.MirrorCS", {"start": v(-23.5, -32.03) * mm, "end": v(-24.47, -31.1) * mm});
            skLineSegment(sketch, "E1021.MirrorCS", {"start": v(-38.81, -14.2) * mm, "end": v(-39.78, -12.88) * mm});
            skLineSegment(sketch, "E1022.MirrorCS", {"start": v(-48.9, -2.96) * mm, "end": v(-49.61, -1.47) * mm});
            skLineSegment(sketch, "E1023.MirrorCS", {"start": v(-6.53, 43.88) * mm, "end": v(-5, 42.6) * mm});
            skLineSegment(sketch, "E1024.MirrorCS", {"start": v(-17.92, -40.15) * mm, "end": v(-18.99, -39.3) * mm});
            skLineSegment(sketch, "E1025.MirrorCS", {"start": v(-33.9, -24.52) * mm, "end": v(-34.85, -23.35) * mm});
            skLineSegment(sketch, "E1026.MirrorCS", {"start": v(51.44, 3.04) * mm, "end": v(50.89, 1.53) * mm});
            skLineSegment(sketch, "E1027.MirrorCS", {"start": v(22.15, -36.67) * mm, "end": v(21.1, -37.56) * mm});
            skLineSegment(sketch, "E1028.MirrorCS", {"start": v(23.5, -32.03) * mm, "end": v(22.5, -32.95) * mm});
            skLineSegment(sketch, "E1029.MirrorCS", {"start": v(38.81, -14.2) * mm, "end": v(37.83, -15.5) * mm});
            skLineSegment(sketch, "E1030.MirrorCS", {"start": v(50.13, 7.29) * mm, "end": v(49.76, 6.07) * mm});
            skLineSegment(sketch, "E1031.MirrorCS", {"start": v(-49.76, 6.07) * mm, "end": v(-50.13, 7.29) * mm});
            skLineSegment(sketch, "E1032.MirrorCS", {"start": v(-51.86, 21.07) * mm, "end": v(-51.71, 22.61) * mm});
            skLineSegment(sketch, "E1033.MirrorCS", {"start": v(-7.62, 41.48) * mm, "end": v(-6.94, 40.9) * mm});
            skLineSegment(sketch, "E1034.MirrorCS", {"start": v(-6.48, -44.89) * mm, "end": v(-7.42, -44.33) * mm});
            skLineSegment(sketch, "E1035.MirrorCS", {"start": v(-22.5, -32.95) * mm, "end": v(-23.5, -32.03) * mm});
            skLineSegment(sketch, "E1036.MirrorCS", {"start": v(-48.14, -4.44) * mm, "end": v(-48.9, -2.96) * mm});
            skLineSegment(sketch, "E1037.MirrorCS", {"start": v(-8.27, 45.2) * mm, "end": v(-6.53, 43.88) * mm});
            skLineSegment(sketch, "E1038.MirrorCS", {"start": v(-32.95, -25.65) * mm, "end": v(-33.9, -24.52) * mm});
            skLineSegment(sketch, "E1039.MirrorCS", {"start": v(51.94, 4.52) * mm, "end": v(51.44, 3.04) * mm});
            skLineSegment(sketch, "E1040.MirrorCS", {"start": v(23.19, -35.76) * mm, "end": v(22.15, -36.67) * mm});
            skLineSegment(sketch, "E1041.MirrorCS", {"start": v(24.47, -31.1) * mm, "end": v(23.5, -32.03) * mm});
            skLineSegment(sketch, "E1042.MirrorCS", {"start": v(39.78, -12.88) * mm, "end": v(38.81, -14.2) * mm});
            skLineSegment(sketch, "E1043.MirrorCS", {"start": v(50.47, 8.51) * mm, "end": v(50.13, 7.29) * mm});
            skLineSegment(sketch, "E1044.MirrorCS", {"start": v(-21.5, -33.85) * mm, "end": v(-22.5, -32.95) * mm});
            skLineSegment(sketch, "E1045.MirrorCS", {"start": v(-47.33, -5.9) * mm, "end": v(-48.14, -4.44) * mm});
            skLineSegment(sketch, "E1046.MirrorCS", {"start": v(-10.21, 46.49) * mm, "end": v(-8.27, 45.2) * mm});
            skLineSegment(sketch, "E1047.MirrorCS", {"start": v(-32, -26.76) * mm, "end": v(-32.95, -25.65) * mm});
            skLineSegment(sketch, "E1048.MirrorCS", {"start": v(54.47, 19.98) * mm, "end": v(54.5, 18.51) * mm});
            skLineSegment(sketch, "E1049.MirrorCS", {"start": v(52.39, 5.96) * mm, "end": v(51.94, 4.52) * mm});
            skLineSegment(sketch, "E1050.MirrorCS", {"start": v(39.8, -17.1) * mm, "end": v(38.79, -18.41) * mm});
            skLineSegment(sketch, "E1051.MirrorCS", {"start": v(24.2, -34.84) * mm, "end": v(23.19, -35.76) * mm});
            skLineSegment(sketch, "E1052.MirrorCS", {"start": v(25.43, -30.15) * mm, "end": v(24.47, -31.1) * mm});
            skLineSegment(sketch, "E1053.MirrorCS", {"start": v(-49.38, 4.85) * mm, "end": v(-49.76, 6.07) * mm});
            skLineSegment(sketch, "E1054.MirrorCS", {"start": v(-51.93, 19.51) * mm, "end": v(-51.86, 21.07) * mm});
            skLineSegment(sketch, "E1055.MirrorCS", {"start": v(17.2, 49.59) * mm, "end": v(19.89, 50.15) * mm});
            skLineSegment(sketch, "E1056.MirrorCS", {"start": v(17.86, 47.14) * mm, "end": v(20.38, 47.66) * mm});
            skLineSegment(sketch, "E1057.MirrorCS", {"start": v(35.82, -18.08) * mm, "end": v(34.8, -19.36) * mm});
            skLineSegment(sketch, "E1058.MirrorCS", {"start": v(40.73, -11.55) * mm, "end": v(39.78, -12.88) * mm});
            skLineSegment(sketch, "E1059.MirrorCS", {"start": v(28.57, 50.17) * mm, "end": v(31.5, 49.62) * mm});
            skLineSegment(sketch, "E1060.MirrorCS", {"start": v(25.63, 50.44) * mm, "end": v(28.57, 50.17) * mm});
            skLineSegment(sketch, "E1061.MirrorCS", {"start": v(22.71, 50.44) * mm, "end": v(25.63, 50.44) * mm});
            skLineSegment(sketch, "E1062.MirrorCS", {"start": v(19.89, 50.15) * mm, "end": v(22.71, 50.44) * mm});
            skLineSegment(sketch, "E1063.MirrorCS", {"start": v(37.11, 47.71) * mm, "end": v(39.7, 46.35) * mm});
            skLineSegment(sketch, "E1064.MirrorCS", {"start": v(34.37, 48.8) * mm, "end": v(37.11, 47.71) * mm});
            skLineSegment(sketch, "E1065.MirrorCS", {"start": v(31.5, 49.62) * mm, "end": v(34.37, 48.8) * mm});
            skLineSegment(sketch, "E1066.MirrorCS", {"start": v(41.66, -10.2) * mm, "end": v(40.73, -11.55) * mm});
            skLineSegment(sketch, "E1067.MirrorCS", {"start": v(50.79, 27.23) * mm, "end": v(51.18, 25.68) * mm});
            skLineSegment(sketch, "E1068.MirrorCS", {"start": v(20.38, 47.66) * mm, "end": v(23, 47.91) * mm});
            skLineSegment(sketch, "E1069.MirrorCS", {"start": v(-35.82, -18.08) * mm, "end": v(-36.83, -16.8) * mm});
            skLineSegment(sketch, "E1070.MirrorCS", {"start": v(-36.1, 45.38) * mm, "end": v(-33.65, 46.36) * mm});
            skLineSegment(sketch, "E1071.MirrorCS", {"start": v(-20.5, -34.74) * mm, "end": v(-21.5, -33.85) * mm});
            skLineSegment(sketch, "E1072.MirrorCS", {"start": v(-50.72, 34.18) * mm, "end": v(-49.42, 36.48) * mm});
            skLineSegment(sketch, "E1073.MirrorCS", {"start": v(-14.68, -42.57) * mm, "end": v(-15.76, -41.79) * mm});
            skLineSegment(sketch, "E1074.MirrorCS", {"start": v(54.37, 21.63) * mm, "end": v(54.47, 19.98) * mm});
            skLineSegment(sketch, "E1075.MirrorCS", {"start": v(42.57, -8.85) * mm, "end": v(41.66, -10.2) * mm});
            skLineSegment(sketch, "E1076.MirrorCS", {"start": v(-38.39, 44.18) * mm, "end": v(-36.1, 45.38) * mm});
            skLineSegment(sketch, "E1077.MirrorCS", {"start": v(-19.47, -35.62) * mm, "end": v(-20.5, -34.74) * mm});
            skLineSegment(sketch, "E1078.MirrorCS", {"start": v(-30.11, -28.91) * mm, "end": v(-31.06, -27.85) * mm});
            skLineSegment(sketch, "E1079.MirrorCS", {"start": v(-45.6, -8.81) * mm, "end": v(-46.5, -7.37) * mm});
            skLineSegment(sketch, "E1080.MirrorCS", {"start": v(-51.8, 31.89) * mm, "end": v(-50.72, 34.18) * mm});
            skLineSegment(sketch, "E1081.MirrorCS", {"start": v(-13.6, -43.34) * mm, "end": v(-14.68, -42.57) * mm});
            skLineSegment(sketch, "E1082.MirrorCS", {"start": v(54.17, 23.44) * mm, "end": v(54.37, 21.63) * mm});
            skLineSegment(sketch, "E1083.MirrorCS", {"start": v(41.8, -14.42) * mm, "end": v(40.8, -15.78) * mm});
            skLineSegment(sketch, "E1084.MirrorCS", {"start": v(43.43, -7.5) * mm, "end": v(42.57, -8.85) * mm});
            skLineSegment(sketch, "E1085.MirrorCS", {"start": v(-40.41, 42.8) * mm, "end": v(-38.39, 44.18) * mm});
            skLineSegment(sketch, "E1086.MirrorCS", {"start": v(-44.7, -10.24) * mm, "end": v(-45.6, -8.81) * mm});
            skLineSegment(sketch, "E1087.MirrorCS", {"start": v(-52.69, 29.63) * mm, "end": v(-51.8, 31.89) * mm});
            skLineSegment(sketch, "E1088.MirrorCS", {"start": v(27.2, -31.96) * mm, "end": v(26.22, -32.94) * mm});
            skLineSegment(sketch, "E1089.MirrorCS", {"start": v(-12.52, -44.08) * mm, "end": v(-13.6, -43.34) * mm});
            skLineSegment(sketch, "E1090.MirrorCS", {"start": v(53.84, 25.39) * mm, "end": v(54.17, 23.44) * mm});
            skLineSegment(sketch, "E1091.MirrorCS", {"start": v(42.78, -13.05) * mm, "end": v(41.8, -14.42) * mm});
            skLineSegment(sketch, "E1092.MirrorCS", {"start": v(44.26, -6.14) * mm, "end": v(43.43, -7.5) * mm});
            skLineSegment(sketch, "E1093.MirrorCS", {"start": v(-42.3, 41.22) * mm, "end": v(-40.41, 42.8) * mm});
            skLineSegment(sketch, "E1094.MirrorCS", {"start": v(-19.89, 50.15) * mm, "end": v(-17.2, 49.59) * mm});
            skLineSegment(sketch, "E1095.MirrorCS", {"start": v(-43.75, -11.65) * mm, "end": v(-44.7, -10.24) * mm});
            skLineSegment(sketch, "E1096.MirrorCS", {"start": v(-53.36, 27.46) * mm, "end": v(-52.69, 29.63) * mm});
            skLineSegment(sketch, "E1097.MirrorCS", {"start": v(53.36, 27.46) * mm, "end": v(53.84, 25.39) * mm});
            skLineSegment(sketch, "E1098.MirrorCS", {"start": v(43.75, -11.65) * mm, "end": v(42.78, -13.05) * mm});
            skLineSegment(sketch, "E1099.MirrorCS", {"start": v(45.07, -4.76) * mm, "end": v(44.26, -6.14) * mm});
            skLineSegment(sketch, "E1100.MirrorCS", {"start": v(-44.04, 39.44) * mm, "end": v(-42.3, 41.22) * mm});
            skLineSegment(sketch, "E1101.MirrorCS", {"start": v(-22.71, 50.44) * mm, "end": v(-19.89, 50.15) * mm});
            skLineSegment(sketch, "E1102.MirrorCS", {"start": v(-53.84, 25.39) * mm, "end": v(-53.36, 27.46) * mm});
            skLineSegment(sketch, "E1103.MirrorCS", {"start": v(44.7, -10.24) * mm, "end": v(43.75, -11.65) * mm});
            skLineSegment(sketch, "E1104.MirrorCS", {"start": v(45.84, -3.35) * mm, "end": v(45.07, -4.76) * mm});
            skLineSegment(sketch, "E1105.MirrorCS", {"start": v(-45.63, 37.51) * mm, "end": v(-44.04, 39.44) * mm});
            skLineSegment(sketch, "E1106.MirrorCS", {"start": v(-25.63, 50.44) * mm, "end": v(-22.71, 50.44) * mm});
            skLineSegment(sketch, "E1107.MirrorCS", {"start": v(45.6, -8.81) * mm, "end": v(44.7, -10.24) * mm});
            skLineSegment(sketch, "E1108.MirrorCS", {"start": v(-47.06, 35.46) * mm, "end": v(-45.63, 37.51) * mm});
            skLineSegment(sketch, "E1109.MirrorCS", {"start": v(-28.57, 50.17) * mm, "end": v(-25.63, 50.44) * mm});
            skLineSegment(sketch, "E1110.MirrorCS", {"start": v(46.5, -7.37) * mm, "end": v(45.6, -8.81) * mm});
            skLineSegment(sketch, "E1111.MirrorCS", {"start": v(46.57, -1.93) * mm, "end": v(45.84, -3.35) * mm});
            skLineSegment(sketch, "E1112.MirrorCS", {"start": v(-48.32, 33.3) * mm, "end": v(-47.06, 35.46) * mm});
            skLineSegment(sketch, "E1113.MirrorCS", {"start": v(-13.25, -40.47) * mm, "end": v(-14.32, -39.7) * mm});
            skLineSegment(sketch, "E1114.MirrorCS", {"start": v(-31.5, 49.62) * mm, "end": v(-28.57, 50.17) * mm});
            skLineSegment(sketch, "E1115.MirrorCS", {"start": v(-39.8, -17.1) * mm, "end": v(-40.8, -15.78) * mm});
            skLineSegment(sketch, "E1116.MirrorCS", {"start": v(47.33, -5.9) * mm, "end": v(46.5, -7.37) * mm});
            skLineSegment(sketch, "E1117.MirrorCS", {"start": v(49.42, 36.48) * mm, "end": v(50.72, 34.18) * mm});
            skLineSegment(sketch, "E1118.MirrorCS", {"start": v(47.27, -0.49) * mm, "end": v(46.57, -1.93) * mm});
            skLineSegment(sketch, "E1119.MirrorCS", {"start": v(33, -21.62) * mm, "end": v(32.07, -22.74) * mm});
            skLineSegment(sketch, "E1120.MirrorCS", {"start": v(42.3, 41.22) * mm, "end": v(44.04, 39.44) * mm});
            skLineSegment(sketch, "E1121.MirrorCS", {"start": v(-12.18, -41.23) * mm, "end": v(-13.25, -40.47) * mm});
            skLineSegment(sketch, "E1122.MirrorCS", {"start": v(-43.43, -7.5) * mm, "end": v(-44.26, -6.14) * mm});
            skLineSegment(sketch, "E1123.MirrorCS", {"start": v(-34.37, 48.8) * mm, "end": v(-31.5, 49.62) * mm});
            skLineSegment(sketch, "E1124.MirrorCS", {"start": v(-23.19, -35.76) * mm, "end": v(-24.2, -34.84) * mm});
            skLineSegment(sketch, "E1125.MirrorCS", {"start": v(-38.79, -18.41) * mm, "end": v(-39.8, -17.1) * mm});
            skLineSegment(sketch, "E1126.MirrorCS", {"start": v(48.14, -4.44) * mm, "end": v(47.33, -5.9) * mm});
            skLineSegment(sketch, "E1127.MirrorCS", {"start": v(47.92, 0.97) * mm, "end": v(47.27, -0.49) * mm});
            skLineSegment(sketch, "E1128.MirrorCS", {"start": v(33.9, -20.5) * mm, "end": v(33, -21.62) * mm});
            skLineSegment(sketch, "E1129.MirrorCS", {"start": v(40.41, 42.8) * mm, "end": v(42.3, 41.22) * mm});
            skLineSegment(sketch, "E1130.MirrorCS", {"start": v(-49.4, 31.07) * mm, "end": v(-48.32, 33.3) * mm});
            skLineSegment(sketch, "E1131.MirrorCS", {"start": v(-37.11, 47.71) * mm, "end": v(-34.37, 48.8) * mm});
            skLineSegment(sketch, "E1132.MirrorCS", {"start": v(-22.15, -36.67) * mm, "end": v(-23.19, -35.76) * mm});
            skLineSegment(sketch, "E1133.MirrorCS", {"start": v(-37.79, -19.7) * mm, "end": v(-38.79, -18.41) * mm});
            skLineSegment(sketch, "E1134.MirrorCS", {"start": v(48.9, -2.96) * mm, "end": v(48.14, -4.44) * mm});
            skLineSegment(sketch, "E1135.MirrorCS", {"start": v(33.9, -24.52) * mm, "end": v(32.95, -25.65) * mm});
            skLineSegment(sketch, "E1136.MirrorCS", {"start": v(34.8, -19.36) * mm, "end": v(33.9, -20.5) * mm});
            skLineSegment(sketch, "E1137.MirrorCS", {"start": v(38.39, 44.18) * mm, "end": v(40.41, 42.8) * mm});
            skLineSegment(sketch, "E1138.MirrorCS", {"start": v(-50.29, 28.8) * mm, "end": v(-49.4, 31.07) * mm});
            skLineSegment(sketch, "E1139.MirrorCS", {"start": v(-42.57, -8.85) * mm, "end": v(-43.43, -7.5) * mm});
            skLineSegment(sketch, "E1140.MirrorCS", {"start": v(-21.1, -37.56) * mm, "end": v(-22.15, -36.67) * mm});
            skLineSegment(sketch, "E1141.MirrorCS", {"start": v(-36.8, -20.94) * mm, "end": v(-37.79, -19.7) * mm});
            skLineSegment(sketch, "E1142.MirrorCS", {"start": v(34.85, -23.35) * mm, "end": v(33.9, -24.52) * mm});
            skLineSegment(sketch, "E1143.MirrorCS", {"start": v(44.23, 42.9) * mm, "end": v(46.17, 40.88) * mm});
            skLineSegment(sketch, "E1144.MirrorCS", {"start": v(36.1, 45.38) * mm, "end": v(38.39, 44.18) * mm});
            skLineSegment(sketch, "E1145.MirrorCS", {"start": v(-50.79, 27.23) * mm, "end": v(-50.29, 28.8) * mm});
            skLineSegment(sketch, "E1146.MirrorCS", {"start": v(-39.7, 46.35) * mm, "end": v(-37.11, 47.71) * mm});
            skLineSegment(sketch, "E1147.MirrorCS", {"start": v(35.82, -22.16) * mm, "end": v(34.85, -23.35) * mm});
            skLineSegment(sketch, "E1148.MirrorCS", {"start": v(42.07, 44.74) * mm, "end": v(44.23, 42.9) * mm});
            skLineSegment(sketch, "E1149.MirrorCS", {"start": v(33.65, 46.36) * mm, "end": v(36.1, 45.38) * mm});
            skLineSegment(sketch, "E1150.MirrorCS", {"start": v(-51.18, 25.68) * mm, "end": v(-50.79, 27.23) * mm});
            skLineSegment(sketch, "E1151.MirrorCS", {"start": v(-23, 47.91) * mm, "end": v(-20.38, 47.66) * mm});
            skLineSegment(sketch, "E1152.MirrorCS", {"start": v(-42.07, 44.74) * mm, "end": v(-39.7, 46.35) * mm});
            skLineSegment(sketch, "E1153.MirrorCS", {"start": v(-20.05, -38.44) * mm, "end": v(-21.1, -37.56) * mm});
            skLineSegment(sketch, "E1154.MirrorCS", {"start": v(39.7, 46.35) * mm, "end": v(42.07, 44.74) * mm});
            skLineSegment(sketch, "E1155.MirrorCS", {"start": v(31.06, 47.12) * mm, "end": v(33.65, 46.36) * mm});
            skLineSegment(sketch, "E1156.MirrorCS", {"start": v(51.86, 21.07) * mm, "end": v(51.93, 19.51) * mm});
            skLineSegment(sketch, "E1157.MirrorCS", {"start": v(-25.7, 47.9) * mm, "end": v(-23, 47.91) * mm});
            skLineSegment(sketch, "E1158.MirrorCS", {"start": v(-44.23, 42.9) * mm, "end": v(-42.07, 44.74) * mm});
            skLineSegment(sketch, "E1159.MirrorCS", {"start": v(36.8, -20.94) * mm, "end": v(35.82, -22.16) * mm});
            skLineSegment(sketch, "E1160.MirrorCS", {"start": v(28.4, 47.63) * mm, "end": v(31.06, 47.12) * mm});
            skLineSegment(sketch, "E1161.MirrorCS", {"start": v(51.71, 22.61) * mm, "end": v(51.86, 21.07) * mm});
            skLineSegment(sketch, "E1162.MirrorCS", {"start": v(-28.4, 47.63) * mm, "end": v(-25.7, 47.9) * mm});
            skLineSegment(sketch, "E1163.MirrorCS", {"start": v(-46.17, 40.88) * mm, "end": v(-44.23, 42.9) * mm});
            skLineSegment(sketch, "E1164.MirrorCS", {"start": v(37.79, -19.7) * mm, "end": v(36.8, -20.94) * mm});
            skLineSegment(sketch, "E1165.MirrorCS", {"start": v(-31.06, 47.12) * mm, "end": v(-28.4, 47.63) * mm});
            skLineSegment(sketch, "E1166.MirrorCS", {"start": v(-37.83, -15.5) * mm, "end": v(-38.81, -14.2) * mm});
            skLineSegment(sketch, "E1167.MirrorCS", {"start": v(-47.9, 38.72) * mm, "end": v(-46.17, 40.88) * mm});
            skLineSegment(sketch, "E1168.MirrorCS", {"start": v(-16.84, -40.98) * mm, "end": v(-17.92, -40.15) * mm});
            skLineSegment(sketch, "E1169.MirrorCS", {"start": v(38.79, -18.41) * mm, "end": v(37.79, -19.7) * mm});
            skLineSegment(sketch, "E1170.MirrorCS", {"start": v(25.7, 47.9) * mm, "end": v(28.4, 47.63) * mm});
            skLineSegment(sketch, "E1171.MirrorCS", {"start": v(51.5, 24.15) * mm, "end": v(51.71, 22.61) * mm});
            skLineSegment(sketch, "E1172.MirrorCS", {"start": v(-36.83, -16.8) * mm, "end": v(-37.83, -15.5) * mm});
            skLineSegment(sketch, "E1173.MirrorCS", {"start": v(-49.42, 36.48) * mm, "end": v(-47.9, 38.72) * mm});
            skLineSegment(sketch, "E1174.MirrorCS", {"start": v(-15.76, -41.79) * mm, "end": v(-16.84, -40.98) * mm});
            skLineSegment(sketch, "E1175.MirrorCS", {"start": v(23, 47.91) * mm, "end": v(25.7, 47.9) * mm});
            skLineSegment(sketch, "E1176.MirrorCS", {"start": v(-33.65, 46.36) * mm, "end": v(-31.06, 47.12) * mm});
            skLineSegment(sketch, "E1177.MirrorCS", {"start": v(51.18, 25.68) * mm, "end": v(51.5, 24.15) * mm});
            skSolve(sketch);
        }
        {
            var Q0;
            Q0 = qSketchRegion(id + "F3", true);
            extrude(context, id + "F4", {"entities" : qUnion([Q0]), "operationType" : NewBodyOperationType.ADD, "depth" : 3 * mm});
        }
        {
            var Q0;
            Q0=makeQuery(id+"F2.opShell","OFFSET_FACE",FACE,{"disambiguationData":[OSD([sQuery(id+"F0.wireOp",EDGE,"E0"),sQuery(id+"F0.wireOp",EDGE,"E1"),sQuery(id+"F0.wireOp",EDGE,"E2"),sQuery(id+"F0.wireOp",EDGE,"E3"),sQuery(id+"F0.wireOp",EDGE,"E4"),sQuery(id+"F0.wireOp",EDGE,"E5"),sQuery(id+"F0.wireOp",EDGE,"E6"),sQuery(id+"F0.wireOp",EDGE,"E7"),sQuery(id+"F0.wireOp",EDGE,"E8"),sQuery(id+"F0.wireOp",EDGE,"E9"),sQuery(id+"F0.wireOp",EDGE,"E10"),sQuery(id+"F0.wireOp",EDGE,"E11"),sQuery(id+"F0.wireOp",EDGE,"E12"),sQuery(id+"F0.wireOp",EDGE,"E13"),sQuery(id+"F0.wireOp",EDGE,"E14"),sQuery(id+"F0.wireOp",EDGE,"E15"),sQuery(id+"F0.wireOp",EDGE,"E16"),sQuery(id+"F0.wireOp",EDGE,"E17"),sQuery(id+"F0.wireOp",EDGE,"E18"),sQuery(id+"F0.wireOp",EDGE,"E19"),sQuery(id+"F0.wireOp",EDGE,"E20"),sQuery(id+"F0.wireOp",EDGE,"E21"),sQuery(id+"F0.wireOp",EDGE,"E22"),sQuery(id+"F0.wireOp",EDGE,"E23"),sQuery(id+"F0.wireOp",EDGE,"E24"),sQuery(id+"F0.wireOp",EDGE,"E25"),sQuery(id+"F0.wireOp",EDGE,"E26"),sQuery(id+"F0.wireOp",EDGE,"E27"),sQuery(id+"F0.wireOp",EDGE,"E28"),sQuery(id+"F0.wireOp",EDGE,"E29"),sQuery(id+"F0.wireOp",EDGE,"E30"),sQuery(id+"F0.wireOp",EDGE,"E31"),sQuery(id+"F0.wireOp",EDGE,"E32"),sQuery(id+"F0.wireOp",EDGE,"E33"),sQuery(id+"F0.wireOp",EDGE,"E34"),sQuery(id+"F0.wireOp",EDGE,"E35"),sQuery(id+"F0.wireOp",EDGE,"E36"),sQuery(id+"F0.wireOp",EDGE,"E37"),sQuery(id+"F0.wireOp",EDGE,"E38"),sQuery(id+"F0.wireOp",EDGE,"E39"),sQuery(id+"F0.wireOp",EDGE,"E40"),sQuery(id+"F0.wireOp",EDGE,"E41"),sQuery(id+"F0.wireOp",EDGE,"E42"),sQuery(id+"F0.wireOp",EDGE,"E43"),sQuery(id+"F0.wireOp",EDGE,"E44"),sQuery(id+"F0.wireOp",EDGE,"E45"),sQuery(id+"F0.wireOp",EDGE,"E46"),sQuery(id+"F0.wireOp",EDGE,"E47"),sQuery(id+"F0.wireOp",EDGE,"E48"),sQuery(id+"F0.wireOp",EDGE,"E49"),sQuery(id+"F0.wireOp",EDGE,"E50"),sQuery(id+"F0.wireOp",EDGE,"E51"),sQuery(id+"F0.wireOp",EDGE,"E52"),sQuery(id+"F0.wireOp",EDGE,"E53"),sQuery(id+"F0.wireOp",EDGE,"E54"),sQuery(id+"F0.wireOp",EDGE,"E55"),sQuery(id+"F0.wireOp",EDGE,"E56"),sQuery(id+"F0.wireOp",EDGE,"E57"),sQuery(id+"F0.wireOp",EDGE,"E58"),sQuery(id+"F0.wireOp",EDGE,"E59"),sQuery(id+"F0.wireOp",EDGE,"E60"),sQuery(id+"F0.wireOp",EDGE,"E61"),sQuery(id+"F0.wireOp",EDGE,"E62"),sQuery(id+"F0.wireOp",EDGE,"E63"),sQuery(id+"F0.wireOp",EDGE,"E64"),sQuery(id+"F0.wireOp",EDGE,"E65"),sQuery(id+"F0.wireOp",EDGE,"E66"),sQuery(id+"F0.wireOp",EDGE,"E67"),sQuery(id+"F0.wireOp",EDGE,"E68"),sQuery(id+"F0.wireOp",EDGE,"E69"),sQuery(id+"F0.wireOp",EDGE,"E70"),sQuery(id+"F0.wireOp",EDGE,"E71"),sQuery(id+"F0.wireOp",EDGE,"E72"),sQuery(id+"F0.wireOp",EDGE,"E73"),sQuery(id+"F0.wireOp",EDGE,"E74"),sQuery(id+"F0.wireOp",EDGE,"E75"),sQuery(id+"F0.wireOp",EDGE,"E76"),sQuery(id+"F0.wireOp",EDGE,"E77"),sQuery(id+"F0.wireOp",EDGE,"E78"),sQuery(id+"F0.wireOp",EDGE,"E79"),sQuery(id+"F0.wireOp",EDGE,"E80"),sQuery(id+"F0.wireOp",EDGE,"E81"),sQuery(id+"F0.wireOp",EDGE,"E82"),sQuery(id+"F0.wireOp",EDGE,"E83"),sQuery(id+"F0.wireOp",EDGE,"E84"),sQuery(id+"F0.wireOp",EDGE,"E85"),sQuery(id+"F0.wireOp",EDGE,"E86"),sQuery(id+"F0.wireOp",EDGE,"E87"),sQuery(id+"F0.wireOp",EDGE,"E88"),sQuery(id+"F0.wireOp",EDGE,"E89"),sQuery(id+"F0.wireOp",EDGE,"E90"),sQuery(id+"F0.wireOp",EDGE,"E91"),sQuery(id+"F0.wireOp",EDGE,"E92"),sQuery(id+"F0.wireOp",EDGE,"E93"),sQuery(id+"F0.wireOp",EDGE,"E94"),sQuery(id+"F0.wireOp",EDGE,"E95"),sQuery(id+"F0.wireOp",EDGE,"E96"),sQuery(id+"F0.wireOp",EDGE,"E97"),sQuery(id+"F0.wireOp",EDGE,"E98"),sQuery(id+"F0.wireOp",EDGE,"E99"),sQuery(id+"F0.wireOp",EDGE,"E100"),sQuery(id+"F0.wireOp",EDGE,"E101"),sQuery(id+"F0.wireOp",EDGE,"E102"),sQuery(id+"F0.wireOp",EDGE,"E103"),sQuery(id+"F0.wireOp",EDGE,"E104"),sQuery(id+"F0.wireOp",EDGE,"E105"),sQuery(id+"F0.wireOp",EDGE,"E106"),sQuery(id+"F0.wireOp",EDGE,"E107"),sQuery(id+"F0.wireOp",EDGE,"E108"),sQuery(id+"F0.wireOp",EDGE,"E109"),sQuery(id+"F0.wireOp",EDGE,"E110"),sQuery(id+"F0.wireOp",EDGE,"E111"),sQuery(id+"F0.wireOp",EDGE,"E112"),sQuery(id+"F0.wireOp",EDGE,"E113"),sQuery(id+"F0.wireOp",EDGE,"E114"),sQuery(id+"F0.wireOp",EDGE,"E115"),sQuery(id+"F0.wireOp",EDGE,"E116"),sQuery(id+"F0.wireOp",EDGE,"E117"),sQuery(id+"F0.wireOp",EDGE,"E118"),sQuery(id+"F0.wireOp",EDGE,"E119"),sQuery(id+"F0.wireOp",EDGE,"E120"),sQuery(id+"F0.wireOp",EDGE,"E121"),sQuery(id+"F0.wireOp",EDGE,"E122"),sQuery(id+"F0.wireOp",EDGE,"E123"),sQuery(id+"F0.wireOp",EDGE,"E124"),sQuery(id+"F0.wireOp",EDGE,"E125"),sQuery(id+"F0.wireOp",EDGE,"E126"),sQuery(id+"F0.wireOp",EDGE,"E127"),sQuery(id+"F0.wireOp",EDGE,"E128"),sQuery(id+"F0.wireOp",EDGE,"E129"),sQuery(id+"F0.wireOp",EDGE,"E130"),sQuery(id+"F0.wireOp",EDGE,"E131"),sQuery(id+"F0.wireOp",EDGE,"E132"),sQuery(id+"F0.wireOp",EDGE,"E133"),sQuery(id+"F0.wireOp",EDGE,"E134"),sQuery(id+"F0.wireOp",EDGE,"E135"),sQuery(id+"F0.wireOp",EDGE,"E136"),sQuery(id+"F0.wireOp",EDGE,"E137"),sQuery(id+"F0.wireOp",EDGE,"E138"),sQuery(id+"F0.wireOp",EDGE,"E139"),sQuery(id+"F0.wireOp",EDGE,"E140"),sQuery(id+"F0.wireOp",EDGE,"E141"),sQuery(id+"F0.wireOp",EDGE,"E142"),sQuery(id+"F0.wireOp",EDGE,"E143"),sQuery(id+"F0.wireOp",EDGE,"E144"),sQuery(id+"F0.wireOp",EDGE,"E145"),sQuery(id+"F0.wireOp",EDGE,"E146"),sQuery(id+"F0.wireOp",EDGE,"E147"),sQuery(id+"F0.wireOp",EDGE,"E148"),sQuery(id+"F0.wireOp",EDGE,"E149"),sQuery(id+"F0.wireOp",EDGE,"E150"),sQuery(id+"F0.wireOp",EDGE,"E151"),sQuery(id+"F0.wireOp",EDGE,"E152"),sQuery(id+"F0.wireOp",EDGE,"E153"),sQuery(id+"F0.wireOp",EDGE,"E154"),sQuery(id+"F0.wireOp",EDGE,"E155"),sQuery(id+"F0.wireOp",EDGE,"E156"),sQuery(id+"F0.wireOp",EDGE,"E157"),sQuery(id+"F0.wireOp",EDGE,"E158"),sQuery(id+"F0.wireOp",EDGE,"E159"),sQuery(id+"F0.wireOp",EDGE,"E160"),sQuery(id+"F0.wireOp",EDGE,"E161"),sQuery(id+"F0.wireOp",EDGE,"E162"),sQuery(id+"F0.wireOp",EDGE,"E163"),sQuery(id+"F0.wireOp",EDGE,"E164"),sQuery(id+"F0.wireOp",EDGE,"E165"),sQuery(id+"F0.wireOp",EDGE,"E166"),sQuery(id+"F0.wireOp",EDGE,"E167"),sQuery(id+"F0.wireOp",EDGE,"E168"),sQuery(id+"F0.wireOp",EDGE,"E169"),sQuery(id+"F0.wireOp",EDGE,"E170"),sQuery(id+"F0.wireOp",EDGE,"E171"),sQuery(id+"F0.wireOp",EDGE,"E172"),sQuery(id+"F0.wireOp",EDGE,"E173"),sQuery(id+"F0.wireOp",EDGE,"E174"),sQuery(id+"F0.wireOp",EDGE,"E175"),sQuery(id+"F0.wireOp",EDGE,"E176"),sQuery(id+"F0.wireOp",EDGE,"E177"),sQuery(id+"F0.wireOp",EDGE,"E178"),sQuery(id+"F0.wireOp",EDGE,"E179"),sQuery(id+"F0.wireOp",EDGE,"E180"),sQuery(id+"F0.wireOp",EDGE,"E181"),sQuery(id+"F0.wireOp",EDGE,"E182"),sQuery(id+"F0.wireOp",EDGE,"E183"),sQuery(id+"F0.wireOp",EDGE,"E184"),sQuery(id+"F0.wireOp",EDGE,"E185"),sQuery(id+"F0.wireOp",EDGE,"E186"),sQuery(id+"F0.wireOp",EDGE,"E187"),sQuery(id+"F0.wireOp",EDGE,"E188"),sQuery(id+"F0.wireOp",EDGE,"E189"),sQuery(id+"F0.wireOp",EDGE,"E190"),sQuery(id+"F0.wireOp",EDGE,"E191"),sQuery(id+"F0.wireOp",EDGE,"E192"),sQuery(id+"F0.wireOp",EDGE,"E193"),sQuery(id+"F0.wireOp",EDGE,"E194"),sQuery(id+"F0.wireOp",EDGE,"E195"),sQuery(id+"F0.wireOp",EDGE,"E196"),sQuery(id+"F0.wireOp",EDGE,"E197"),sQuery(id+"F0.wireOp",EDGE,"E198"),sQuery(id+"F0.wireOp",EDGE,"E199"),sQuery(id+"F0.wireOp",EDGE,"E200"),sQuery(id+"F0.wireOp",EDGE,"E201"),sQuery(id+"F0.wireOp",EDGE,"E202"),sQuery(id+"F0.wireOp",EDGE,"E203"),sQuery(id+"F0.wireOp",EDGE,"E204"),sQuery(id+"F0.wireOp",EDGE,"E205"),sQuery(id+"F0.wireOp",EDGE,"E206"),sQuery(id+"F0.wireOp",EDGE,"E207"),sQuery(id+"F0.wireOp",EDGE,"E208"),sQuery(id+"F0.wireOp",EDGE,"E209"),sQuery(id+"F0.wireOp",EDGE,"E210"),sQuery(id+"F0.wireOp",EDGE,"E211"),sQuery(id+"F0.wireOp",EDGE,"E212"),sQuery(id+"F0.wireOp",EDGE,"E213"),sQuery(id+"F0.wireOp",EDGE,"E214"),sQuery(id+"F0.wireOp",EDGE,"E215"),sQuery(id+"F0.wireOp",EDGE,"E216"),sQuery(id+"F0.wireOp",EDGE,"E217"),sQuery(id+"F0.wireOp",EDGE,"E218"),sQuery(id+"F0.wireOp",EDGE,"E219"),sQuery(id+"F0.wireOp",EDGE,"E220"),sQuery(id+"F0.wireOp",EDGE,"E221"),sQuery(id+"F0.wireOp",EDGE,"E222"),sQuery(id+"F0.wireOp",EDGE,"E223"),sQuery(id+"F0.wireOp",EDGE,"E224"),sQuery(id+"F0.wireOp",EDGE,"E225")])]});
            extrude(context, id + "F5", {"entities" : qUnion([Q0]), "operationType" : NewBodyOperationType.REMOVE, "oppositeDirection" : true, "depth" : 3.1 * mm});
        }
        {
            var Q0;
            Q0=makeQuery(id+"F1.opExtrude","CAP_FACE",FACE,{"disambiguationData":[OSD([sQuery(id+"F0.wireOp",EDGE,"E0"),sQuery(id+"F0.wireOp",EDGE,"E1"),sQuery(id+"F0.wireOp",EDGE,"E2"),sQuery(id+"F0.wireOp",EDGE,"E3"),sQuery(id+"F0.wireOp",EDGE,"E4"),sQuery(id+"F0.wireOp",EDGE,"E5"),sQuery(id+"F0.wireOp",EDGE,"E6"),sQuery(id+"F0.wireOp",EDGE,"E7"),sQuery(id+"F0.wireOp",EDGE,"E8"),sQuery(id+"F0.wireOp",EDGE,"E9"),sQuery(id+"F0.wireOp",EDGE,"E10"),sQuery(id+"F0.wireOp",EDGE,"E11"),sQuery(id+"F0.wireOp",EDGE,"E12"),sQuery(id+"F0.wireOp",EDGE,"E13"),sQuery(id+"F0.wireOp",EDGE,"E14"),sQuery(id+"F0.wireOp",EDGE,"E15"),sQuery(id+"F0.wireOp",EDGE,"E16"),sQuery(id+"F0.wireOp",EDGE,"E17"),sQuery(id+"F0.wireOp",EDGE,"E18"),sQuery(id+"F0.wireOp",EDGE,"E19"),sQuery(id+"F0.wireOp",EDGE,"E20"),sQuery(id+"F0.wireOp",EDGE,"E21"),sQuery(id+"F0.wireOp",EDGE,"E22"),sQuery(id+"F0.wireOp",EDGE,"E23"),sQuery(id+"F0.wireOp",EDGE,"E24"),sQuery(id+"F0.wireOp",EDGE,"E25"),sQuery(id+"F0.wireOp",EDGE,"E26"),sQuery(id+"F0.wireOp",EDGE,"E27"),sQuery(id+"F0.wireOp",EDGE,"E28"),sQuery(id+"F0.wireOp",EDGE,"E29"),sQuery(id+"F0.wireOp",EDGE,"E30"),sQuery(id+"F0.wireOp",EDGE,"E31"),sQuery(id+"F0.wireOp",EDGE,"E32"),sQuery(id+"F0.wireOp",EDGE,"E33"),sQuery(id+"F0.wireOp",EDGE,"E34"),sQuery(id+"F0.wireOp",EDGE,"E35"),sQuery(id+"F0.wireOp",EDGE,"E36"),sQuery(id+"F0.wireOp",EDGE,"E37"),sQuery(id+"F0.wireOp",EDGE,"E38"),sQuery(id+"F0.wireOp",EDGE,"E39"),sQuery(id+"F0.wireOp",EDGE,"E40"),sQuery(id+"F0.wireOp",EDGE,"E41"),sQuery(id+"F0.wireOp",EDGE,"E42"),sQuery(id+"F0.wireOp",EDGE,"E43"),sQuery(id+"F0.wireOp",EDGE,"E44"),sQuery(id+"F0.wireOp",EDGE,"E45"),sQuery(id+"F0.wireOp",EDGE,"E46"),sQuery(id+"F0.wireOp",EDGE,"E47"),sQuery(id+"F0.wireOp",EDGE,"E48"),sQuery(id+"F0.wireOp",EDGE,"E49"),sQuery(id+"F0.wireOp",EDGE,"E50"),sQuery(id+"F0.wireOp",EDGE,"E51"),sQuery(id+"F0.wireOp",EDGE,"E52"),sQuery(id+"F0.wireOp",EDGE,"E53"),sQuery(id+"F0.wireOp",EDGE,"E54"),sQuery(id+"F0.wireOp",EDGE,"E55"),sQuery(id+"F0.wireOp",EDGE,"E56"),sQuery(id+"F0.wireOp",EDGE,"E57"),sQuery(id+"F0.wireOp",EDGE,"E58"),sQuery(id+"F0.wireOp",EDGE,"E59"),sQuery(id+"F0.wireOp",EDGE,"E60"),sQuery(id+"F0.wireOp",EDGE,"E61"),sQuery(id+"F0.wireOp",EDGE,"E62"),sQuery(id+"F0.wireOp",EDGE,"E63"),sQuery(id+"F0.wireOp",EDGE,"E64"),sQuery(id+"F0.wireOp",EDGE,"E65"),sQuery(id+"F0.wireOp",EDGE,"E66"),sQuery(id+"F0.wireOp",EDGE,"E67"),sQuery(id+"F0.wireOp",EDGE,"E68"),sQuery(id+"F0.wireOp",EDGE,"E69"),sQuery(id+"F0.wireOp",EDGE,"E70"),sQuery(id+"F0.wireOp",EDGE,"E71"),sQuery(id+"F0.wireOp",EDGE,"E72"),sQuery(id+"F0.wireOp",EDGE,"E73"),sQuery(id+"F0.wireOp",EDGE,"E74"),sQuery(id+"F0.wireOp",EDGE,"E75"),sQuery(id+"F0.wireOp",EDGE,"E76"),sQuery(id+"F0.wireOp",EDGE,"E77"),sQuery(id+"F0.wireOp",EDGE,"E78"),sQuery(id+"F0.wireOp",EDGE,"E79"),sQuery(id+"F0.wireOp",EDGE,"E80"),sQuery(id+"F0.wireOp",EDGE,"E81"),sQuery(id+"F0.wireOp",EDGE,"E82"),sQuery(id+"F0.wireOp",EDGE,"E83"),sQuery(id+"F0.wireOp",EDGE,"E84"),sQuery(id+"F0.wireOp",EDGE,"E85"),sQuery(id+"F0.wireOp",EDGE,"E86"),sQuery(id+"F0.wireOp",EDGE,"E87"),sQuery(id+"F0.wireOp",EDGE,"E88"),sQuery(id+"F0.wireOp",EDGE,"E89"),sQuery(id+"F0.wireOp",EDGE,"E90"),sQuery(id+"F0.wireOp",EDGE,"E91"),sQuery(id+"F0.wireOp",EDGE,"E92"),sQuery(id+"F0.wireOp",EDGE,"E93"),sQuery(id+"F0.wireOp",EDGE,"E94"),sQuery(id+"F0.wireOp",EDGE,"E95"),sQuery(id+"F0.wireOp",EDGE,"E96"),sQuery(id+"F0.wireOp",EDGE,"E97"),sQuery(id+"F0.wireOp",EDGE,"E98"),sQuery(id+"F0.wireOp",EDGE,"E99"),sQuery(id+"F0.wireOp",EDGE,"E100"),sQuery(id+"F0.wireOp",EDGE,"E101"),sQuery(id+"F0.wireOp",EDGE,"E102"),sQuery(id+"F0.wireOp",EDGE,"E103"),sQuery(id+"F0.wireOp",EDGE,"E104"),sQuery(id+"F0.wireOp",EDGE,"E105"),sQuery(id+"F0.wireOp",EDGE,"E106"),sQuery(id+"F0.wireOp",EDGE,"E107"),sQuery(id+"F0.wireOp",EDGE,"E108"),sQuery(id+"F0.wireOp",EDGE,"E109"),sQuery(id+"F0.wireOp",EDGE,"E110"),sQuery(id+"F0.wireOp",EDGE,"E111"),sQuery(id+"F0.wireOp",EDGE,"E112"),sQuery(id+"F0.wireOp",EDGE,"E113"),sQuery(id+"F0.wireOp",EDGE,"E114"),sQuery(id+"F0.wireOp",EDGE,"E115"),sQuery(id+"F0.wireOp",EDGE,"E116"),sQuery(id+"F0.wireOp",EDGE,"E117"),sQuery(id+"F0.wireOp",EDGE,"E118"),sQuery(id+"F0.wireOp",EDGE,"E119"),sQuery(id+"F0.wireOp",EDGE,"E120"),sQuery(id+"F0.wireOp",EDGE,"E121"),sQuery(id+"F0.wireOp",EDGE,"E122"),sQuery(id+"F0.wireOp",EDGE,"E123"),sQuery(id+"F0.wireOp",EDGE,"E124"),sQuery(id+"F0.wireOp",EDGE,"E125"),sQuery(id+"F0.wireOp",EDGE,"E126"),sQuery(id+"F0.wireOp",EDGE,"E127"),sQuery(id+"F0.wireOp",EDGE,"E128"),sQuery(id+"F0.wireOp",EDGE,"E129"),sQuery(id+"F0.wireOp",EDGE,"E130"),sQuery(id+"F0.wireOp",EDGE,"E131"),sQuery(id+"F0.wireOp",EDGE,"E132"),sQuery(id+"F0.wireOp",EDGE,"E133"),sQuery(id+"F0.wireOp",EDGE,"E134"),sQuery(id+"F0.wireOp",EDGE,"E135"),sQuery(id+"F0.wireOp",EDGE,"E136"),sQuery(id+"F0.wireOp",EDGE,"E137"),sQuery(id+"F0.wireOp",EDGE,"E138"),sQuery(id+"F0.wireOp",EDGE,"E139"),sQuery(id+"F0.wireOp",EDGE,"E140"),sQuery(id+"F0.wireOp",EDGE,"E141"),sQuery(id+"F0.wireOp",EDGE,"E142"),sQuery(id+"F0.wireOp",EDGE,"E143"),sQuery(id+"F0.wireOp",EDGE,"E144"),sQuery(id+"F0.wireOp",EDGE,"E145"),sQuery(id+"F0.wireOp",EDGE,"E146"),sQuery(id+"F0.wireOp",EDGE,"E147"),sQuery(id+"F0.wireOp",EDGE,"E148"),sQuery(id+"F0.wireOp",EDGE,"E149"),sQuery(id+"F0.wireOp",EDGE,"E150"),sQuery(id+"F0.wireOp",EDGE,"E151"),sQuery(id+"F0.wireOp",EDGE,"E152"),sQuery(id+"F0.wireOp",EDGE,"E153"),sQuery(id+"F0.wireOp",EDGE,"E154"),sQuery(id+"F0.wireOp",EDGE,"E155"),sQuery(id+"F0.wireOp",EDGE,"E156"),sQuery(id+"F0.wireOp",EDGE,"E157"),sQuery(id+"F0.wireOp",EDGE,"E158"),sQuery(id+"F0.wireOp",EDGE,"E159"),sQuery(id+"F0.wireOp",EDGE,"E160"),sQuery(id+"F0.wireOp",EDGE,"E161"),sQuery(id+"F0.wireOp",EDGE,"E162"),sQuery(id+"F0.wireOp",EDGE,"E163"),sQuery(id+"F0.wireOp",EDGE,"E164"),sQuery(id+"F0.wireOp",EDGE,"E165"),sQuery(id+"F0.wireOp",EDGE,"E166"),sQuery(id+"F0.wireOp",EDGE,"E167"),sQuery(id+"F0.wireOp",EDGE,"E168"),sQuery(id+"F0.wireOp",EDGE,"E169"),sQuery(id+"F0.wireOp",EDGE,"E170"),sQuery(id+"F0.wireOp",EDGE,"E171"),sQuery(id+"F0.wireOp",EDGE,"E172"),sQuery(id+"F0.wireOp",EDGE,"E173"),sQuery(id+"F0.wireOp",EDGE,"E174"),sQuery(id+"F0.wireOp",EDGE,"E175"),sQuery(id+"F0.wireOp",EDGE,"E176"),sQuery(id+"F0.wireOp",EDGE,"E177"),sQuery(id+"F0.wireOp",EDGE,"E178"),sQuery(id+"F0.wireOp",EDGE,"E179"),sQuery(id+"F0.wireOp",EDGE,"E180"),sQuery(id+"F0.wireOp",EDGE,"E181"),sQuery(id+"F0.wireOp",EDGE,"E182"),sQuery(id+"F0.wireOp",EDGE,"E183"),sQuery(id+"F0.wireOp",EDGE,"E184"),sQuery(id+"F0.wireOp",EDGE,"E185"),sQuery(id+"F0.wireOp",EDGE,"E186"),sQuery(id+"F0.wireOp",EDGE,"E187"),sQuery(id+"F0.wireOp",EDGE,"E188"),sQuery(id+"F0.wireOp",EDGE,"E189"),sQuery(id+"F0.wireOp",EDGE,"E190"),sQuery(id+"F0.wireOp",EDGE,"E191"),sQuery(id+"F0.wireOp",EDGE,"E192"),sQuery(id+"F0.wireOp",EDGE,"E193"),sQuery(id+"F0.wireOp",EDGE,"E194"),sQuery(id+"F0.wireOp",EDGE,"E195"),sQuery(id+"F0.wireOp",EDGE,"E196"),sQuery(id+"F0.wireOp",EDGE,"E197"),sQuery(id+"F0.wireOp",EDGE,"E198"),sQuery(id+"F0.wireOp",EDGE,"E199"),sQuery(id+"F0.wireOp",EDGE,"E200"),sQuery(id+"F0.wireOp",EDGE,"E201"),sQuery(id+"F0.wireOp",EDGE,"E202"),sQuery(id+"F0.wireOp",EDGE,"E203"),sQuery(id+"F0.wireOp",EDGE,"E204"),sQuery(id+"F0.wireOp",EDGE,"E205"),sQuery(id+"F0.wireOp",EDGE,"E206"),sQuery(id+"F0.wireOp",EDGE,"E207"),sQuery(id+"F0.wireOp",EDGE,"E208"),sQuery(id+"F0.wireOp",EDGE,"E209"),sQuery(id+"F0.wireOp",EDGE,"E210"),sQuery(id+"F0.wireOp",EDGE,"E211"),sQuery(id+"F0.wireOp",EDGE,"E212"),sQuery(id+"F0.wireOp",EDGE,"E213"),sQuery(id+"F0.wireOp",EDGE,"E214"),sQuery(id+"F0.wireOp",EDGE,"E215"),sQuery(id+"F0.wireOp",EDGE,"E216"),sQuery(id+"F0.wireOp",EDGE,"E217"),sQuery(id+"F0.wireOp",EDGE,"E218"),sQuery(id+"F0.wireOp",EDGE,"E219"),sQuery(id+"F0.wireOp",EDGE,"E220"),sQuery(id+"F0.wireOp",EDGE,"E221"),sQuery(id+"F0.wireOp",EDGE,"E222"),sQuery(id+"F0.wireOp",EDGE,"E223"),sQuery(id+"F0.wireOp",EDGE,"E224"),sQuery(id+"F0.wireOp",EDGE,"E225")])],"isStart":false});
            chamfer(context, id + "F6", {"entities" : qUnion([Q0]), "chamferType" : ChamferType.TWO_OFFSETS, "width1" : .7 * mm, "oppositeDirection" : false, "width2" : 2 * mm});
        }
    });
